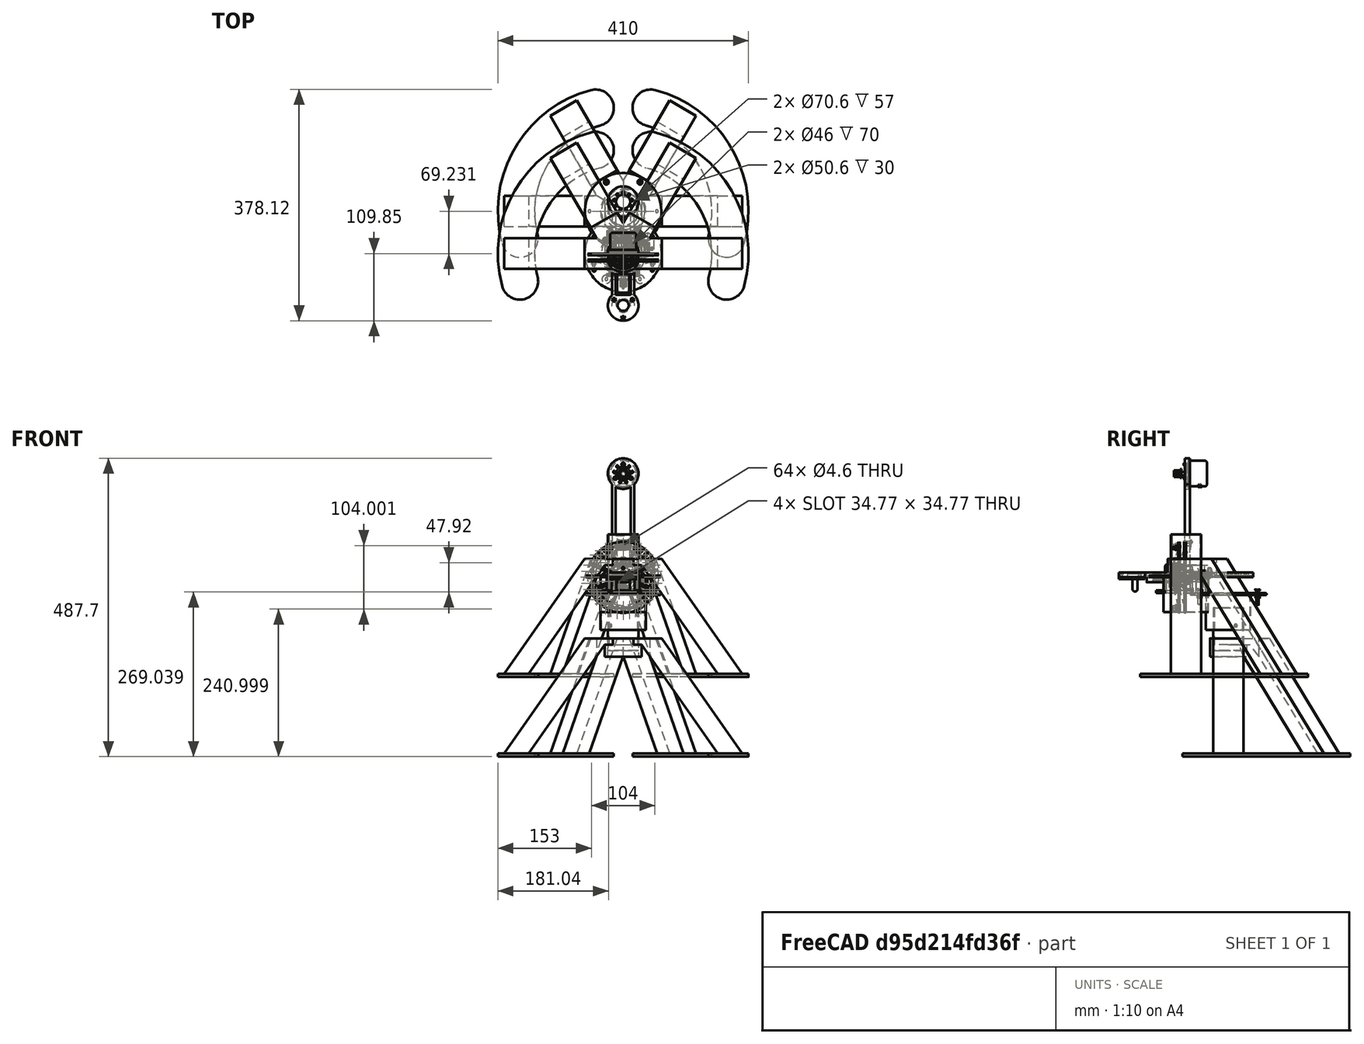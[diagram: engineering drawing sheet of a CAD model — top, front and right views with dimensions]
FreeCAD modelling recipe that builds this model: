
FCSTD DOCUMENT  (FreeCAD 1.0R38641 +678 (Git))
Label: assembly_Pendulum_fusion
License: All rights reserved
LicenseURL: https://en.wikipedia.org/wiki/All_rights_reserved
objects: Part::Feature×161, App::Part×99, Sketcher::SketchObject×51, Part::FeaturePython×47, PartDesign::Pad×32, PartDesign::CoordinateSystem×25, PartDesign::Pocket×17, Mesh::Feature×15, App::Link×14, PartDesign::Body×13, PartDesign::PolarPattern×7, PartDesign::Fillet×7, App::DocumentObjectGroup×5, PartDesign::Chamfer×4, Part::MultiFuse×3, App::FeaturePython×1, PartDesign::Revolution×1
note: 548 computed .brp shape members not serialized (recipe doc carries the construction recipe); baked Part::Feature solids carry a one-line shape summary decoded from their .brp

FEATURE [PartDesign::CoordinateSystem] LCS_Origin
  AttacherType = Attacher::AttachEngine3D
  AttachmentSupport = -> [X_Axis]
  MapMode = 2
FEATURE [App::DocumentObjectGroup] Constraints
FEATURE [App::FeaturePython] Variables  # WARN: FeaturePython — macro-defined, semantics opaque (R4)
  Type = App::PropertyContainer
  arm_rotation = 0
FEATURE [App::DocumentObjectGroup] Configurations
FEATURE [Sketcher::SketchObject] Sketch
  ArcFitTolerance = 1e-06
  AttachmentSupport = -> [XZ_Plane001]
  FullyConstrained = true
  MakeInternals = false
  MapMode = 5
  Placement = pos=(0,0,0) rot=(1,0,0;1.5708rad)
  sketch-geometry (13):
    g0: LineSegment StartX=5.6759 StartY=30.0968 StartZ=0 EndX=23.0689 EndY=6 EndZ=0
    g1: LineSegment StartX=23.0689 StartY=6 StartZ=0 EndX=34 EndY=6 EndZ=0
    g2: LineSegment StartX=34 StartY=6 StartZ=0 EndX=34 EndY=0 EndZ=0
    g3: LineSegment StartX=34 StartY=0 StartZ=0 EndX=20 EndY=0 EndZ=0
    g4: LineSegment StartX=20 StartY=0 StartZ=0 EndX=4.86567 EndY=20.9676 EndZ=0
    g5: LineSegment StartX=-4.86567 StartY=20.9676 StartZ=0 EndX=-20 EndY=0 EndZ=0
    g6: LineSegment StartX=-20 StartY=0 StartZ=0 EndX=-34 EndY=0 EndZ=0
    g7: LineSegment StartX=-34 StartY=0 StartZ=0 EndX=-34 EndY=6 EndZ=0
    g8: LineSegment StartX=-34 StartY=6 StartZ=0 EndX=-23.0689 EndY=6 EndZ=0
    g9: LineSegment StartX=-23.0689 StartY=6 StartZ=0 EndX=-5.6759 EndY=30.0968 EndZ=0
    g10: Circle CenterX=-1e-16 CenterY=26 CenterZ=0 NormalX=0 NormalY=0 NormalZ=1 AngleXU=0 Radius=2.8
    g11: ArcOfCircle CenterX=-1e-16 CenterY=26 CenterZ=0 NormalX=0 NormalY=0 NormalZ=1 AngleXU=0 Radius=7 StartAngle=0.625205 EndAngle=2.51639
    g12: ArcOfCircle CenterX=-1e-16 CenterY=26 CenterZ=0 NormalX=0 NormalY=0 NormalZ=1 AngleXU=0 Radius=7 StartAngle=3.94384 EndAngle=5.48094
  constraints (36):
    c: Coincident(g0,g1)
    c: Horizontal(g1)
    c: Coincident(g1,g2)
    c: PointOnObject(g2,g-1)
    c: Coincident(g2,g3)
    c: PointOnObject(g3,g-1)
    c: Coincident(g3,g4)
    c: Coincident(g5,g6)
    c: PointOnObject(g6,g-1)
    c: Coincident(g6,g7)
    c: Vertical(g7)
    c: Coincident(g7,g8)
    c: Horizontal(g8)
    c: Coincident(g8,g9)
    c: Symmetric(g9,g0,g-2)
    c: Parallel(g9,g5)
    c: Parallel(g0,g4)
    c: Vertical(g2)
    c: Equal(g7,g2)
    c: DistanceY(g7,g7) = 6
    c: Equal(g8,g1)
    c: DistanceX(g6,g6) = 14
    c: DistanceX(g5,g3) = 40
    c: Diameter(g10) = 5.6
    c: Coincident(g11,g10)
    c: Coincident(g11,g0)
    c: Equal(g11,g12)
    c: Coincident(g11,g12)
    c: Coincident(g4,g12)
    c: Coincident(g5,g12)
    c: DistanceY(g-1,g10) = 26
    c: Distance(g5,g9) = 6
    c: Distance(g4,g0) = 6
    c: Tangent(g9,g11) = 1.5708
    c: Diameter(g11) = 14
    c: Symmetric(g5,g3,g-2)
FEATURE [PartDesign::Pad] Pad  label="Pad_Main"
  Direction = (0,-1,2e-16)
  Length = 10
  Length2 = 10
  Placement = pos=(0,0,0) rot=(1,0,0;1.5708rad)
  Profile = -> Sketch
  ReferenceAxis = -> Sketch [N_Axis]
  Refine = true
  Suppressed = false
  Type = 0
FEATURE [Sketcher::SketchObject] Sketch001
  ArcFitTolerance = 1e-06
  AttachmentSupport = -> [Pad]
  ExternalGeometry = -> [Pad]
  FullyConstrained = true
  MakeInternals = false
  MapMode = 5
  Placement = pos=(0,-10,0) rot=(1,0,0;1.5708rad)
  sketch-geometry (2):
    g0: Circle CenterX=0 CenterY=26 CenterZ=0 NormalX=0 NormalY=0 NormalZ=1 AngleXU=0 Radius=3.8
    g1: Circle CenterX=0 CenterY=26 CenterZ=0 NormalX=0 NormalY=0 NormalZ=1 AngleXU=0 Radius=2.8
  constraints (4):
    c: Coincident(g0,g-3)
    c: Coincident(g1,g0)
    c: Diameter(g1) = 5.6
    c: Diameter(g0) = 7.6
FEATURE [PartDesign::Pad] Pad001  label="Pad_Shaft"
  BaseFeature = -> Pad
  Direction = (0,-1,2e-16)
  Length = 16.6
  Length2 = 10
  Placement = pos=(0,0,0) rot=(1,0,0;1.5708rad)
  Profile = -> Sketch001
  ReferenceAxis = -> Sketch001 [N_Axis]
  Refine = true
  Suppressed = false
  Type = 0
FEATURE [Sketcher::SketchObject] Sketch002
  ArcFitTolerance = 1e-06
  AttachmentSupport = -> [Pad001]
  ExternalGeometry = -> [Pad001]
  FullyConstrained = true
  MakeInternals = false
  MapMode = 5
  Placement = pos=(0,-10,0) rot=(1,0,0;1.5708rad)
  sketch-geometry (2):
    g0: Circle CenterX=0 CenterY=26 CenterZ=0 NormalX=0 NormalY=0 NormalZ=1 AngleXU=0 Radius=3.8
    g1: Circle CenterX=0 CenterY=26 CenterZ=0 NormalX=0 NormalY=0 NormalZ=1 AngleXU=0 Radius=6.5
  constraints (4):
    c: Coincident(g0,g-3)
    c: Equal(g0,g-3)
    c: Coincident(g1,g0)
    c: Diameter(g1) = 13
FEATURE [PartDesign::Pad] Pad002  label="Pad_Thrust"
  BaseFeature = -> Pad001
  Direction = (0,-1,2e-16)
  Length = 10
  Length2 = 10
  Placement = pos=(0,0,0) rot=(1,0,0;1.5708rad)
  Profile = -> Sketch002
  ReferenceAxis = -> Sketch002 [N_Axis]
  Refine = true
  Suppressed = false
  Type = 0
FEATURE [Sketcher::SketchObject] Sketch003
  ArcFitTolerance = 1e-06
  AttachmentSupport = -> [Pad002]
  FullyConstrained = true
  MakeInternals = false
  MapMode = 5
  Placement = pos=(0,2.9e-15,0) rot=(-1,0,0;1.5708rad)
  sketch-geometry (7):
    g0: LineSegment StartX=-4.8 StartY=-26 StartZ=0 EndX=-2.4 EndY=-30.1569 EndZ=0
    g1: LineSegment StartX=-2.4 StartY=-30.1569 StartZ=0 EndX=2.4 EndY=-30.1569 EndZ=0
    g2: LineSegment StartX=2.4 StartY=-30.1569 StartZ=0 EndX=4.8 EndY=-26 EndZ=0
    g3: LineSegment StartX=4.8 StartY=-26 StartZ=0 EndX=2.4 EndY=-21.8431 EndZ=0
    g4: LineSegment StartX=2.4 StartY=-21.8431 StartZ=0 EndX=-2.4 EndY=-21.8431 EndZ=0
    g5: LineSegment StartX=-2.4 StartY=-21.8431 StartZ=0 EndX=-4.8 EndY=-26 EndZ=0
    g6: Circle [constr] CenterX=0 CenterY=-26 CenterZ=0 NormalX=0 NormalY=0 NormalZ=1 AngleXU=0 Radius=4.8
  constraints (16):
    c: Coincident(g0,g1)
    c: Coincident(g1,g2)
    c: Coincident(g2,g3)
    c: Coincident(g3,g4)
    c: Coincident(g4,g5)
    c: Coincident(g5,g0)
    c: Equal(g0, g1-g5) x5
    c: PointOnObject(g0,g6)
    c: PointOnObject(g1,g6)
    c: PointOnObject(g2,g6)
    c: PointOnObject(g3,g6)
    c: PointOnObject(g4,g6)
    c: PointOnObject(g5,g6)
    c: Coincident(g6,g-3)
    c: Horizontal(g4)
    c: Diameter(g6) = 9.6
FEATURE [PartDesign::Pocket] Pocket
  BaseFeature = -> Pad002
  Direction = (0,-1,-2e-16)
  Length = 3
  Length2 = 5
  Placement = pos=(0,0,0) rot=(1,0,0;1.5708rad)
  Profile = -> Sketch003
  ReferenceAxis = -> Sketch003 [N_Axis]
  Refine = true
  Suppressed = false
  Type = 0
FEATURE [Sketcher::SketchObject] Sketch005  label="Sketch_section"
  ArcFitTolerance = 0
  AttachmentSupport = -> [XZ_Plane003]
  FullyConstrained = true
  MakeInternals = false
  MapMode = 5
  Placement = pos=(0,0,0) rot=(1,0,0;1.5708rad)
  sketch-geometry (12):
    g0: LineSegment StartX=4 StartY=-3.5 StartZ=0 EndX=6.5 EndY=-3.5 EndZ=0
    g1: LineSegment StartX=11 StartY=-3.5 StartZ=0 EndX=11 EndY=3.5 EndZ=0
    g2: LineSegment StartX=11 StartY=3.5 StartZ=0 EndX=9.25 EndY=3.5 EndZ=0
    g3: LineSegment StartX=4 StartY=3.5 StartZ=0 EndX=4 EndY=-3.5 EndZ=0
    g4: LineSegment StartX=6.5 StartY=3.5 StartZ=0 EndX=6.75 EndY=3.25 EndZ=0
    g5: LineSegment StartX=6.75 StartY=3.25 StartZ=0 EndX=9 EndY=3.25 EndZ=0
    g6: LineSegment StartX=9 StartY=3.25 StartZ=0 EndX=9.25 EndY=3.5 EndZ=0
    g7: LineSegment StartX=6.5 StartY=-3.5 StartZ=0 EndX=6.75 EndY=-3.25 EndZ=0
    g8: LineSegment StartX=6.75 StartY=-3.25 StartZ=0 EndX=9 EndY=-3.25 EndZ=0
    g9: LineSegment StartX=9 StartY=-3.25 StartZ=0 EndX=9.25 EndY=-3.5 EndZ=0
    g10: LineSegment StartX=6.5 StartY=3.5 StartZ=0 EndX=4 EndY=3.5 EndZ=0
    g11: LineSegment StartX=9.25 StartY=-3.5 StartZ=0 EndX=11 EndY=-3.5 EndZ=0
  constraints (33):
    c: Coincident(g11,g1)
    c: Coincident(g1,g2)
    c: Coincident(g10,g3)
    c: Coincident(g3,g0)
    c: Horizontal(g0)
    c: Horizontal(g2)
    c: Vertical(g1)
    c: DistanceY(g1) = 7
    c: DistanceX(g0) = 4
    c: DistanceX(g11) = 11
    c: Coincident(g4,g5)
    c: Horizontal(g5)
    c: Coincident(g5,g6)
    c: Coincident(g7,g8)
    c: Horizontal(g8)
    c: Coincident(g8,g9)
    c: Coincident(g2,g6)
    c: Coincident(g10,g4)
    c: Tangent(g2,g10)
    c: Coincident(g0,g7)
    c: Coincident(g11,g9)
    c: Tangent(g0,g11)
    c: Equal(g4,g6)
    c: Equal(g6,g7)
    c: Angle(g10,g4) = 2.35619
    c: DistanceX(g2) = -1.75
    c: DistanceX(g10) = -2.5
    c: Equal(g0,g10)
    c: Equal(g11,g2)
    c: Equal(g9,g7)
    c: Parallel(g9,g4)
    c: DistanceY(g5,g1) = 0.25
    c: Symmetric(g0,g3,g-1)
FEATURE [PartDesign::Revolution] Revolution
  Angle = 360
  Angle2 = 60
  Axis = (0,2e-16,1)
  Base = (0,0,0)
  Placement = pos=(0,0,0) rot=(1,0,0;1.5708rad)
  Profile = -> Sketch005
  ReferenceAxis = -> Sketch005 [V_Axis]
  Refine = true
  Suppressed = false
  Type = 0
FEATURE [PartDesign::Chamfer] Chamfer
  Angle = 45
  Base = -> Revolution [Edge12,Edge11]
  BaseFeature = -> Revolution
  ChamferType = 0
  FlipDirection = false
  Placement = pos=(0,0,0) rot=(1,0,0;1.5708rad)
  Refine = true
  Size = 0.25
  Size2 = 1
  SupportTransform = false
  Suppressed = false
  UseAllEdges = false
FEATURE [PartDesign::CoordinateSystem] Bearing_Axis
  AttacherType = Attacher::AttachEngine3D
  AttachmentSupport = -> [Chamfer]
  MapMode = 45
  Placement = pos=(1.89e-14,1.7e-15,3.5) rot=(0,0,1;0rad)
FEATURE [PartDesign::Body] Body002  label="Body_Bearing"
  AllowCompound = false
  Group = -> [Sketch005,Revolution,Chamfer,Bearing_Axis]
  Origin = -> Origin003
  Tip = -> Chamfer
FEATURE [Sketcher::SketchObject] Sketch006
  ArcFitTolerance = 1e-06
  AttachmentSupport = -> [XY_Plane004]
  FullyConstrained = true
  MakeInternals = false
  MapMode = 5
  sketch-geometry (1):
    g0: Circle CenterX=0 CenterY=84.85 CenterZ=0 NormalX=0 NormalY=0 NormalZ=1 AngleXU=0 Radius=23
  constraints (3):
    c: PointOnObject(g0,g-2)
    c: DistanceY(g-1,g0) = 84.85
    c: Diameter(g0) = 46
FEATURE [Sketcher::SketchObject] Sketch007
  ArcFitTolerance = 1e-06
  AttachmentSupport = -> [XY_Plane004]
  FullyConstrained = true
  MakeInternals = false
  MapMode = 5
  sketch-geometry (33):
    g0: LineSegment StartX=-18 StartY=67.5 StartZ=0 EndX=-18 EndY=-67.5 EndZ=0
    g1: LineSegment StartX=18 StartY=-67.5 StartZ=0 EndX=18 EndY=67.5 EndZ=0
    g2: ArcOfCircle CenterX=0 CenterY=84.8494 CenterZ=0 NormalX=0 NormalY=0 NormalZ=1 AngleXU=0 Radius=25 StartAngle=5.51619 EndAngle=10.1918
    g3: Circle CenterX=0 CenterY=84.8494 CenterZ=0 NormalX=0 NormalY=0 NormalZ=1 AngleXU=0 Radius=11.5
    g4: Circle CenterX=0 CenterY=99.8494 CenterZ=0 NormalX=0 NormalY=0 NormalZ=1 AngleXU=0 Radius=1.8
    g5: Circle CenterX=9.64181 CenterY=96.34 CenterZ=0 NormalX=0 NormalY=0 NormalZ=1 AngleXU=0 Radius=1.8
    g6: Circle CenterX=14.7721 CenterY=87.4541 CenterZ=0 NormalX=0 NormalY=0 NormalZ=1 AngleXU=0 Radius=1.8
    g7: Circle CenterX=12.9904 CenterY=77.3494 CenterZ=0 NormalX=0 NormalY=0 NormalZ=1 AngleXU=0 Radius=1.8
    g8: Circle CenterX=5.1303 CenterY=70.754 CenterZ=0 NormalX=0 NormalY=0 NormalZ=1 AngleXU=0 Radius=1.8
    g9: Circle CenterX=-5.1303 CenterY=70.754 CenterZ=0 NormalX=0 NormalY=0 NormalZ=1 AngleXU=0 Radius=1.8
    g10: Circle CenterX=-12.9904 CenterY=77.3494 CenterZ=0 NormalX=0 NormalY=0 NormalZ=1 AngleXU=0 Radius=1.8
    g11: Circle CenterX=-14.7721 CenterY=87.4541 CenterZ=0 NormalX=0 NormalY=0 NormalZ=1 AngleXU=0 Radius=1.8
    g12: Circle CenterX=-9.64181 CenterY=96.34 CenterZ=0 NormalX=0 NormalY=0 NormalZ=1 AngleXU=0 Radius=1.8
    g13: LineSegment [constr] StartX=-9.64181 StartY=96.34 StartZ=0 EndX=0 EndY=84.8494 EndZ=0
    g14: LineSegment [constr] StartX=-14.7721 StartY=87.4541 StartZ=0 EndX=0 EndY=84.8494 EndZ=0
    g15: LineSegment [constr] StartX=-12.9904 StartY=77.3494 StartZ=0 EndX=0 EndY=84.8494 EndZ=0
    g16: LineSegment [constr] StartX=-5.1303 StartY=70.754 StartZ=0 EndX=0 EndY=84.8494 EndZ=0
    g17: LineSegment [constr] StartX=5.1303 StartY=70.754 StartZ=0 EndX=0 EndY=84.8494 EndZ=0
    g18: LineSegment [constr] StartX=12.9904 StartY=77.3494 StartZ=0 EndX=0 EndY=84.8494 EndZ=0
    g19: LineSegment [constr] StartX=14.7721 StartY=87.4541 StartZ=0 EndX=0 EndY=84.8494 EndZ=0
    g20: LineSegment [constr] StartX=9.64181 StartY=96.34 StartZ=0 EndX=0 EndY=84.8494 EndZ=0
    g21: Circle CenterX=-7.78 CenterY=-27 CenterZ=0 NormalX=0 NormalY=0 NormalZ=1 AngleXU=0 Radius=1.8
    g22: Circle CenterX=7.78 CenterY=-27 CenterZ=0 NormalX=0 NormalY=0 NormalZ=1 AngleXU=0 Radius=1.8
    g23: ArcOfCircle CenterX=0 CenterY=-84.8494 CenterZ=0 NormalX=0 NormalY=0 NormalZ=1 AngleXU=0 Radius=25 StartAngle=2.3746 EndAngle=7.05018
    g24: Circle CenterX=0 CenterY=-84.8494 CenterZ=0 NormalX=0 NormalY=0 NormalZ=1 AngleXU=0 Radius=11.25
    g25: LineSegment StartX=-12.5 StartY=63.1987 StartZ=0 EndX=-12.5 EndY=-16.8013 EndZ=0
    g26: LineSegment StartX=-12.5 StartY=-16.8013 StartZ=0 EndX=12.5 EndY=-16.8013 EndZ=0
    g27: LineSegment StartX=12.5 StartY=-16.8013 StartZ=0 EndX=12.5 EndY=63.1987 EndZ=0
    g28: LineSegment StartX=-12.5 StartY=-33.5 StartZ=0 EndX=-12.5 EndY=-67.5 EndZ=0
    g29: LineSegment StartX=-12.5 StartY=-67.5 StartZ=0 EndX=12.5 EndY=-67.5 EndZ=0
    g30: LineSegment StartX=12.5 StartY=-67.5 StartZ=0 EndX=12.5 EndY=-33.5 EndZ=0
    g31: LineSegment StartX=12.5 StartY=-33.5 StartZ=0 EndX=-12.5 EndY=-33.5 EndZ=0
    g32: ArcOfCircle CenterX=0 CenterY=84.8494 CenterZ=0 NormalX=0 NormalY=0 NormalZ=1 AngleXU=0 Radius=25 StartAngle=4.18879 EndAngle=5.23599
  constraints (88):
    c: Vertical(g0)
    c: Vertical(g1)
    c: Symmetric(g0,g1,g-1)
    c: DistanceX(g0,g1) = 36
    c: DistanceY(g1,g1) = 135
    c: PointOnObject(g2,g-2)
    c: Diameter(g2) = 50
    c: Coincident(g2,g0)
    c: Coincident(g2,g1)
    c: Coincident(g3,g2)
    c: Diameter(g3) = 23
    c: PointOnObject(g4,g-2)
    c: Coincident(g13,g12)
    c: Coincident(g13,g2)
    c: Coincident(g14,g11)
    c: Coincident(g14,g2)
    c: Coincident(g15,g10)
    c: Coincident(g15,g2)
    c: Coincident(g16,g9)
    c: Coincident(g16,g2)
    c: Coincident(g17,g8)
    c: Coincident(g17,g2)
    c: Coincident(g18,g7)
    c: Coincident(g18,g2)
    c: Coincident(g19,g6)
    c: Coincident(g19,g2)
    c: Coincident(g20,g5)
    c: Coincident(g20,g2)
    c: Equal(g4,g5)
    c: Equal(g5,g6)
    c: Equal(g6,g7)
    c: Equal(g7,g8)
    c: Equal(g8,g9)
    c: Equal(g9,g10)
    c: Equal(g10,g11)
    c: Equal(g11,g12)
    c: Equal(g13,g14)
    c: Equal(g14,g15)
    c: Equal(g15,g16)
    c: Equal(g16,g17)
    c: Equal(g17,g18)
    c: Equal(g18,g19)
    c: Equal(g19,g20)
    c: DistanceY(g2,g4) = 15
    c: Distance(g13) = 15
    c: Diameter(g4) = 3.6
    c: Angle(g-2,g20) = 2.44346
    c: Angle(g19,g20) = 0.698132
    c: Angle(g18,g19) = 0.698132
    c: Angle(g17,g18) = 0.698132
    c: Angle(g16,g17) = 0.698132
    c: Angle(g15,g16) = 0.698132
    c: Angle(g14,g15) = 0.698132
    c: Angle(g13,g14) = 0.698132
    c: Equal(g22,g21)
    c: Diameter(g21) = 3.6
    c: DistanceX(g21,g22) = 15.56
    c: Symmetric(g21,g22,g-2)
    c: DistanceY(g22,g-1) = 27
    c: PointOnObject(g23,g-2)
    c: Diameter(g23) = 50
    c: Coincident(g23,g1)
    c: Coincident(g23,g0)
    c: Coincident(g24,g23)
    c: Diameter(g24) = 22.5
    c: Vertical(g25)
    c: Vertical(g27)
    c: Horizontal(g26)
    c: Coincident(g28,g29)
    c: Coincident(g29,g30)
    c: Coincident(g30,g31)
    c: Coincident(g31,g28)
    c: Vertical(g28)
    c: Vertical(g30)
    c: Horizontal(g29)
    c: Symmetric(g27,g25,g-2)
    c: DistanceY(g25,g25) = 80
    c: DistanceX(g25,g27) = 25
    c: PointOnObject(g1,g29)
    c: Symmetric(g28,g30,g-2)
    c: DistanceX(g31,g31) = 25
    c: DistanceY(g28,g28) = 34
    c: Diameter(g32) = 50
    c: Coincident(g32,g25)
    c: Coincident(g32,g27)
    c: Coincident(g32,g2)
    c: Coincident(g26,g25)
    c: Coincident(g27,g26)
FEATURE [PartDesign::Pad] Pad004  label="Pad_Arm"
  Direction = (0,0,1)
  Length = 8
  Length2 = 10
  Profile = -> Sketch007
  ReferenceAxis = -> Sketch007 [N_Axis]
  Refine = true
  Suppressed = false
  Type = 0
FEATURE [PartDesign::Pocket] Pocket001  label="Pocket_Motor"
  BaseFeature = -> Pad004
  Direction = (0,0,-1)
  Length = 3
  Length2 = 5
  Profile = -> Sketch006
  ReferenceAxis = -> Sketch006 [N_Axis]
  Refine = true
  Reversed = true
  Suppressed = false
  Type = 0
FEATURE [PartDesign::CoordinateSystem] Arm_Axis_Top
  AttacherType = Attacher::AttachEngine3D
  AttachmentOffset = pos=(0,0,0) rot=(0,0,-1;1.5708rad)
  AttachmentSupport = -> [Pocket001]
  MapMode = 11
  Placement = pos=(2e-16,99.8494,8) rot=(0,0,1;0rad)
FEATURE [Sketcher::SketchObject] Sketch008
  ArcFitTolerance = 1e-06
  AttachmentSupport = -> [XZ_Plane005]
  FullyConstrained = true
  MakeInternals = false
  MapMode = 5
  Placement = pos=(0,0,0) rot=(1,0,0;1.5708rad)
  sketch-geometry (8):
    g0: LineSegment StartX=-3.7 StartY=11.6 StartZ=0 EndX=-3.7 EndY=8 EndZ=0
    g1: LineSegment StartX=-3.7 StartY=8 StartZ=0 EndX=3.7 EndY=8 EndZ=0
    g2: LineSegment StartX=3.7 StartY=8 StartZ=0 EndX=3.7 EndY=11.6 EndZ=0
    g3: LineSegment StartX=3.7 StartY=11.6 StartZ=0 EndX=-3.7 EndY=11.6 EndZ=0
    g4: LineSegment StartX=-3.7 StartY=-8 StartZ=0 EndX=-3.7 EndY=-11.6 EndZ=0
    g5: LineSegment StartX=-3.7 StartY=-11.6 StartZ=0 EndX=3.7 EndY=-11.6 EndZ=0
    g6: LineSegment StartX=3.7 StartY=-11.6 StartZ=0 EndX=3.7 EndY=-8 EndZ=0
    g7: LineSegment StartX=3.7 StartY=-8 StartZ=0 EndX=-3.7 EndY=-8 EndZ=0
  constraints (21):
    c: Coincident(g0,g1)
    c: Coincident(g1,g2)
    c: Coincident(g2,g3)
    c: Coincident(g3,g0)
    c: Vertical(g0)
    c: Vertical(g2)
    c: Coincident(g4,g5)
    c: Coincident(g5,g6)
    c: Coincident(g6,g7)
    c: Coincident(g7,g4)
    c: Vertical(g4)
    c: Vertical(g6)
    c: Horizontal(g5)
    c: Horizontal(g7)
    c: Symmetric(g0,g6,g-1)
    c: DistanceY(g-1,g1) = 8
    c: DistanceY(g2,g2) = 3.6
    c: DistanceX(g3,g3) = 7.4
    c: Symmetric(g2,g4,g-1)
    c: Symmetric(g1,g0,g-2)
    c: Horizontal(g3)
FEATURE [Sketcher::SketchObject] Sketch009
  ArcFitTolerance = 1e-06
  AttachmentSupport = -> [XY_Plane005]
  FullyConstrained = true
  MakeInternals = false
  MapMode = 5
  sketch-geometry (1):
    g0: Circle CenterX=0 CenterY=-6 CenterZ=0 NormalX=0 NormalY=0 NormalZ=1 AngleXU=0 Radius=2.25
  constraints (3):
    c: PointOnObject(g0,g-2)
    c: Diameter(g0) = 4.5
    c: DistanceY(g0,g-1) = 6
FEATURE [Sketcher::SketchObject] Sketch010
  ArcFitTolerance = 1e-06
  AttachmentOffset = pos=(0,0,0) rot=(1,0,0;0.392699rad)
  AttachmentSupport = -> [YZ_Plane005]
  FullyConstrained = true
  MakeInternals = false
  MapMode = 5
  Placement = pos=(0,0,0) rot=(0.639338,0.639338,0.427192;2.33414rad)
  sketch-geometry (4):
    g0: LineSegment StartX=-3 StartY=14.5 StartZ=0 EndX=-12 EndY=14.5 EndZ=0
    g1: LineSegment StartX=-12 StartY=14.5 StartZ=0 EndX=-5 EndY=44.5 EndZ=0
    g2: LineSegment StartX=-5 StartY=44.5 StartZ=0 EndX=-3 EndY=44.5 EndZ=0
    g3: LineSegment StartX=-3 StartY=44.5 StartZ=0 EndX=-3 EndY=14.5 EndZ=0
  constraints (12):
    c: Coincident(g0,g1)
    c: Coincident(g1,g2)
    c: Horizontal(g2)
    c: Coincident(g2,g3)
    c: Coincident(g3,g0)
    c: Horizontal(g0)
    c: Vertical(g3)
    c: DistanceX(g0,g-1) = 3
    c: DistanceY(g-1,g0) = 14.5
    c: DistanceY(g3,g3) = 30
    c: DistanceX(g2,g2) = 2
    c: DistanceX(g0,g0) = 9
FEATURE [Sketcher::SketchObject] Sketch011
  ArcFitTolerance = 1e-06
  AttachmentSupport = -> [XZ_Plane005]
  FullyConstrained = true
  MakeInternals = false
  MapMode = 5
  Placement = pos=(0,0,0) rot=(1,0,0;1.5708rad)
  sketch-geometry (1):
    g0: Circle CenterX=0 CenterY=52 CenterZ=0 NormalX=0 NormalY=0 NormalZ=1 AngleXU=0 Radius=2.3
  constraints (3):
    c: PointOnObject(g0,g-2)
    c: Diameter(g0) = 4.6
    c: DistanceY(g-1,g0) = 52
FEATURE [Sketcher::SketchObject] Sketch012
  ArcFitTolerance = 1e-06
  AttachmentSupport = -> [XZ_Plane005]
  FullyConstrained = true
  MakeInternals = false
  MapMode = 5
  Placement = pos=(0,0,0) rot=(1,0,0;1.5708rad)
  sketch-geometry (5):
    g0: LineSegment StartX=0 StartY=0 StartZ=0 EndX=-1.04189 EndY=5.90885 EndZ=0
    g1: LineSegment StartX=-1.04189 StartY=5.90885 StartZ=0 EndX=-0.2 EndY=5.3692 EndZ=0
    g2: LineSegment StartX=-0.2 StartY=5.3692 StartZ=0 EndX=0.2 EndY=5.3692 EndZ=0
    g3: LineSegment StartX=0.2 StartY=5.3692 StartZ=0 EndX=1.04189 EndY=5.90885 EndZ=0
    g4: LineSegment StartX=1.04189 StartY=5.90885 StartZ=0 EndX=0 EndY=0 EndZ=0
  constraints (13):
    c: Coincident(g-1,g0)
    c: Coincident(g0,g1)
    c: Coincident(g1,g2)
    c: Horizontal(g2)
    c: Coincident(g2,g3)
    c: Coincident(g3,g4)
    c: Coincident(g4,g0)
    c: Symmetric(g3,g0,g-2)
    c: Angle(g4,g0) = 0.349066
    c: DistanceX(g2,g2) = 0.4
    c: Distance(g4) = 6
    c: Distance(g3) = 1
    c: Distance(g1) = 1
FEATURE [Sketcher::SketchObject] Sketch013
  ArcFitTolerance = 1e-06
  AttachmentSupport = -> [XZ_Plane005]
  FullyConstrained = true
  MakeInternals = false
  MapMode = 5
  Placement = pos=(0,0,0) rot=(1,0,0;1.5708rad)
  sketch-geometry (2):
    g0: Circle CenterX=0 CenterY=0 CenterZ=0 NormalX=0 NormalY=0 NormalZ=1 AngleXU=0 Radius=5
    g1: Circle CenterX=0 CenterY=0 CenterZ=0 NormalX=0 NormalY=0 NormalZ=1 AngleXU=0 Radius=15
  constraints (4):
    c: Coincident(g0,g-1)
    c: Coincident(g1,g0)
    c: Diameter(g1) = 30
    c: Diameter(g0) = 10
FEATURE [Sketcher::SketchObject] Sketch014
  ArcFitTolerance = 1e-06
  AttachmentSupport = -> [XZ_Plane005]
  FullyConstrained = true
  MakeInternals = false
  MapMode = 5
  Placement = pos=(0,0,0) rot=(1,0,0;1.5708rad)
  sketch-geometry (6):
    g0: ArcOfCircle CenterX=0 CenterY=0 CenterZ=0 NormalX=0 NormalY=0 NormalZ=1 AngleXU=0 Radius=15 StartAngle=1.23918 EndAngle=1.90241
    g1: ArcOfCircle CenterX=0 CenterY=0 CenterZ=0 NormalX=0 NormalY=0 NormalZ=1 AngleXU=0 Radius=46 StartAngle=1.23918 EndAngle=1.90241
    g2: LineSegment [constr] StartX=0 StartY=0 StartZ=0 EndX=-19.5341 EndY=56.7311 EndZ=0
    g3: LineSegment [constr] StartX=0 StartY=0 StartZ=0 EndX=19.5341 EndY=56.7311 EndZ=0
    g4: LineSegment StartX=-4.88352 StartY=14.1828 StartZ=0 EndX=-14.9761 EndY=43.4939 EndZ=0
    g5: LineSegment StartX=14.9761 StartY=43.4939 StartZ=0 EndX=4.88352 EndY=14.1828 EndZ=0
  constraints (17):
    c: Coincident(g0,g-1)
    c: Coincident(g1,g0)
    c: Coincident(g2,g0)
    c: Coincident(g3,g0)
    c: Coincident(g4,g0)
    c: Coincident(g4,g1)
    c: Coincident(g5,g1)
    c: Coincident(g5,g0)
    c: Symmetric(g2,g3,g-2)
    c: Angle(g3,g2) = 0.663225
    c: PointOnObject(g0,g3)
    c: PointOnObject(g1,g3)
    c: PointOnObject(g0,g2)
    c: PointOnObject(g1,g2)
    c: Diameter(g1) = 92
    c: Diameter(g0) = 30
    c: Distance(g3) = 60
FEATURE [Sketcher::SketchObject] Sketch015
  ArcFitTolerance = 1e-06
  AttachmentSupport = -> [XZ_Plane005]
  FullyConstrained = true
  MakeInternals = false
  MapMode = 5
  Placement = pos=(0,0,0) rot=(1,0,0;1.5708rad)
  sketch-geometry (2):
    g0: Circle CenterX=0 CenterY=0 CenterZ=0 NormalX=0 NormalY=0 NormalZ=1 AngleXU=0 Radius=58
    g1: Circle CenterX=0 CenterY=0 CenterZ=0 NormalX=0 NormalY=0 NormalZ=1 AngleXU=0 Radius=5
  constraints (4):
    c: Coincident(g0,g-1)
    c: Diameter(g0) = 116
    c: Coincident(g1,g0)
    c: Diameter(g1) = 10
FEATURE [PartDesign::Pad] Pad005  label="Pad_External"
  Direction = (0,-1,2e-16)
  Length = 3
  Length2 = 10
  Placement = pos=(0,0,0) rot=(1,0,0;1.5708rad)
  Profile = -> Sketch015
  ReferenceAxis = -> Sketch015 [N_Axis]
  Refine = true
  Suppressed = false
  Type = 0
FEATURE [PartDesign::Pocket] Pocket002  label="Pocket_Gap"
  BaseFeature = -> Pad005
  Direction = (0,1,-2e-16)
  Length = 5
  Length2 = 5
  Placement = pos=(0,0,0) rot=(1,0,0;1.5708rad)
  Profile = -> Sketch014
  ReferenceAxis = -> Sketch014 [N_Axis]
  Refine = true
  Reversed = true
  Suppressed = false
  Type = 0
FEATURE [PartDesign::PolarPattern] PolarPattern  label="PolarPattern_Gaps"
  Angle = 360
  Axis = -> Sketch014 [N_Axis]
  BaseFeature = -> Pocket002
  Mode = 0
  Occurrences = 8
  Offset = 120
  Originals = -> [Pocket002]
  Placement = pos=(0,0,0) rot=(1,0,0;1.5708rad)
  Refine = true
  Suppressed = false
  TransformMode = 0
FEATURE [PartDesign::Pad] Pad006  label="Pad_Center"
  BaseFeature = -> PolarPattern
  Direction = (0,-1,2e-16)
  Length = 12
  Length2 = 10
  Placement = pos=(0,0,0) rot=(1,0,0;1.5708rad)
  Profile = -> Sketch013
  ReferenceAxis = -> Sketch013 [N_Axis]
  Refine = true
  Suppressed = false
  Type = 0
FEATURE [PartDesign::Pocket] Pocket003  label="Pocket_Shaft"
  BaseFeature = -> Pad006
  Direction = (0,1,-2e-16)
  Length = 5
  Length2 = 5
  Placement = pos=(0,0,0) rot=(1,0,0;1.5708rad)
  Profile = -> Sketch012
  ReferenceAxis = -> Sketch012 [N_Axis]
  Refine = true
  Reversed = true
  Suppressed = false
  Type = 1
FEATURE [PartDesign::PolarPattern] PolarPattern001  label="PolarPattern_DriveShaft"
  Angle = 360
  Axis = -> Sketch012 [N_Axis]
  BaseFeature = -> Pocket003
  Mode = 0
  Occurrences = 18
  Offset = 120
  Originals = -> [Pocket003]
  Placement = pos=(0,0,0) rot=(1,0,0;1.5708rad)
  Refine = true
  Suppressed = false
  TransformMode = 0
FEATURE [PartDesign::Pocket] Pocket004  label="Pocket_Screw"
  BaseFeature = -> PolarPattern001
  Direction = (0,1,-2e-16)
  Length = 5
  Length2 = 5
  Placement = pos=(0,0,0) rot=(1,0,0;1.5708rad)
  Profile = -> Sketch011
  ReferenceAxis = -> Sketch011 [N_Axis]
  Refine = true
  Reversed = true
  Suppressed = false
  Type = 1
FEATURE [PartDesign::PolarPattern] PolarPattern002  label="PolarPattern_Inertia"
  Angle = 360
  Axis = -> Sketch011 [N_Axis]
  BaseFeature = -> Pocket004
  Mode = 0
  Occurrences = 32
  Offset = 120
  Originals = -> [Pocket004]
  Placement = pos=(0,0,0) rot=(1,0,0;1.5708rad)
  Refine = true
  Suppressed = false
  TransformMode = 0
FEATURE [PartDesign::Pad] Pad007  label="Pad_Reinforcement"
  BaseFeature = -> PolarPattern002
  Direction = (0.92388,0,-0.382683)
  Length = 2
  Length2 = 10
  Midplane = true
  Placement = pos=(0,0,0) rot=(1,0,0;1.5708rad)
  Profile = -> Sketch010
  ReferenceAxis = -> Sketch010 [N_Axis]
  Refine = true
  Suppressed = false
  Type = 0
FEATURE [PartDesign::PolarPattern] PolarPattern003  label="PolarPattern_Reinforcements"
  Angle = 360
  Axis = -> Y_Axis005
  BaseFeature = -> Pad007
  Mode = 0
  Occurrences = 8
  Offset = 120
  Originals = -> [Pad007]
  Placement = pos=(0,0,0) rot=(1,0,0;1.5708rad)
  Refine = true
  Suppressed = false
  TransformMode = 0
FEATURE [PartDesign::Pocket] Pocket005  label="Pocket_Fixation"
  BaseFeature = -> PolarPattern003
  Direction = (0,0,-1)
  Length = 30
  Length2 = 5
  Midplane = true
  Placement = pos=(0,0,0) rot=(1,0,0;1.5708rad)
  Profile = -> Sketch009
  ReferenceAxis = -> Sketch009 [N_Axis]
  Refine = true
  Suppressed = false
  Type = 0
FEATURE [PartDesign::Pocket] Pocket006  label="Pocket_Bolts"
  BaseFeature = -> Pocket005
  Direction = (0,1,-2e-16)
  Length = 12
  Length2 = 5
  Placement = pos=(0,0,0) rot=(1,0,0;1.5708rad)
  Profile = -> Sketch008
  ReferenceAxis = -> Sketch008 [N_Axis]
  Refine = true
  Reversed = true
  Suppressed = false
  Type = 0
FEATURE [Sketcher::SketchObject] Sketch016
  ArcFitTolerance = 1e-06
  AttachmentSupport = -> [XY_Plane006]
  FullyConstrained = true
  MakeInternals = false
  MapMode = 5
  sketch-geometry (8):
    g0: LineSegment StartX=-7.5 StartY=-8 StartZ=0 EndX=-7.5 EndY=-13 EndZ=0
    g1: LineSegment StartX=7.5 StartY=-13 StartZ=0 EndX=7.5 EndY=-8 EndZ=0
    g2: LineSegment StartX=7.5 StartY=-8 StartZ=0 EndX=-7.5 EndY=-8 EndZ=0
    g3: LineSegment StartX=-10 StartY=-13 StartZ=0 EndX=-10 EndY=-14.2 EndZ=0
    g4: LineSegment StartX=-10 StartY=-14.2 StartZ=0 EndX=10 EndY=-14.2 EndZ=0
    g5: LineSegment StartX=10 StartY=-14.2 StartZ=0 EndX=10 EndY=-13 EndZ=0
    g6: LineSegment StartX=10 StartY=-13 StartZ=0 EndX=7.5 EndY=-13 EndZ=0
    g7: LineSegment StartX=-7.5 StartY=-13 StartZ=0 EndX=-10 EndY=-13 EndZ=0
  constraints (21):
    c: Coincident(g1,g2)
    c: Coincident(g2,g0)
    c: Vertical(g0)
    c: Coincident(g3,g4)
    c: Coincident(g4,g5)
    c: Coincident(g5,g6)
    c: Coincident(g7,g3)
    c: Vertical(g3)
    c: Vertical(g5)
    c: Horizontal(g6)
    c: Coincident(g6,g1)
    c: Coincident(g0,g7)
    c: Symmetric(g0,g1,g-2)
    c: Symmetric(g3,g4,g-2)
    c: Symmetric(g0,g1,g-2)
    c: DistanceX(g2,g2) = 15
    c: DistanceX(g4,g4) = 20
    c: DistanceY(g3,g3) = 1.2
    c: Horizontal(g7)
    c: DistanceY(g0,g0) = 5
    c: DistanceY(g0,g-1) = 8
FEATURE [Sketcher::SketchObject] Sketch017
  ArcFitTolerance = 1e-06
  AttachmentOffset = pos=(0,0,42) rot=(0,0,1;0rad)
  AttachmentSupport = -> [XZ_Plane006]
  FullyConstrained = true
  MakeInternals = false
  MapMode = 5
  Placement = pos=(0,-42,9.3e-15) rot=(1,0,0;1.5708rad)
  sketch-geometry (5):
    g0: LineSegment StartX=-0.955065 StartY=5.41644 StartZ=0 EndX=0 EndY=0 EndZ=0
    g1: LineSegment StartX=0.955065 StartY=5.41644 StartZ=0 EndX=0 EndY=0 EndZ=0
    g2: LineSegment StartX=-0.955065 StartY=5.41644 StartZ=0 EndX=-0.2 EndY=4.76079 EndZ=0
    g3: LineSegment StartX=-0.2 StartY=4.76079 StartZ=0 EndX=0.2 EndY=4.76079 EndZ=0
    g4: LineSegment StartX=0.2 StartY=4.76079 StartZ=0 EndX=0.955065 EndY=5.41644 EndZ=0
  constraints (12):
    c: Coincident(g0,g-1)
    c: Coincident(g1,g0)
    c: Coincident(g3,g2)
    c: Coincident(g4,g3)
    c: Coincident(g4,g1)
    c: Symmetric(g3,g2,g-2)
    c: Coincident(g2,g0)
    c: Symmetric(g0,g1,g-2)
    c: Angle(g1,g0) = 0.349066
    c: DistanceX(g3,g3) = 0.4
    c: Distance(g1) = 5.5
    c: Distance(g4) = 1
FEATURE [Sketcher::SketchObject] Sketch018
  ArcFitTolerance = 1e-06
  AttachmentSupport = -> [XZ_Plane006]
  FullyConstrained = true
  MakeInternals = false
  MapMode = 5
  Placement = pos=(0,0,0) rot=(1,0,0;1.5708rad)
  sketch-geometry (1):
    g0: Circle CenterX=0 CenterY=0 CenterZ=0 NormalX=0 NormalY=0 NormalZ=1 AngleXU=0 Radius=21
  constraints (2):
    c: Coincident(g0,g-1)
    c: Diameter(g0) = 42
FEATURE [PartDesign::Pad] Pad008  label="Pad_Cylinder"
  Direction = (0,-1,2e-16)
  Length = 34
  Length2 = 10
  Placement = pos=(0,0,0) rot=(1,0,0;1.5708rad)
  Profile = -> Sketch018
  ReferenceAxis = -> Sketch018 [N_Axis]
  Refine = true
  Suppressed = false
  Type = 0
FEATURE [Sketcher::SketchObject] Sketch019
  ArcFitTolerance = 1e-06
  AttachmentSupport = -> [Pad008]
  FullyConstrained = true
  MakeInternals = false
  MapMode = 5
  Placement = pos=(0,-34,0) rot=(1,0,0;1.5708rad)
  sketch-geometry (1):
    g0: Circle CenterX=0 CenterY=0 CenterZ=0 NormalX=0 NormalY=0 NormalZ=1 AngleXU=0 Radius=7.5
  constraints (2):
    c: Coincident(g0,g-1)
    c: Diameter(g0) = 15
FEATURE [PartDesign::Pad] Pad009  label="Pad_Bearing"
  BaseFeature = -> Pad008
  Direction = (0,-1,2e-16)
  Length = 1.2
  Length2 = 10
  Placement = pos=(0,0,0) rot=(1,0,0;1.5708rad)
  Profile = -> Sketch019
  ReferenceAxis = -> Sketch019 [N_Axis]
  Refine = true
  Suppressed = false
  Type = 0
FEATURE [Sketcher::SketchObject] Sketch020
  ArcFitTolerance = 1e-06
  AttachmentSupport = -> [Pad009]
  FullyConstrained = true
  MakeInternals = false
  MapMode = 5
  Placement = pos=(0,-35.2,0) rot=(1,0,0;1.5708rad)
  sketch-geometry (1):
    g0: Circle CenterX=0 CenterY=0 CenterZ=0 NormalX=0 NormalY=0 NormalZ=1 AngleXU=0 Radius=3
  constraints (2):
    c: Coincident(g0,g-1)
    c: Diameter(g0) = 6
FEATURE [PartDesign::Pad] Pad010  label="Pad_Drive_Shaft"
  BaseFeature = -> Pad009
  Direction = (0,-1,2e-16)
  Length = 6.4
  Length2 = 10
  Placement = pos=(0,0,0) rot=(1,0,0;1.5708rad)
  Profile = -> Sketch020
  ReferenceAxis = -> Sketch020 [N_Axis]
  Refine = true
  Suppressed = false
  Type = 0
FEATURE [Sketcher::SketchObject] Sketch021
  ArcFitTolerance = 1e-06
  AttachmentSupport = -> [Pad010]
  FullyConstrained = true
  MakeInternals = false
  MapMode = 5
  Placement = pos=(0,-41.6,0) rot=(1,0,0;1.5708rad)
  sketch-geometry (1):
    g0: Circle CenterX=0 CenterY=0 CenterZ=0 NormalX=0 NormalY=0 NormalZ=1 AngleXU=0 Radius=7.5
  constraints (2):
    c: Coincident(g0,g-1)
    c: Diameter(g0) = 15
FEATURE [PartDesign::Pad] Pad011  label="Pad_Thrust001"
  BaseFeature = -> Pad010
  Direction = (0,-1,2e-16)
  Length = 1.3
  Length2 = 10
  Placement = pos=(0,0,0) rot=(1,0,0;1.5708rad)
  Profile = -> Sketch021
  ReferenceAxis = -> Sketch021 [N_Axis]
  Refine = true
  Suppressed = false
  Type = 0
FEATURE [PartDesign::Pad] Pad012  label="Pad_Tooth"
  BaseFeature = -> Pad011
  Direction = (0,-1,2e-16)
  Length = 12
  Length2 = 10
  Placement = pos=(0,0,0) rot=(1,0,0;1.5708rad)
  Profile = -> Sketch017
  ReferenceAxis = -> Sketch017 [N_Axis]
  Refine = true
  Suppressed = false
  Type = 0
FEATURE [PartDesign::PolarPattern] PolarPattern004  label="PolarPattern_Shaft"
  Angle = 360
  Axis = -> Sketch017 [N_Axis]
  BaseFeature = -> Pad012
  Mode = 0
  Occurrences = 18
  Offset = 120
  Originals = -> [Pad012]
  Placement = pos=(0,0,0) rot=(1,0,0;1.5708rad)
  Refine = true
  Suppressed = false
  TransformMode = 0
FEATURE [Sketcher::SketchObject] Sketch022
  ArcFitTolerance = 1e-06
  AttachmentSupport = -> [PolarPattern004]
  FullyConstrained = true
  MakeInternals = false
  MapMode = 5
  Placement = pos=(0,-34,0) rot=(1,0,0;1.5708rad)
  sketch-geometry (1):
    g0: Circle CenterX=0 CenterY=15 CenterZ=0 NormalX=0 NormalY=0 NormalZ=1 AngleXU=0 Radius=1.75
  constraints (3):
    c: PointOnObject(g0,g-2)
    c: Diameter(g0) = 3.5
    c: DistanceY(g-1,g0) = 15
FEATURE [PartDesign::Pocket] Pocket007  label="Pocket_Screw001"
  BaseFeature = -> PolarPattern004
  Direction = (0,1,-2e-16)
  Length = 5
  Length2 = 5
  Placement = pos=(0,0,0) rot=(1,0,0;1.5708rad)
  Profile = -> Sketch022
  ReferenceAxis = -> Sketch022 [N_Axis]
  Refine = true
  Suppressed = false
  Type = 0
FEATURE [PartDesign::PolarPattern] PolarPattern005  label="PolarPattern_Fixations"
  Angle = 360
  Axis = -> Sketch022 [N_Axis]
  BaseFeature = -> Pocket007
  Mode = 0
  Occurrences = 3
  Offset = 120
  Originals = -> [Pocket007]
  Placement = pos=(0,0,0) rot=(1,0,0;1.5708rad)
  Refine = true
  Suppressed = false
  TransformMode = 0
FEATURE [PartDesign::Pad] Pad013  label="Pad_Connector"
  BaseFeature = -> PolarPattern005
  Direction = (0,0,1)
  Length = 22
  Length2 = 10
  Placement = pos=(0,0,0) rot=(1,0,0;1.5708rad)
  Profile = -> Sketch016
  ReferenceAxis = -> Sketch016 [N_Axis]
  Refine = true
  Reversed = true
  Suppressed = false
  Type = 0
FEATURE [Sketcher::SketchObject] Sketch023
  ArcFitTolerance = 1e-06
  AttachmentSupport = -> [Pad013]
  ExternalGeometry = -> [Pad013]
  FullyConstrained = true
  MakeInternals = false
  MapMode = 5
  Placement = pos=(0,0,-22) rot=(1,0,0;3.14159rad)
  sketch-geometry (4):
    g0: LineSegment StartX=-6.5 StartY=12 StartZ=0 EndX=-6.5 EndY=9 EndZ=0
    g1: LineSegment StartX=-6.5 StartY=9 StartZ=0 EndX=6.5 EndY=9 EndZ=0
    g2: LineSegment StartX=6.5 StartY=9 StartZ=0 EndX=6.5 EndY=12 EndZ=0
    g3: LineSegment StartX=6.5 StartY=12 StartZ=0 EndX=-6.5 EndY=12 EndZ=0
  constraints (12):
    c: Coincident(g0,g1)
    c: Coincident(g1,g2)
    c: Coincident(g2,g3)
    c: Coincident(g3,g0)
    c: Vertical(g0)
    c: Vertical(g2)
    c: Horizontal(g1)
    c: Horizontal(g3)
    c: DistanceX(g-3,g0) = 1
    c: DistanceX(g1,g-4) = 1
    c: DistanceY(g-4,g1) = 1
    c: DistanceY(g0,g-3) = 1
FEATURE [PartDesign::Pocket] Pocket008  label="Pocket_Pins"
  BaseFeature = -> Pad013
  Direction = (0,0,1)
  Length = 5
  Length2 = 5
  Placement = pos=(0,0,0) rot=(1,0,0;1.5708rad)
  Profile = -> Sketch023
  ReferenceAxis = -> Sketch023 [N_Axis]
  Refine = true
  Suppressed = false
  Type = 0
FEATURE [PartDesign::Fillet] Fillet001  label="Fillet_Cylinder"
  Base = -> Pocket008 [Edge3,Edge1]
  BaseFeature = -> Pocket008
  Placement = pos=(0,0,0) rot=(1,0,0;1.5708rad)
  Radius = 3
  Refine = true
  SupportTransform = false
  Suppressed = false
  UseAllEdges = false
FEATURE [PartDesign::Fillet] Fillet002  label="Fillet_Thrust_Bearing"
  Base = -> Fillet001 [Edge61,Edge43]
  BaseFeature = -> Fillet001
  Placement = pos=(0,0,0) rot=(1,0,0;1.5708rad)
  Radius = 1
  Refine = true
  SupportTransform = false
  Suppressed = false
  UseAllEdges = false
FEATURE [PartDesign::CoordinateSystem] Motor
  AttacherType = Attacher::AttachEngine3D
  AttachmentOffset = pos=(0,0,0) rot=(-0.57735,0.57735,-0.57735;2.0944rad)
  AttachmentSupport = -> [Fillet002]
  MapMode = 11
  Placement = pos=(0,-34,15) rot=(0,0,1;0rad)
FEATURE [PartDesign::Chamfer] Chamfer001
  Angle = 45
  Base = -> Pocket006 [Edge108,Edge103,Edge102,Edge101,Edge38,Edge33,Edge32,Edge10,Edge9,Edge5,Edge6,Edge4,Edge7,Edge8,Edge15,Edge16,Edge17,Edge23,Edge24,Edge25,Edge30,Edge31,Edge123,Edge124,Edge125,Edge129,Edge128,Edge130,Edge127,Edge126,Edge110,Edge109]
  BaseFeature = -> Pocket006
  ChamferType = 0
  FlipDirection = true
  Placement = pos=(0,0,0) rot=(1,0,0;1.5708rad)
  Refine = true
  Size = 1.5
  Size2 = 1
  SupportTransform = false
  Suppressed = false
  UseAllEdges = false
FEATURE [PartDesign::CoordinateSystem] reactionWheel
  AttacherType = Attacher::AttachEngine3D
  AttachmentOffset = pos=(0,0,0) rot=(-0.57735,0.57735,-0.57735;2.0944rad)
  AttachmentSupport = -> [Chamfer001]
  MapMode = 11
  Placement = pos=(0,-12,5.3e-15) rot=(0,0,1;0rad)
FEATURE [PartDesign::Body] Body004  label="Body_ReactionWheel"
  AllowCompound = false
  Group = -> [Sketch015,Pad005,Sketch014,Pocket002,PolarPattern,Sketch013,Pad006,Sketch012,Pocket003,PolarPattern001,Sketch011,Pocket004,PolarPattern002,Sketch010,Pad007,PolarPattern003,Sketch009,Pocket005,Sketch008,Pocket006,reactionWheel,Chamfer001]
  Origin = -> Origin005
  Tip = -> Chamfer001
FEATURE [PartDesign::CoordinateSystem] Support
  AttacherType = Attacher::AttachEngine3D
  AttachmentOffset = pos=(0,0,0) rot=(-0.57735,0.57735,-0.57735;2.0944rad)
  AttachmentSupport = -> [Pocket]
  MapMode = 11
  Placement = pos=(0,-26.6,26) rot=(0,0,1;0rad)
FEATURE [App::Link] Body_Support  label="Body_Support001"
  AttachedBy = #Support
  AttachedTo = Parent Assembly#LCS_Origin
  Description = Pendulum
  LinkPlacement = pos=(0,26.6,-26) rot=(0,0,1;0rad)
  LinkedObject = -> Body
  Placement = pos=(0,26.6,-26) rot=(0,0,1;0rad)
  SolverId = Asm4EE
  expr: Placement = LCS_Origin.Placement * AttachmentOffset * Support.Placement ^ -1
FEATURE [App::Link] Body_Bearing  label="Body_Bearing001"
  AttachedBy = #Bearing_Axis
  AttachedTo = Body_Support#Support
  AttachmentOffset = pos=(0,-1,0) rot=(1,0,0;1.5708rad)
  LinkPlacement = pos=(-2.99e-14,2.5,-7.9e-15) rot=(1,0,0;1.5708rad)
  LinkedObject = -> Body002
  Placement = pos=(-2.99e-14,2.5,-7.9e-15) rot=(1,0,0;1.5708rad)
  SolverId = Asm4EE
  expr: Placement = Body_Support.Placement * Support.Placement * AttachmentOffset * Bearing_Axis.Placement ^ -1
FEATURE [PartDesign::CoordinateSystem] Rondelle001
  AttacherType = Attacher::AttachEngine3D
  AttachmentOffset = pos=(0,0,0) rot=(-0.57735,0.57735,-0.57735;2.0944rad)
  MapMode = 11
  Placement = pos=(0,-20.2,26) rot=(0,0,1;0rad)
FEATURE [PartDesign::Body] Body001  label="Body_Rondelle"
  AllowCompound = false
  Group = -> [Rondelle001]
  Origin = -> Origin007
FEATURE [App::Link] Body_Rondelle  label="Body_Rondelle001"
  AttachedBy = #Rondelle001
  AttachedTo = Body_Bearing#Bearing_Axis
  AttachmentOffset = pos=(0,0,0.5) rot=(1,0,0;1.5708rad)
  LinkPlacement = pos=(-3.38e-14,-21.7,26) rot=(1,0,0;3.14159rad)
  LinkedObject = -> Body001
  Placement = pos=(-3.38e-14,-21.7,26) rot=(1,0,0;3.14159rad)
  SolverId = Asm4EE
  expr: Placement = Body_Bearing.Placement * Bearing_Axis.Placement * AttachmentOffset * Rondelle001.Placement ^ -1
FEATURE [App::Link] Body_Arm  label="Body_Arm001"
  AttachedBy = #Arm_Axis_Bottom
  AttachedTo = Body_Bearing#Bearing_Axis
  AttachmentOffset = pos=(0,0,1) rot=(0,0,1;0rad)
  LinkPlacement = pos=(-1.37863e-06,6,84.8494) rot=(1,0,0;1.5708rad)
  LinkedObject = -> Body003
  Placement = pos=(-1.37863e-06,6,84.8494) rot=(1,0,0;1.5708rad)
  SolverId = Asm4EE
  expr: .AttachmentOffset.Rotation.Angle = Variables.arm_rotation
  expr: Placement = Body_Bearing.Placement * Bearing_Axis.Placement * AttachmentOffset * Arm_Axis_Bottom.Placement ^ -1
FEATURE [App::Link] Body_Motor  label="Body_Motor001"
  AttachedBy = #Motor
  AttachedTo = Body_Arm#Arm_Axis_Top
  AttachmentOffset = pos=(0,0,-2) rot=(1,0,0;4.71239rad)
  LinkPlacement = pos=(-2.75727e-06,34,169.699) rot=(0,0,1;0rad)
  LinkedObject = -> Body005
  Placement = pos=(-2.75727e-06,34,169.699) rot=(0,0,1;0rad)
  SolverId = Asm4EE
  expr: Placement = Body_Arm.Placement * Arm_Axis_Top.Placement * AttachmentOffset * Motor.Placement ^ -1
FEATURE [App::Link] Body_ReactionWheel  label="Body_ReactionWheel001"
  AttachedBy = #reactionWheel
  AttachedTo = Body_Motor#Motor_Shaft001
  AttachmentOffset = pos=(0,-13,0) rot=(0,0,1;0rad)
  LinkPlacement = pos=(-2.75727e-06,-9.9,169.699) rot=(0,0,1;0rad)
  LinkedObject = -> Body004
  Placement = pos=(-2.75727e-06,-9.9,169.699) rot=(0,0,1;0rad)
  SolverId = Asm4EE
  expr: Placement = Body_Motor.Placement * Motor_Shaft001.Placement * AttachmentOffset * reactionWheel.Placement ^ -1
FEATURE [PartDesign::CoordinateSystem] Motor_Shaft
  AttacherType = Attacher::AttachEngine3D
  AttachmentSupport = -> [Fillet002]
  MapMode = 11
  Placement = pos=(0,-42.9,9.5e-15) rot=(0.57735,-0.57735,0.57735;2.0944rad)
FEATURE [PartDesign::CoordinateSystem] Motor_Shaft001
  AttacherType = Attacher::AttachEngine3D
  AttachmentOffset = pos=(0,0,0) rot=(-0.57735,0.57735,-0.57735;2.0944rad)
  AttachmentSupport = -> [Fillet002]
  MapMode = 11
  Placement = pos=(0,-42.9,9.5e-15) rot=(0,0,1;0rad)
FEATURE [PartDesign::Body] Body005  label="Body_Motor"
  AllowCompound = false
  Group = -> [Sketch018,Pad008,Sketch019,Pad009,Sketch020,Pad010,Sketch021,Pad011,Sketch017,Pad012,PolarPattern004,Sketch022,Pocket007,PolarPattern005,Sketch016,Pad013,Sketch023,Pocket008,Fillet001,Fillet002,Motor,Motor_Shaft001]
  Origin = -> Origin006
  Tip = -> Fillet002
FEATURE [Sketcher::SketchObject] Sketch024
  ArcFitTolerance = 1e-06
  AttachmentSupport = -> [XZ_Plane008]
  FullyConstrained = true
  MakeInternals = false
  MapMode = 5
  Placement = pos=(0,0,0) rot=(1,0,0;1.5708rad)
  sketch-geometry (76):
    g0: LineSegment StartX=-8.94 StartY=-2.15 StartZ=0 EndX=-11.04 EndY=-2.15 EndZ=0
    g1: LineSegment StartX=-11.04 StartY=-2.15 StartZ=0 EndX=-11.04 EndY=-3.15 EndZ=0
    g2: LineSegment StartX=-11.04 StartY=-3.15 StartZ=0 EndX=-8.94 EndY=-3.15 EndZ=0
    g3: LineSegment StartX=-8.94 StartY=-3.15 StartZ=0 EndX=-8.94 EndY=-2.15 EndZ=0
    g4: LineSegment StartX=-8.94 StartY=-3.65 StartZ=0 EndX=-11.04 EndY=-3.65 EndZ=0
    g5: LineSegment StartX=-11.04 StartY=-3.65 StartZ=0 EndX=-11.04 EndY=-4.65 EndZ=0
    g6: LineSegment StartX=-11.04 StartY=-4.65 StartZ=0 EndX=-8.94 EndY=-4.65 EndZ=0
    g7: LineSegment StartX=-8.94 StartY=-4.65 StartZ=0 EndX=-8.94 EndY=-3.65 EndZ=0
    g8: LineSegment StartX=-8.94 StartY=-5.15 StartZ=0 EndX=-11.04 EndY=-5.15 EndZ=0
    g9: LineSegment StartX=-11.04 StartY=-5.15 StartZ=0 EndX=-11.04 EndY=-6.15 EndZ=0
    g10: LineSegment StartX=-11.04 StartY=-6.15 StartZ=0 EndX=-8.94 EndY=-6.15 EndZ=0
    g11: LineSegment StartX=-8.94 StartY=-6.15 StartZ=0 EndX=-8.94 EndY=-5.15 EndZ=0
    g12: LineSegment StartX=-5.34 StartY=-3.65 StartZ=0 EndX=-7.44 EndY=-3.65 EndZ=0
    g13: LineSegment StartX=-7.44 StartY=-3.65 StartZ=0 EndX=-7.44 EndY=-4.65 EndZ=0
    g14: LineSegment StartX=-7.44 StartY=-4.65 StartZ=0 EndX=-5.34 EndY=-4.65 EndZ=0
    g15: LineSegment StartX=-5.34 StartY=-4.65 StartZ=0 EndX=-5.34 EndY=-3.65 EndZ=0
    g16: LineSegment StartX=-5.34 StartY=-5.15 StartZ=0 EndX=-7.44 EndY=-5.15 EndZ=0
    g17: LineSegment StartX=-7.44 StartY=-5.15 StartZ=0 EndX=-7.44 EndY=-6.15 EndZ=0
    g18: LineSegment StartX=-7.44 StartY=-6.15 StartZ=0 EndX=-5.34 EndY=-6.15 EndZ=0
    g19: LineSegment StartX=-5.34 StartY=-6.15 StartZ=0 EndX=-5.34 EndY=-5.15 EndZ=0
    g20: LineSegment StartX=-1.68 StartY=-9.16 StartZ=0 EndX=-3.06 EndY=-9.16 EndZ=0
    g21: LineSegment StartX=-3.06 StartY=-9.16 StartZ=0 EndX=-3.06 EndY=-13.54 EndZ=0
    g22: LineSegment StartX=-3.06 StartY=-13.54 StartZ=0 EndX=-1.68 EndY=-13.54 EndZ=0
    g23: LineSegment StartX=-1.68 StartY=-13.54 StartZ=0 EndX=-1.68 EndY=-9.16 EndZ=0
    g24: LineSegment StartX=-4.18 StartY=-6.8 StartZ=0 EndX=-11.54 EndY=-6.8 EndZ=0
    g25: LineSegment StartX=-11.54 StartY=-6.8 StartZ=0 EndX=-11.54 EndY=-14.14 EndZ=0
    g26: LineSegment StartX=-11.54 StartY=-14.14 StartZ=0 EndX=-4.18 EndY=-14.14 EndZ=0
    g27: LineSegment StartX=-4.18 StartY=-14.14 StartZ=0 EndX=-4.18 EndY=-6.8 EndZ=0
    g28: LineSegment StartX=-4 StartY=-15.5 StartZ=0 EndX=-7.4 EndY=-15.5 EndZ=0
    g29: LineSegment StartX=-7.4 StartY=-15.5 StartZ=0 EndX=-7.4 EndY=-15.96 EndZ=0
    g30: LineSegment StartX=-7.4 StartY=-15.96 StartZ=0 EndX=-4 EndY=-15.96 EndZ=0
    g31: LineSegment StartX=-4 StartY=-15.96 StartZ=0 EndX=-4 EndY=-15.5 EndZ=0
    g32: LineSegment StartX=-8.9 StartY=-15.5 StartZ=0 EndX=-12.3 EndY=-15.5 EndZ=0
    g33: LineSegment StartX=-12.3 StartY=-15.5 StartZ=0 EndX=-12.3 EndY=-15.96 EndZ=0
    g34: LineSegment StartX=-12.3 StartY=-15.96 StartZ=0 EndX=-8.9 EndY=-15.96 EndZ=0
    g35: LineSegment StartX=-8.9 StartY=-15.96 StartZ=0 EndX=-8.9 EndY=-15.5 EndZ=0
    g36: LineSegment StartX=-8.9 StartY=-16.11 StartZ=0 EndX=-12.3 EndY=-16.11 EndZ=0
    g37: LineSegment StartX=-12.3 StartY=-16.11 StartZ=0 EndX=-12.3 EndY=-16.81 EndZ=0
    g38: LineSegment StartX=-12.3 StartY=-16.81 StartZ=0 EndX=-8.9 EndY=-16.81 EndZ=0
    g39: LineSegment StartX=-8.9 StartY=-16.81 StartZ=0 EndX=-8.9 EndY=-16.11 EndZ=0
    g40: LineSegment StartX=-4 StartY=-16.11 StartZ=0 EndX=-7.4 EndY=-16.11 EndZ=0
    g41: LineSegment StartX=-7.4 StartY=-16.11 StartZ=0 EndX=-7.4 EndY=-16.81 EndZ=0
    g42: LineSegment StartX=-7.4 StartY=-16.81 StartZ=0 EndX=-4 EndY=-16.81 EndZ=0
    g43: LineSegment StartX=-4 StartY=-16.81 StartZ=0 EndX=-4 EndY=-16.11 EndZ=0
    g44: LineSegment StartX=-4.78 StartY=-17.8 StartZ=0 EndX=-5.58 EndY=-17.8 EndZ=0
    g45: LineSegment StartX=-5.58 StartY=-17.8 StartZ=0 EndX=-5.58 EndY=-20.1 EndZ=0
    g46: LineSegment StartX=-5.58 StartY=-20.1 StartZ=0 EndX=-4.78 EndY=-20.1 EndZ=0
    g47: LineSegment StartX=-4.78 StartY=-20.1 StartZ=0 EndX=-4.78 EndY=-17.8 EndZ=0
    g48: LineSegment StartX=-10.88 StartY=-17.8 StartZ=0 EndX=-11.68 EndY=-17.8 EndZ=0
    g49: LineSegment StartX=-11.68 StartY=-17.8 StartZ=0 EndX=-11.68 EndY=-20.1 EndZ=0
    g50: LineSegment StartX=-11.68 StartY=-20.1 StartZ=0 EndX=-10.88 EndY=-20.1 EndZ=0
    g51: LineSegment StartX=-10.88 StartY=-20.1 StartZ=0 EndX=-10.88 EndY=-17.8 EndZ=0
    g52: LineSegment StartX=-6.28 StartY=-17.8 StartZ=0 EndX=-6.73 EndY=-17.8 EndZ=0
    g53: LineSegment StartX=-6.73 StartY=-18.12 StartZ=0 EndX=-6.28 EndY=-18.12 EndZ=0
    g54: LineSegment StartX=-6.28 StartY=-18.12 StartZ=0 EndX=-6.28 EndY=-17.8 EndZ=0
    g55: LineSegment StartX=-6.28 StartY=-19.72 StartZ=0 EndX=-6.73 EndY=-19.72 EndZ=0
    g56: LineSegment StartX=-6.73 StartY=-20.04 StartZ=0 EndX=-6.28 EndY=-20.04 EndZ=0
    g57: LineSegment StartX=-6.28 StartY=-20.04 StartZ=0 EndX=-6.28 EndY=-19.72 EndZ=0
    g58: LineSegment StartX=-9.17 StartY=-17.915 StartZ=0 EndX=-9.95 EndY=-17.915 EndZ=0
    g59: LineSegment StartX=-9.95 StartY=-17.915 StartZ=0 EndX=-9.95 EndY=-18.275 EndZ=0
    g60: LineSegment StartX=-9.95 StartY=-18.275 StartZ=0 EndX=-9.17 EndY=-18.275 EndZ=0
    g61: LineSegment StartX=-9.17 StartY=-18.74 StartZ=0 EndX=-9.95 EndY=-18.74 EndZ=0
    g62: LineSegment StartX=-9.95 StartY=-18.74 StartZ=0 EndX=-9.95 EndY=-19.1 EndZ=0
    g63: LineSegment StartX=-9.95 StartY=-19.1 StartZ=0 EndX=-9.17 EndY=-19.1 EndZ=0
    g64: LineSegment StartX=-9.17 StartY=-19.565 StartZ=0 EndX=-9.95 EndY=-19.565 EndZ=0
    g65: LineSegment StartX=-9.95 StartY=-19.565 StartZ=0 EndX=-9.95 EndY=-19.925 EndZ=0
    g66: LineSegment StartX=-9.95 StartY=-19.925 StartZ=0 EndX=-9.17 EndY=-19.925 EndZ=0
    g67: LineSegment StartX=-6.73 StartY=-17.45 StartZ=0 EndX=-9.17 EndY=-17.45 EndZ=0
    g68: LineSegment StartX=-9.17 StartY=-17.45 StartZ=0 EndX=-9.17 EndY=-17.915 EndZ=0
    g69: LineSegment StartX=-9.17 StartY=-20.39 StartZ=0 EndX=-6.73 EndY=-20.39 EndZ=0
    g70: LineSegment StartX=-6.73 StartY=-20.39 StartZ=0 EndX=-6.73 EndY=-20.04 EndZ=0
    g71: LineSegment StartX=-6.73 StartY=-17.8 StartZ=0 EndX=-6.73 EndY=-17.45 EndZ=0
    g72: LineSegment StartX=-6.73 StartY=-19.72 StartZ=0 EndX=-6.73 EndY=-18.12 EndZ=0
    g73: LineSegment StartX=-9.17 StartY=-18.275 StartZ=0 EndX=-9.17 EndY=-18.74 EndZ=0
    g74: LineSegment StartX=-9.17 StartY=-19.1 StartZ=0 EndX=-9.17 EndY=-19.565 EndZ=0
    g75: LineSegment StartX=-9.17 StartY=-19.925 StartZ=0 EndX=-9.17 EndY=-20.39 EndZ=0
  constraints (228):
    c: Coincident(g0,g1)
    c: Coincident(g1,g2)
    c: Coincident(g2,g3)
    c: Coincident(g3,g0)
    c: Horizontal(g0)
    c: Horizontal(g2)
    c: Vertical(g1)
    c: Vertical(g3)
    c: Coincident(g4,g5)
    c: Coincident(g5,g6)
    c: Coincident(g6,g7)
    c: Coincident(g7,g4)
    c: Horizontal(g4)
    c: Horizontal(g6)
    c: Vertical(g5)
    c: Vertical(g7)
    c: Coincident(g8,g9)
    c: Coincident(g9,g10)
    c: Coincident(g10,g11)
    c: Coincident(g11,g8)
    c: Horizontal(g8)
    c: Horizontal(g10)
    c: Vertical(g9)
    c: Vertical(g11)
    c: Coincident(g12,g13)
    c: Coincident(g13,g14)
    c: Coincident(g14,g15)
    c: Coincident(g15,g12)
    c: Horizontal(g12)
    c: Horizontal(g14)
    c: Vertical(g13)
    c: Vertical(g15)
    c: Coincident(g16,g17)
    c: Coincident(g17,g18)
    c: Coincident(g18,g19)
    c: Coincident(g19,g16)
    c: Horizontal(g16)
    c: Horizontal(g18)
    c: Vertical(g17)
    c: Vertical(g19)
    c: Coincident(g20,g21)
    c: Coincident(g21,g22)
    c: Coincident(g22,g23)
    c: Coincident(g23,g20)
    c: Horizontal(g20)
    c: Horizontal(g22)
    c: Vertical(g21)
    c: Vertical(g23)
    c: Coincident(g24,g25)
    c: Coincident(g25,g26)
    c: Coincident(g26,g27)
    c: Coincident(g27,g24)
    c: Horizontal(g24)
    c: Horizontal(g26)
    c: Vertical(g25)
    c: Vertical(g27)
    c: Coincident(g28,g29)
    c: Coincident(g29,g30)
    c: Coincident(g30,g31)
    c: Coincident(g31,g28)
    c: Horizontal(g28)
    c: Horizontal(g30)
    c: Vertical(g29)
    c: Vertical(g31)
    c: Coincident(g32,g33)
    c: Coincident(g33,g34)
    c: Coincident(g34,g35)
    c: Coincident(g35,g32)
    c: Horizontal(g32)
    c: Horizontal(g34)
    c: Vertical(g33)
    c: Vertical(g35)
    c: Coincident(g36,g37)
    c: Coincident(g37,g38)
    c: Coincident(g38,g39)
    c: Coincident(g39,g36)
    c: Horizontal(g36)
    c: Horizontal(g38)
    c: Vertical(g37)
    c: Vertical(g39)
    c: Coincident(g40,g41)
    c: Coincident(g41,g42)
    c: Coincident(g42,g43)
    c: Coincident(g43,g40)
    c: Horizontal(g40)
    c: Horizontal(g42)
    c: Vertical(g41)
    c: Vertical(g43)
    c: Coincident(g44,g45)
    c: Coincident(g45,g46)
    c: Coincident(g46,g47)
    c: Coincident(g47,g44)
    c: Horizontal(g44)
    c: Horizontal(g46)
    c: Vertical(g45)
    c: Vertical(g47)
    c: Coincident(g48,g49)
    c: Coincident(g49,g50)
    c: Coincident(g50,g51)
    c: Coincident(g51,g48)
    c: Horizontal(g48)
    c: Horizontal(g50)
    c: Vertical(g49)
    c: Vertical(g51)
    c: Coincident(g53,g54)
    c: Coincident(g54,g52)
    c: Horizontal(g52)
    c: Horizontal(g53)
    c: Vertical(g54)
    c: Coincident(g56,g57)
    c: Coincident(g57,g55)
    c: Horizontal(g55)
    c: Horizontal(g56)
    c: Vertical(g57)
    c: Coincident(g58,g59)
    c: Coincident(g59,g60)
    c: Horizontal(g58)
    c: Horizontal(g60)
    c: Vertical(g59)
    c: Coincident(g61,g62)
    c: Coincident(g62,g63)
    c: Horizontal(g61)
    c: Horizontal(g63)
    c: Vertical(g62)
    c: Coincident(g64,g65)
    c: Coincident(g65,g66)
    c: Horizontal(g64)
    c: Horizontal(g66)
    c: Vertical(g65)
    c: Coincident(g67,g68)
    c: Coincident(g75,g69)
    c: Coincident(g69,g70)
    c: Coincident(g71,g67)
    c: Horizontal(g67)
    c: Horizontal(g69)
    c: Vertical(g68)
    c: Vertical(g70)
    c: Equal(g0,g4)
    c: Equal(g4,g8)
    c: Equal(g8,g16)
    c: Equal(g16,g12)
    c: Equal(g19,g11)
    c: Equal(g11,g15)
    c: Equal(g15,g7)
    c: Equal(g7,g3)
    c: DistanceX(g0,g0) = 2.1
    c: DistanceY(g1,g1) = 1
    c: DistanceX(g0,g-1) = 8.94
    c: DistanceX(g4,g12) = 1.5
    c: DistanceY(g4,g1) = 0.5
    c: DistanceY(g8,g5) = 0.5
    c: PointOnObject(g17,g10)
    c: PointOnObject(g13,g6)
    c: PointOnObject(g13,g17)
    c: PointOnObject(g6,g11)
    c: DistanceY(g0,g-1) = 2.15
    c: PointOnObject(g4,g3)
    c: DistanceX(g24,g24) = 7.36
    c: DistanceY(g27,g27) = 7.34
    c: DistanceX(g24,g-1) = 4.18
    c: DistanceY(g24,g-1) = 6.8
    c: DistanceX(g20,g20) = 1.38
    c: DistanceY(g23,g23) = 4.38
    c: DistanceX(g20,g-1) = 1.68
    c: DistanceY(g20,g-1) = 9.16
    c: Equal(g28,g40)
    c: Equal(g40,g32)
    c: Equal(g32,g36)
    c: Equal(g29,g35)
    c: Equal(g43,g39)
    c: PointOnObject(g30,g43)
    c: PointOnObject(g34,g39)
    c: PointOnObject(g40,g36)
    c: PointOnObject(g29,g34)
    c: DistanceX(g28,g28) = 3.4
    c: DistanceY(g31,g31) = 0.46
    c: DistanceY(g40,g30) = 0.15
    c: DistanceY(g43,g43) = 0.7
    c: DistanceX(g32,g28) = 1.5
    c: DistanceX(g28,g-1) = 4
    c: DistanceY(g28,g-1) = 15.5
    c: Equal(g44,g48)
    c: Equal(g47,g51)
    c: PointOnObject(g44,g48)
    c: DistanceX(g46,g46) = 0.8
    c: DistanceY(g47,g47) = 2.3
    c: DistanceX(g46,g-1) = 4.78
    c: DistanceY(g44,g-1) = 17.8
    c: DistanceX(g50,g45) = 5.3
    c: Coincident(g72,g55)
    c: Coincident(g56,g70)
    c: Vertical(g72)
    c: PointOnObject(g56,g72)
    c: Vertical(g71)
    c: Coincident(g72,g53)
    c: Coincident(g52,g71)
    c: Coincident(g58,g68)
    c: Coincident(g73,g60)
    c: Coincident(g61,g73)
    c: Coincident(g74,g63)
    c: Coincident(g64,g74)
    c: Coincident(g66,g75)
    c: Vertical(g74)
    c: Vertical(g75)
    c: PointOnObject(g58,g73)
    c: Vertical(g73)
    c: PointOnObject(g61,g74)
    c: PointOnObject(g64,g75)
    c: Equal(g58,g61)
    c: Equal(g61,g64)
    c: Equal(g59,g62)
    c: Equal(g62,g65)
    c: Equal(g52,g55)
    c: Equal(g54,g57)
    c: Equal(g71,g70)
    c: Equal(g68,g73)
    c: Equal(g73,g74)
    c: Equal(g74,g75)
    c: DistanceY(g71,g71) = 0.35
    c: DistanceY(g54,g54) = 0.32
    c: PointOnObject(g52,g72)
    c: DistanceX(g52,g52) = 0.45
    c: DistanceX(g53,g44) = 0.7
    c: DistanceY(g72,g72) = 1.6
    c: PointOnObject(g52,g44)
    c: DistanceX(g67,g67) = 2.44
    c: DistanceX(g58,g58) = 0.78
    c: DistanceY(g59,g59) = 0.36
FEATURE [Sketcher::SketchObject] Sketch025
  ArcFitTolerance = 1e-06
  AttachmentSupport = -> [XZ_Plane008]
  FullyConstrained = true
  MakeInternals = false
  MapMode = 5
  Placement = pos=(0,0,0) rot=(1,0,0;1.5708rad)
  sketch-geometry (15):
    g0: LineSegment StartX=0 StartY=0 StartZ=0 EndX=-15.75 EndY=0 EndZ=0
    g1: LineSegment StartX=-15.75 StartY=0 StartZ=0 EndX=-15.75 EndY=-21.11 EndZ=0
    g2: LineSegment StartX=-15.75 StartY=-21.11 StartZ=0 EndX=0 EndY=-21.11 EndZ=0
    g3: LineSegment StartX=0 StartY=-21.11 StartZ=0 EndX=0 EndY=0 EndZ=0
    g4: Circle CenterX=-2.775 CenterY=-2.775 CenterZ=0 NormalX=0 NormalY=0 NormalZ=1 AngleXU=0 Radius=1.56
    g5: Circle CenterX=-2.775 CenterY=-18.335 CenterZ=0 NormalX=0 NormalY=0 NormalZ=1 AngleXU=0 Radius=1.56
    g6: Circle CenterX=-14.19 CenterY=-2.39 CenterZ=0 NormalX=0 NormalY=0 NormalZ=1 AngleXU=0 Radius=1.05
    g7: Circle CenterX=-14.19 CenterY=-4.73 CenterZ=0 NormalX=0 NormalY=0 NormalZ=1 AngleXU=0 Radius=1.05
    g8: Circle CenterX=-14.19 CenterY=-7.07 CenterZ=0 NormalX=0 NormalY=0 NormalZ=1 AngleXU=0 Radius=1.05
    g9: Circle CenterX=-14.19 CenterY=-9.41 CenterZ=0 NormalX=0 NormalY=0 NormalZ=1 AngleXU=0 Radius=1.05
    g10: Circle CenterX=-14.19 CenterY=-11.75 CenterZ=0 NormalX=0 NormalY=0 NormalZ=1 AngleXU=0 Radius=1.05
    g11: Circle CenterX=-14.19 CenterY=-14.09 CenterZ=0 NormalX=0 NormalY=0 NormalZ=1 AngleXU=0 Radius=1.05
    g12: Circle CenterX=-14.19 CenterY=-16.43 CenterZ=0 NormalX=0 NormalY=0 NormalZ=1 AngleXU=0 Radius=1.05
    g13: Circle CenterX=-14.19 CenterY=-18.77 CenterZ=0 NormalX=0 NormalY=0 NormalZ=1 AngleXU=0 Radius=1.05
    g14: LineSegment [constr] StartX=-14.19 StartY=0 StartZ=0 EndX=-14.19 EndY=-21.11 EndZ=0
  constraints (45):
    c: Coincident(g0,g1)
    c: Coincident(g1,g2)
    c: Coincident(g2,g3)
    c: Coincident(g3,g0)
    c: Horizontal(g0)
    c: Horizontal(g2)
    c: Vertical(g1)
    c: Vertical(g3)
    c: Coincident(g0,g-1)
    c: DistanceX(g2,g2) = 15.75
    c: DistanceY(g1,g1) = 21.11
    c: Equal(g5,g4)
    c: DistanceY(g5,g4) = 15.56
    c: Diameter(g4) = 3.12
    c: DistanceY(g4,g0) = 2.775
    c: DistanceX(g4,g0) = 2.775
    c: DistanceX(g5,g2) = 2.775
    c: Diameter(g6) = 2.1
    c: Equal(g6,g7)
    c: Equal(g7,g8)
    c: Equal(g8,g9)
    c: Equal(g9,g10)
    c: Equal(g10,g11)
    c: Equal(g11,g12)
    c: Equal(g12,g13)
    c: PointOnObject(g14,g0)
    c: PointOnObject(g14,g2)
    c: Vertical(g14)
    c: DistanceX(g0,g14) = 1.56
    c: PointOnObject(g6,g14)
    c: PointOnObject(g7,g14)
    c: PointOnObject(g8,g14)
    c: PointOnObject(g9,g14)
    c: PointOnObject(g10,g14)
    c: PointOnObject(g12,g14)
    c: PointOnObject(g11,g14)
    c: PointOnObject(g13,g14)
    c: DistanceY(g7,g6) = 2.34
    c: DistanceY(g8,g7) = 2.34
    c: DistanceY(g9,g8) = 2.34
    c: DistanceY(g10,g9) = 2.34
    c: DistanceY(g11,g10) = 2.34
    c: DistanceY(g12,g11) = 2.34
    c: DistanceY(g13,g12) = 2.34
    c: DistanceY(g6,g0) = 2.39
FEATURE [PartDesign::Pad] Pad014  label="Pad_Plate"
  Direction = (0,-1,2e-16)
  Length = 1
  Length2 = 10
  Placement = pos=(0,0,0) rot=(1,0,0;1.5708rad)
  Profile = -> Sketch025
  ReferenceAxis = -> Sketch025 [N_Axis]
  Refine = true
  Suppressed = false
  Type = 0
FEATURE [PartDesign::Pad] Pad015  label="Pad_Circuit1"
  BaseFeature = -> Pad014
  Direction = (0,-1,2e-16)
  Length = 0.5
  Length2 = 10
  Placement = pos=(0,0,0) rot=(1,0,0;1.5708rad)
  Profile = -> Sketch024
  ReferenceAxis = -> Sketch024 [N_Axis]
  Refine = true
  Reversed = true
  Suppressed = false
  Type = 0
FEATURE [Sketcher::SketchObject] Sketch026
  ArcFitTolerance = 1e-06
  AttachmentOffset = pos=(0,0,-0.5) rot=(0,0,1;0rad)
  AttachmentSupport = -> [XZ_Plane008]
  ExternalGeometry = -> [Pad015]
  FullyConstrained = true
  MakeInternals = false
  MapMode = 5
  Placement = pos=(0,0.5,-1e-16) rot=(1,0,0;1.5708rad)
  sketch-geometry (56):
    g0: LineSegment StartX=-9.44 StartY=-2.15 StartZ=0 EndX=-10.44 EndY=-2.15 EndZ=0
    g1: LineSegment StartX=-10.44 StartY=-2.15 StartZ=0 EndX=-10.44 EndY=-3.15 EndZ=0
    g2: LineSegment StartX=-10.44 StartY=-3.15 StartZ=0 EndX=-9.44 EndY=-3.15 EndZ=0
    g3: LineSegment StartX=-9.44 StartY=-3.15 StartZ=0 EndX=-9.44 EndY=-2.15 EndZ=0
    g4: LineSegment StartX=-5.84 StartY=-3.65 StartZ=0 EndX=-6.84 EndY=-3.65 EndZ=0
    g5: LineSegment StartX=-6.84 StartY=-3.65 StartZ=0 EndX=-6.84 EndY=-4.65 EndZ=0
    g6: LineSegment StartX=-6.84 StartY=-4.65 StartZ=0 EndX=-5.84 EndY=-4.65 EndZ=0
    g7: LineSegment StartX=-5.84 StartY=-4.65 StartZ=0 EndX=-5.84 EndY=-3.65 EndZ=0
    g8: LineSegment StartX=-9.44 StartY=-3.65 StartZ=0 EndX=-10.44 EndY=-3.65 EndZ=0
    g9: LineSegment StartX=-10.44 StartY=-3.65 StartZ=0 EndX=-10.44 EndY=-4.65 EndZ=0
    g10: LineSegment StartX=-10.44 StartY=-4.65 StartZ=0 EndX=-9.44 EndY=-4.65 EndZ=0
    g11: LineSegment StartX=-9.44 StartY=-4.65 StartZ=0 EndX=-9.44 EndY=-3.65 EndZ=0
    g12: LineSegment StartX=-9.44 StartY=-5.15 StartZ=0 EndX=-10.44 EndY=-5.15 EndZ=0
    g13: LineSegment StartX=-10.44 StartY=-5.15 StartZ=0 EndX=-10.44 EndY=-6.15 EndZ=0
    g14: LineSegment StartX=-10.44 StartY=-6.15 StartZ=0 EndX=-9.44 EndY=-6.15 EndZ=0
    g15: LineSegment StartX=-9.44 StartY=-6.15 StartZ=0 EndX=-9.44 EndY=-5.15 EndZ=0
    g16: LineSegment StartX=-5.84 StartY=-5.15 StartZ=0 EndX=-6.84 EndY=-5.15 EndZ=0
    g17: LineSegment StartX=-6.84 StartY=-5.15 StartZ=0 EndX=-6.84 EndY=-6.15 EndZ=0
    g18: LineSegment StartX=-6.84 StartY=-6.15 StartZ=0 EndX=-5.84 EndY=-6.15 EndZ=0
    g19: LineSegment StartX=-5.84 StartY=-6.15 StartZ=0 EndX=-5.84 EndY=-5.15 EndZ=0
    g20: LineSegment StartX=-1.68 StartY=-9.96 StartZ=0 EndX=-3.06 EndY=-9.96 EndZ=0
    g21: LineSegment StartX=-3.06 StartY=-9.96 StartZ=0 EndX=-3.06 EndY=-12.74 EndZ=0
    g22: LineSegment StartX=-3.06 StartY=-12.74 StartZ=0 EndX=-1.68 EndY=-12.74 EndZ=0
    g23: LineSegment StartX=-1.68 StartY=-12.74 StartZ=0 EndX=-1.68 EndY=-9.96 EndZ=0
    g24: LineSegment StartX=-4.82 StartY=-7.44 StartZ=0 EndX=-10.9 EndY=-7.44 EndZ=0
    g25: LineSegment StartX=-10.9 StartY=-7.44 StartZ=0 EndX=-10.9 EndY=-13.5 EndZ=0
    g26: LineSegment StartX=-10.9 StartY=-13.5 StartZ=0 EndX=-4.82 EndY=-13.5 EndZ=0
    g27: LineSegment StartX=-4.82 StartY=-13.5 StartZ=0 EndX=-4.82 EndY=-7.44 EndZ=0
    g28: LineSegment StartX=-4.8 StartY=-15.5 StartZ=0 EndX=-6.6 EndY=-15.5 EndZ=0
    g29: LineSegment StartX=-6.6 StartY=-15.5 StartZ=0 EndX=-6.6 EndY=-15.96 EndZ=0
    g30: LineSegment StartX=-6.6 StartY=-15.96 StartZ=0 EndX=-4.8 EndY=-15.96 EndZ=0
    g31: LineSegment StartX=-4.8 StartY=-15.96 StartZ=0 EndX=-4.8 EndY=-15.5 EndZ=0
    g32: LineSegment StartX=-4.8 StartY=-16.11 StartZ=0 EndX=-6.6 EndY=-16.11 EndZ=0
    g33: LineSegment StartX=-6.6 StartY=-16.11 StartZ=0 EndX=-6.6 EndY=-16.81 EndZ=0
    g34: LineSegment StartX=-6.6 StartY=-16.81 StartZ=0 EndX=-4.8 EndY=-16.81 EndZ=0
    g35: LineSegment StartX=-4.8 StartY=-16.81 StartZ=0 EndX=-4.8 EndY=-16.11 EndZ=0
    g36: LineSegment StartX=-9.5 StartY=-15.5 StartZ=0 EndX=-11.7 EndY=-15.5 EndZ=0
    g37: LineSegment StartX=-11.7 StartY=-15.5 StartZ=0 EndX=-11.7 EndY=-15.96 EndZ=0
    g38: LineSegment StartX=-11.7 StartY=-15.96 StartZ=0 EndX=-9.5 EndY=-15.96 EndZ=0
    g39: LineSegment StartX=-9.5 StartY=-15.96 StartZ=0 EndX=-9.5 EndY=-15.5 EndZ=0
    g40: LineSegment StartX=-9.5 StartY=-16.11 StartZ=0 EndX=-11.7 EndY=-16.11 EndZ=0
    g41: LineSegment StartX=-11.7 StartY=-16.11 StartZ=0 EndX=-11.7 EndY=-16.81 EndZ=0
    g42: LineSegment StartX=-11.7 StartY=-16.81 StartZ=0 EndX=-9.5 EndY=-16.81 EndZ=0
    g43: LineSegment StartX=-9.5 StartY=-16.81 StartZ=0 EndX=-9.5 EndY=-16.11 EndZ=0
    g44: LineSegment StartX=-4.78 StartY=-18.4 StartZ=0 EndX=-5.58 EndY=-18.4 EndZ=0
    g45: LineSegment StartX=-5.58 StartY=-18.4 StartZ=0 EndX=-5.58 EndY=-19.5 EndZ=0
    g46: LineSegment StartX=-5.58 StartY=-19.5 StartZ=0 EndX=-4.78 EndY=-19.5 EndZ=0
    g47: LineSegment StartX=-4.78 StartY=-19.5 StartZ=0 EndX=-4.78 EndY=-18.4 EndZ=0
    g48: LineSegment StartX=-6.98 StartY=-17.7 StartZ=0 EndX=-8.92 EndY=-17.7 EndZ=0
    g49: LineSegment StartX=-8.92 StartY=-17.7 StartZ=0 EndX=-8.92 EndY=-20.14 EndZ=0
    g50: LineSegment StartX=-8.92 StartY=-20.14 StartZ=0 EndX=-6.98 EndY=-20.14 EndZ=0
    g51: LineSegment StartX=-6.98 StartY=-20.14 StartZ=0 EndX=-6.98 EndY=-17.7 EndZ=0
    g52: LineSegment StartX=-10.88 StartY=-18.4 StartZ=0 EndX=-11.68 EndY=-18.4 EndZ=0
    g53: LineSegment StartX=-11.68 StartY=-18.4 StartZ=0 EndX=-11.68 EndY=-19.5 EndZ=0
    g54: LineSegment StartX=-11.68 StartY=-19.5 StartZ=0 EndX=-10.88 EndY=-19.5 EndZ=0
    g55: LineSegment StartX=-10.88 StartY=-19.5 StartZ=0 EndX=-10.88 EndY=-18.4 EndZ=0
  constraints (168):
    c: Coincident(g0,g1)
    c: Coincident(g1,g2)
    c: Coincident(g2,g3)
    c: Coincident(g3,g0)
    c: Horizontal(g0)
    c: Horizontal(g2)
    c: Vertical(g1)
    c: Vertical(g3)
    c: Coincident(g4,g5)
    c: Coincident(g5,g6)
    c: Coincident(g6,g7)
    c: Coincident(g7,g4)
    c: Horizontal(g4)
    c: Horizontal(g6)
    c: Vertical(g5)
    c: Vertical(g7)
    c: Coincident(g8,g9)
    c: Coincident(g9,g10)
    c: Coincident(g10,g11)
    c: Coincident(g11,g8)
    c: Horizontal(g8)
    c: Horizontal(g10)
    c: Vertical(g9)
    c: Vertical(g11)
    c: Coincident(g12,g13)
    c: Coincident(g13,g14)
    c: Coincident(g14,g15)
    c: Coincident(g15,g12)
    c: Horizontal(g12)
    c: Horizontal(g14)
    c: Vertical(g13)
    c: Vertical(g15)
    c: Coincident(g16,g17)
    c: Coincident(g17,g18)
    c: Coincident(g18,g19)
    c: Coincident(g19,g16)
    c: Horizontal(g16)
    c: Horizontal(g18)
    c: Vertical(g17)
    c: Vertical(g19)
    c: Coincident(g20,g21)
    c: Coincident(g21,g22)
    c: Coincident(g22,g23)
    c: Coincident(g23,g20)
    c: Horizontal(g20)
    c: Horizontal(g22)
    c: Vertical(g21)
    c: Vertical(g23)
    c: Coincident(g24,g25)
    c: Coincident(g25,g26)
    c: Coincident(g26,g27)
    c: Coincident(g27,g24)
    c: Horizontal(g24)
    c: Horizontal(g26)
    c: Vertical(g25)
    c: Vertical(g27)
    c: Coincident(g28,g29)
    c: Coincident(g29,g30)
    c: Coincident(g30,g31)
    c: Coincident(g31,g28)
    c: Horizontal(g28)
    c: Horizontal(g30)
    c: Vertical(g29)
    c: Vertical(g31)
    c: Coincident(g32,g33)
    c: Coincident(g33,g34)
    c: Coincident(g34,g35)
    c: Coincident(g35,g32)
    c: Horizontal(g32)
    c: Horizontal(g34)
    c: Vertical(g33)
    c: Vertical(g35)
    c: Coincident(g36,g37)
    c: Coincident(g37,g38)
    c: Coincident(g38,g39)
    c: Coincident(g39,g36)
    c: Horizontal(g36)
    c: Horizontal(g38)
    c: Vertical(g37)
    c: Vertical(g39)
    c: Coincident(g40,g41)
    c: Coincident(g41,g42)
    c: Coincident(g42,g43)
    c: Coincident(g43,g40)
    c: Horizontal(g40)
    c: Horizontal(g42)
    c: Vertical(g41)
    c: Vertical(g43)
    c: Coincident(g44,g45)
    c: Coincident(g45,g46)
    c: Coincident(g46,g47)
    c: Coincident(g47,g44)
    c: Horizontal(g44)
    c: Horizontal(g46)
    c: Vertical(g45)
    c: Vertical(g47)
    c: Coincident(g48,g49)
    c: Coincident(g49,g50)
    c: Coincident(g50,g51)
    c: Coincident(g51,g48)
    c: Horizontal(g48)
    c: Horizontal(g50)
    c: Vertical(g49)
    c: Vertical(g51)
    c: Coincident(g52,g53)
    c: Coincident(g53,g54)
    c: Coincident(g54,g55)
    c: Coincident(g55,g52)
    c: Horizontal(g52)
    c: Horizontal(g54)
    c: Vertical(g53)
    c: Vertical(g55)
    c: Equal(g0,g3)
    c: Equal(g3,g4)
    c: Equal(g4,g7)
    c: Equal(g7,g16)
    c: Equal(g16,g19)
    c: Equal(g19,g12)
    c: Equal(g12,g15)
    c: Equal(g15,g8)
    c: Equal(g8,g11)
    c: PointOnObject(g0,g-3)
    c: PointOnObject(g2,g-4)
    c: DistanceX(g-4,g1) = 0.6
    c: PointOnObject(g8,g-5)
    c: PointOnObject(g1,g9)
    c: PointOnObject(g12,g-6)
    c: PointOnObject(g9,g13)
    c: PointOnObject(g5,g17)
    c: PointOnObject(g4,g8)
    c: PointOnObject(g16,g12)
    c: DistanceX(g-7,g4) = 0.6
    c: DistanceX(g-8,g24) = 0.64
    c: DistanceY(g24,g-8) = 0.64
    c: DistanceX(g26,g-9) = 0.64
    c: DistanceY(g-9,g26) = 0.64
    c: PointOnObject(g20,g-11)
    c: PointOnObject(g20,g-10)
    c: DistanceY(g20,g-10) = 0.8
    c: DistanceY(g-10,g21) = 0.8
    c: DistanceX(g50,g-25) = 0.25
    c: DistanceY(g-25,g50) = 0.25
    c: DistanceY(g48,g-24) = 0.25
    c: DistanceX(g-24,g48) = 0.25
    c: PointOnObject(g28,g-12)
    c: PointOnObject(g29,g-13)
    c: DistanceX(g-12,g28) = 0.8
    c: DistanceX(g28,g-12) = 0.8
    c: PointOnObject(g32,g-14)
    c: PointOnObject(g33,g-15)
    c: PointOnObject(g29,g33)
    c: PointOnObject(g30,g35)
    c: PointOnObject(g36,g-16)
    c: PointOnObject(g37,g-17)
    c: DistanceX(g-16,g36) = 0.6
    c: DistanceX(g36,g-16) = 0.6
    c: PointOnObject(g40,g-18)
    c: PointOnObject(g41,g-19)
    c: PointOnObject(g37,g41)
    c: PointOnObject(g38,g43)
    c: PointOnObject(g52,g-23)
    c: PointOnObject(g54,g-22)
    c: DistanceY(g52,g-22) = 0.6
    c: DistanceY(g-23,g53) = 0.6
    c: PointOnObject(g44,g-20)
    c: PointOnObject(g46,g-21)
    c: PointOnObject(g44,g52)
    c: PointOnObject(g45,g54)
FEATURE [PartDesign::Pad] Pad016  label="Pad_Circuit2"
  BaseFeature = -> Pad015
  Direction = (0,-1,2e-16)
  Length = 1
  Length2 = 10
  Midplane = true
  Placement = pos=(0,0,0) rot=(1,0,0;1.5708rad)
  Profile = -> Sketch026
  ReferenceAxis = -> Sketch026 [N_Axis]
  Refine = true
  Suppressed = false
  Type = 0
FEATURE [PartDesign::CoordinateSystem] MPU6050
  AttacherType = Attacher::AttachEngine3D
  AttachmentOffset = pos=(0,0,0) rot=(-0.57735,0.57735,-0.57735;2.0944rad)
  AttachmentSupport = -> [Pad016]
  MapMode = 11
  Placement = pos=(-2.775,0,-2.775) rot=(0,0,1;0rad)
FEATURE [PartDesign::Body] Body006  label="Body_MPU6050"
  AllowCompound = false
  Group = -> [Sketch025,Pad014,Sketch024,Pad015,Sketch026,Pad016,MPU6050]
  Origin = -> Origin008
  Tip = -> Pad016
FEATURE [App::Link] Body_MPU6050  label="Body_MPU6051"
  AttachedBy = #MPU6050
  AttachedTo = Body_Arm#Arm_MPU6050_Right
  AttachmentOffset = pos=(0,1,0) rot=(0,0,1;0rad)
  LinkPlacement = pos=(-10.555,7,60.6244) rot=(0,-1,0;1.5708rad)
  LinkedObject = -> Body006
  Placement = pos=(-10.555,7,60.6244) rot=(0,-1,0;1.5708rad)
  SolverId = Asm4EE
  expr: Placement = Body_Arm.Placement * Arm_MPU6050_Right.Placement * AttachmentOffset * MPU6050.Placement ^ -1
FEATURE [PartDesign::CoordinateSystem] Arm_MPU6050_Right
  AttacherType = Attacher::AttachEngine3D
  AttachmentOffset = pos=(0,0,0) rot=(-1,0,0;1.5708rad)
  AttachmentSupport = -> [Pocket001]
  MapMode = 11
  Placement = pos=(-7.78,-27,0) rot=(-0.57735,-0.57735,0.57735;2.0944rad)
FEATURE [PartDesign::Chamfer] Chamfer002
  Angle = 45
  Base = -> Pocket001 [Edge42,Edge41]
  BaseFeature = -> Pocket001
  ChamferType = 0
  FlipDirection = false
  Refine = true
  Size = 1.5
  Size2 = 1
  SupportTransform = false
  Suppressed = false
  UseAllEdges = false
FEATURE [Part::FeaturePython] Screw  label="M3x6-Screw1077"  # WARN: FeaturePython — macro-defined, semantics opaque (R4)
  BaseObject = -> Body_Arm [Chamfer002.Edge24]
  Diameter = 1
  Invert = false
  LeftHanded = false
  Length = 0
  LengthCustom = 6
  MatchOuter = false
  OffsetAngle = 0
  Placement = pos=(-3.00099e-06,-2,184.699) rot=(1,0,0;1.5708rad)
  Thread = false
  Type = 85
FEATURE [Part::FeaturePython] Screw001  label="M3x6-Screw1078"  # WARN: FeaturePython — macro-defined, semantics opaque (R4)
  BaseObject = -> Body_Arm [Chamfer002.Edge17]
  Diameter = 1
  Invert = false
  LeftHanded = false
  Length = 0
  LengthCustom = 6
  MatchOuter = false
  OffsetAngle = 0
  Placement = pos=(-12.9904,-2,162.199) rot=(1,0,0;1.5708rad)
  Thread = false
  Type = 85
FEATURE [Part::FeaturePython] Screw002  label="M3x6-Screw"  # WARN: FeaturePython — macro-defined, semantics opaque (R4)
  BaseObject = -> Body_Arm [Chamfer002.Edge18]
  Diameter = 1
  Invert = false
  LeftHanded = false
  Length = 0
  LengthCustom = 6
  MatchOuter = false
  OffsetAngle = 0
  Placement = pos=(12.9904,-2,162.199) rot=(1,0,0;1.5708rad)
  Thread = false
  Type = 85
FEATURE [Part::FeaturePython] Screw003  label="M3x12-Screw"  # WARN: FeaturePython — macro-defined, semantics opaque (R4)
  BaseObject = -> Body_Arm [Chamfer002.Edge1]
  Diameter = 1
  Invert = false
  LeftHanded = false
  Length = 3
  LengthCustom = 12
  MatchOuter = false
  OffsetAngle = 0
  Placement = pos=(-7.78,-2,57.8494) rot=(1,0,0;1.5708rad)
  Thread = false
  Type = 85
FEATURE [Part::FeaturePython] Screw004  label="M3x12-Screw001"  # WARN: FeaturePython — macro-defined, semantics opaque (R4)
  BaseObject = -> Body_Arm [Chamfer002.Edge25]
  Diameter = 1
  Invert = false
  LeftHanded = false
  Length = 3
  LengthCustom = 12
  MatchOuter = false
  OffsetAngle = 0
  Placement = pos=(7.78,-2,57.8494) rot=(1,0,0;1.5708rad)
  Thread = false
  Type = 85
FEATURE [Part::FeaturePython] Nut  label="M3-Nut997"  # WARN: FeaturePython — macro-defined, semantics opaque (R4)
  BaseObject = -> Screw004 [Edge27]
  Diameter = 4
  Invert = false
  LeftHanded = false
  MatchOuter = false
  OffsetAngle = 0
  Placement = pos=(7.78,9.7,57.8494) rot=(1,0,0;1.5708rad)
  Thread = false
  Type = 31
FEATURE [Part::FeaturePython] Nut003  label="M3-Nut998"  # WARN: FeaturePython — macro-defined, semantics opaque (R4)
  BaseObject = -> Screw003 [Edge27]
  Diameter = 4
  Invert = false
  LeftHanded = false
  MatchOuter = false
  OffsetAngle = 0
  Placement = pos=(-7.78,9.7,57.8494) rot=(1,0,0;1.5708rad)
  Thread = false
  Type = 31
FEATURE [Part::FeaturePython] Screw006  label="M4x12-Screw"  # WARN: FeaturePython — macro-defined, semantics opaque (R4)
  BaseObject = -> Body_ReactionWheel [Chamfer001.Edge406]
  Diameter = 5
  Invert = true
  LeftHanded = false
  Length = 2
  LengthCustom = 12
  MatchOuter = false
  Offset = 2
  OffsetAngle = 0
  Placement = pos=(19.8995,-9.4,217.74) rot=(-1,0,0;1.5708rad)
  Thread = false
  Type = 55
FEATURE [Part::FeaturePython] Screw007  label="M4x12-Screw001"  # WARN: FeaturePython — macro-defined, semantics opaque (R4)
  BaseObject = -> Body_ReactionWheel [Chamfer001.Edge402]
  Diameter = 5
  Invert = true
  LeftHanded = false
  Length = 2
  LengthCustom = 12
  MatchOuter = false
  Offset = 2
  OffsetAngle = 0
  Placement = pos=(-3.60216e-06,-9.4,221.699) rot=(-1,0,0;1.5708rad)
  Thread = false
  Type = 55
FEATURE [Part::FeaturePython] Screw008  label="M4x12-Screw002"  # WARN: FeaturePython — macro-defined, semantics opaque (R4)
  BaseObject = -> Body_ReactionWheel [Chamfer001.Edge398]
  Diameter = 5
  Invert = true
  LeftHanded = false
  Length = 2
  LengthCustom = 12
  MatchOuter = false
  Offset = 2
  OffsetAngle = 0
  Placement = pos=(-19.8995,-9.4,217.74) rot=(-1,0,0;1.5708rad)
  Thread = false
  Type = 55
FEATURE [Part::FeaturePython] Screw009  label="M4x12-Screw003"  # WARN: FeaturePython — macro-defined, semantics opaque (R4)
  BaseObject = -> Body_ReactionWheel [Chamfer001.Edge430]
  Diameter = 5
  Invert = true
  LeftHanded = false
  Length = 2
  LengthCustom = 12
  MatchOuter = false
  Offset = 2
  OffsetAngle = 0
  Placement = pos=(19.8995,-9.4,121.657) rot=(-1,0,0;1.5708rad)
  Thread = false
  Type = 55
FEATURE [Part::FeaturePython] Screw010  label="M4x12-Screw004"  # WARN: FeaturePython — macro-defined, semantics opaque (R4)
  BaseObject = -> Body_ReactionWheel [Chamfer001.Edge434]
  Diameter = 5
  Invert = true
  LeftHanded = false
  Length = 2
  LengthCustom = 12
  MatchOuter = false
  Offset = 2
  OffsetAngle = 0
  Placement = pos=(-1.91237e-06,-9.4,117.699) rot=(-1,0,0;1.5708rad)
  Thread = false
  Type = 55
FEATURE [Part::FeaturePython] Screw011  label="M4x12-Screw005"  # WARN: FeaturePython — macro-defined, semantics opaque (R4)
  BaseObject = -> Body_ReactionWheel [Chamfer001.Edge438]
  Diameter = 5
  Invert = true
  LeftHanded = false
  Length = 2
  LengthCustom = 12
  MatchOuter = false
  Offset = 2
  OffsetAngle = 0
  Placement = pos=(-19.8995,-9.4,121.657) rot=(-1,0,0;1.5708rad)
  Thread = false
  Type = 55
FEATURE [Part::FeaturePython] Screw012  label="M4x12-Screw006"  # WARN: FeaturePython — macro-defined, semantics opaque (R4)
  BaseObject = -> Body_ReactionWheel [Chamfer001.Edge446]
  Diameter = 5
  Invert = true
  LeftHanded = false
  Length = 2
  LengthCustom = 12
  MatchOuter = false
  Offset = 2
  OffsetAngle = 0
  Placement = pos=(-48.0417,-9.4,149.799) rot=(-1,0,0;1.5708rad)
  Thread = false
  Type = 55
FEATURE [Part::FeaturePython] Screw013  label="M4x12-Screw007"  # WARN: FeaturePython — macro-defined, semantics opaque (R4)
  BaseObject = -> Body_ReactionWheel [Chamfer001.Edge130]
  Diameter = 5
  Invert = true
  LeftHanded = false
  Length = 2
  LengthCustom = 12
  MatchOuter = false
  Offset = 2
  OffsetAngle = 0
  Placement = pos=(-48.0417,-9.4,189.598) rot=(-1,0,0;1.5708rad)
  Thread = false
  Type = 55
FEATURE [Part::FeaturePython] Screw014  label="M4x12-Screw008"  # WARN: FeaturePython — macro-defined, semantics opaque (R4)
  BaseObject = -> Body_ReactionWheel [Chamfer001.Edge414]
  Diameter = 5
  Invert = true
  LeftHanded = false
  Length = 2
  LengthCustom = 12
  MatchOuter = false
  Offset = 2
  OffsetAngle = 0
  Placement = pos=(48.0417,-9.4,189.598) rot=(-1,0,0;1.5708rad)
  Thread = false
  Type = 55
FEATURE [Part::FeaturePython] Screw015  label="M4x12-Screw009"  # WARN: FeaturePython — macro-defined, semantics opaque (R4)
  BaseObject = -> Body_ReactionWheel [Chamfer001.Edge422]
  Diameter = 5
  Invert = true
  LeftHanded = false
  Length = 2
  LengthCustom = 12
  MatchOuter = false
  Offset = 2
  OffsetAngle = 0
  Placement = pos=(48.0417,-9.4,149.799) rot=(-1,0,0;1.5708rad)
  Thread = false
  Type = 55
FEATURE [Part::FeaturePython] Nut004  label="M4-Nut286"  # WARN: FeaturePython — macro-defined, semantics opaque (R4)
  BaseObject = -> Screw008 [Edge2]
  Diameter = 6
  Invert = true
  LeftHanded = false
  MatchOuter = false
  Offset = -7
  OffsetAngle = 0
  Placement = pos=(-19.8995,-14,217.74) rot=(1,0,0;1.5708rad)
  Thread = false
  Type = 31
FEATURE [Part::FeaturePython] Nut005  label="M4-Nut287"  # WARN: FeaturePython — macro-defined, semantics opaque (R4)
  BaseObject = -> Screw007 [Edge2]
  Diameter = 6
  Invert = true
  LeftHanded = false
  MatchOuter = false
  Offset = -7
  OffsetAngle = 0
  Placement = pos=(-3.60216e-06,-14,221.699) rot=(1,0,0;1.5708rad)
  Thread = false
  Type = 31
FEATURE [Part::FeaturePython] Nut006  label="M4-Nut288"  # WARN: FeaturePython — macro-defined, semantics opaque (R4)
  BaseObject = -> Screw006 [Edge2]
  Diameter = 6
  Invert = true
  LeftHanded = false
  MatchOuter = false
  Offset = -7
  OffsetAngle = 0
  Placement = pos=(19.8995,-14,217.74) rot=(1,0,0;1.5708rad)
  Thread = false
  Type = 31
FEATURE [Part::FeaturePython] Nut007  label="M4-Nut289"  # WARN: FeaturePython — macro-defined, semantics opaque (R4)
  BaseObject = -> Screw014 [Edge2]
  Diameter = 6
  Invert = true
  LeftHanded = false
  MatchOuter = false
  Offset = -7
  OffsetAngle = 0
  Placement = pos=(48.0417,-14,189.598) rot=(1,0,0;1.5708rad)
  Thread = false
  Type = 31
FEATURE [Part::FeaturePython] Nut008  label="M4-Nut290"  # WARN: FeaturePython — macro-defined, semantics opaque (R4)
  BaseObject = -> Screw015 [Edge2]
  Diameter = 6
  Invert = true
  LeftHanded = false
  MatchOuter = false
  Offset = -7
  OffsetAngle = 0
  Placement = pos=(48.0417,-14,149.799) rot=(1,0,0;1.5708rad)
  Thread = false
  Type = 31
FEATURE [Part::FeaturePython] Nut009  label="M4-Nut291"  # WARN: FeaturePython — macro-defined, semantics opaque (R4)
  BaseObject = -> Screw009 [Edge2]
  Diameter = 6
  Invert = true
  LeftHanded = false
  MatchOuter = false
  Offset = -7
  OffsetAngle = 0
  Placement = pos=(19.8995,-14,121.657) rot=(1,0,0;1.5708rad)
  Thread = false
  Type = 31
FEATURE [Part::FeaturePython] Nut010  label="M4-Nut292"  # WARN: FeaturePython — macro-defined, semantics opaque (R4)
  BaseObject = -> Screw010 [Edge2]
  Diameter = 6
  Invert = true
  LeftHanded = false
  MatchOuter = false
  Offset = -7
  OffsetAngle = 0
  Placement = pos=(-1.91237e-06,-14,117.699) rot=(1,0,0;1.5708rad)
  Thread = false
  Type = 31
FEATURE [Part::FeaturePython] Nut011  label="M4-Nut293"  # WARN: FeaturePython — macro-defined, semantics opaque (R4)
  BaseObject = -> Screw011 [Edge2]
  Diameter = 6
  Invert = true
  LeftHanded = false
  MatchOuter = false
  Offset = -7
  OffsetAngle = 0
  Placement = pos=(-19.8995,-14,121.657) rot=(1,0,0;1.5708rad)
  Thread = false
  Type = 31
FEATURE [Part::FeaturePython] Nut012  label="M4-Nut294"  # WARN: FeaturePython — macro-defined, semantics opaque (R4)
  BaseObject = -> Screw012 [Edge2]
  Diameter = 6
  Invert = true
  LeftHanded = false
  MatchOuter = false
  Offset = -7
  OffsetAngle = 0
  Placement = pos=(-48.0417,-14,149.799) rot=(1,0,0;1.5708rad)
  Thread = false
  Type = 31
FEATURE [Part::FeaturePython] Nut013  label="M4-Nut295"  # WARN: FeaturePython — macro-defined, semantics opaque (R4)
  BaseObject = -> Screw013 [Edge2]
  Diameter = 6
  Invert = true
  LeftHanded = false
  MatchOuter = false
  Offset = -7
  OffsetAngle = 0
  Placement = pos=(-48.0417,-14,189.598) rot=(1,0,0;1.5708rad)
  Thread = false
  Type = 31
FEATURE [Part::FeaturePython] Nut014  label="M4-Nut"  # WARN: FeaturePython — macro-defined, semantics opaque (R4)
  BaseObject = -> Body_ReactionWheel [Chamfer001.Edge233]
  Diameter = 6
  Invert = false
  LeftHanded = false
  MatchOuter = false
  Offset = 0.2
  OffsetAngle = 90
  Placement = pos=(-2.8905e-06,-15.9,177.899) rot=(0,0,1;1.5708rad)
  Thread = false
  Type = 31
FEATURE [Part::FeaturePython] Nut015  label="M4-Nut255"  # WARN: FeaturePython — macro-defined, semantics opaque (R4)
  BaseObject = -> Body_ReactionWheel [Chamfer001.Edge375]
  Diameter = 6
  Invert = false
  LeftHanded = false
  MatchOuter = false
  Offset = 0.2
  OffsetAngle = 90
  Placement = pos=(-2.57204e-06,-15.9,158.299) rot=(0,0,1;1.5708rad)
  Thread = false
  Type = 31
FEATURE [Part::FeaturePython] Screw016  label="M4x10-Screw"  # WARN: FeaturePython — macro-defined, semantics opaque (R4)
  BaseObject = -> Body_ReactionWheel [Chamfer001.Edge228]
  Diameter = 6
  Invert = false
  LeftHanded = false
  Length = 2
  LengthCustom = 10
  MatchOuter = false
  Offset = 5
  OffsetAngle = 0
  Placement = pos=(-3.02698e-06,-15.9,186.299) rot=(0,0,1;0rad)
  Thread = false
  Type = 61
FEATURE [Part::FeaturePython] Screw017  label="M4x10-Screw001"  # WARN: FeaturePython — macro-defined, semantics opaque (R4)
  BaseObject = -> Body_ReactionWheel [Chamfer001.Edge375]
  Diameter = 6
  Invert = true
  LeftHanded = false
  Length = 2
  LengthCustom = 10
  MatchOuter = false
  Offset = 5
  OffsetAngle = 0
  Placement = pos=(-2.48755e-06,-15.9,153.099) rot=(0,1,0;3.14159rad)
  Thread = false
  Type = 61
FEATURE [Mesh::Feature] Mesh002  label="Body_Rondelle (Meshed)"
FEATURE [Mesh::Feature] Mesh003  label="Body_ReactionWheel (Meshed)"
FEATURE [Sketcher::SketchObject] Sketch027
  ArcFitTolerance = 1e-06
  AttachmentSupport = -> [Chamfer002]
  ExternalGeometry = -> [Chamfer002]
  FullyConstrained = true
  MakeInternals = false
  MapMode = 5
  Placement = pos=(0,0,8) rot=(0,0,1;0rad)
  sketch-geometry (3):
    g0: ArcOfCircle CenterX=0 CenterY=-84.8494 CenterZ=0 NormalX=0 NormalY=0 NormalZ=1 AngleXU=0 Radius=25 StartAngle=2.3746 EndAngle=7.05018
    g1: LineSegment StartX=-18 StartY=-67.5 StartZ=0 EndX=18 EndY=-67.5 EndZ=0
    g2: Circle CenterX=0 CenterY=-84.8494 CenterZ=0 NormalX=0 NormalY=0 NormalZ=1 AngleXU=0 Radius=9
  constraints (7):
    c: Coincident(g0,g-3)
    c: Coincident(g1,g-3)
    c: Coincident(g0,g1)
    c: Coincident(g0,g1)
    c: Horizontal(g1)
    c: Coincident(g2,g0)
    c: Diameter(g2) = 18
FEATURE [PartDesign::Pad] Pad017  label="Pad_LockBearing"
  BaseFeature = -> Chamfer002
  Direction = (0,0,1)
  Length = 2
  Length2 = 10
  Profile = -> Sketch027
  ReferenceAxis = -> Sketch027 [N_Axis]
  Refine = true
  Reversed = true
  Suppressed = false
  Type = 0
FEATURE [Sketcher::SketchObject] Sketch030
  ArcFitTolerance = 1e-06
  AttachmentSupport = -> [XY_Plane009]
  FullyConstrained = true
  MakeInternals = false
  MapMode = 5
  sketch-geometry (6):
    g0: ArcOfCircle CenterX=0 CenterY=-84.8494 CenterZ=0 NormalX=0 NormalY=0 NormalZ=1 AngleXU=0 Radius=25 StartAngle=2.3746 EndAngle=7.05018
    g1: LineSegment StartX=18 StartY=-67.5 StartZ=0 EndX=-18 EndY=-67.5 EndZ=0
    g2: Circle CenterX=15.1 CenterY=-75.5 CenterZ=0 NormalX=0 NormalY=0 NormalZ=1 AngleXU=0 Radius=1.8
    g3: Circle CenterX=-15.1 CenterY=-75.5 CenterZ=0 NormalX=0 NormalY=0 NormalZ=1 AngleXU=0 Radius=1.8
    g4: Circle CenterX=0 CenterY=-105.5 CenterZ=0 NormalX=0 NormalY=0 NormalZ=1 AngleXU=0 Radius=1.8
    g5: Circle CenterX=0 CenterY=-84.8494 CenterZ=0 NormalX=0 NormalY=0 NormalZ=1 AngleXU=0 Radius=9
  constraints (17):
    c: PointOnObject(g0,g-2)
    c: Diameter(g0) = 50
    c: Horizontal(g1)
    c: Coincident(g0,g1)
    c: Coincident(g0,g1)
    c: DistanceX(g1,g1) = 36
    c: PointOnObject(g4,g-2)
    c: Equal(g3,g2)
    c: Equal(g2,g4)
    c: Diameter(g2) = 3.6
    c: Symmetric(g2,g3,g-2)
    c: DistanceX(g3,g2) = 30.2
    c: DistanceY(g2,g0) = 8
    c: DistanceY(g4,g2) = 30
    c: DistanceY(g0,g-1) = 67.5
    c: Coincident(g5,g0)
    c: Diameter(g5) = 18
FEATURE [PartDesign::Pad] Pad018
  Direction = (0,0,1)
  Length = 3
  Length2 = 10
  Profile = -> Sketch030
  ReferenceAxis = -> Sketch030 [N_Axis]
  Refine = true
  Reversed = true
  Suppressed = false
  Type = 0
FEATURE [PartDesign::CoordinateSystem] BearingLock
  AttacherType = Attacher::AttachEngine3D
  AttachmentOffset = pos=(0,0,0) rot=(0,0,-1;1.5708rad)
  AttachmentSupport = -> [Pad018]
  MapMode = 11
  Placement = pos=(0,-84.8494,-3) rot=(0,0,1;0rad)
FEATURE [App::Link] Body_BearingLock  label="Body_BearingLock001"
  AttachedBy = #BearingLock
  AttachedTo = Body_Arm#Arm_Axis_Bottom
  AttachmentOffset = pos=(0,0,-12) rot=(0,0,1;0rad)
  LinkPlacement = pos=(-6.8e-14,7,84.8494) rot=(1,0,0;1.5708rad)
  LinkedObject = -> Body007
  Placement = pos=(-6.8e-14,7,84.8494) rot=(1,0,0;1.5708rad)
  SolverId = Asm4EE
  expr: Placement = Body_Arm.Placement * Arm_Axis_Bottom.Placement * AttachmentOffset * BearingLock.Placement ^ -1
FEATURE [Part::FeaturePython] Screw018  label="M3x14-Screw"  # WARN: FeaturePython — macro-defined, semantics opaque (R4)
  BaseObject = -> Body_BearingLock [Pad018.Edge15]
  Diameter = 4
  Invert = true
  LeftHanded = false
  Length = 6
  LengthCustom = 14
  MatchOuter = false
  OffsetAngle = 0
  Placement = pos=(-15.1,10,9.34935) rot=(-1,0,0;1.5708rad)
  Thread = false
  Type = 52
FEATURE [Part::FeaturePython] Screw019  label="M3x14-Screw993"  # WARN: FeaturePython — macro-defined, semantics opaque (R4)
  BaseObject = -> Body_BearingLock [Pad018.Edge18]
  Diameter = 4
  Invert = true
  LeftHanded = false
  Length = 6
  LengthCustom = 14
  MatchOuter = false
  OffsetAngle = 0
  Placement = pos=(15.1,10,9.34935) rot=(-1,0,0;1.5708rad)
  Thread = false
  Type = 52
FEATURE [Part::FeaturePython] Screw020  label="M3x14-Screw994"  # WARN: FeaturePython — macro-defined, semantics opaque (R4)
  BaseObject = -> Body_BearingLock [Pad018.Edge12]
  Diameter = 4
  Invert = true
  LeftHanded = false
  Length = 6
  LengthCustom = 14
  MatchOuter = false
  OffsetAngle = 0
  Placement = pos=(5.4e-15,10,-20.6506) rot=(-1,0,0;1.5708rad)
  Thread = false
  Type = 52
FEATURE [Sketcher::SketchObject] Sketch031
  ArcFitTolerance = 1e-06
  AttachmentSupport = -> [Pad018]
  ExternalGeometry = -> [Pad018]
  FullyConstrained = true
  MakeInternals = false
  MapMode = 5
  Placement = pos=(0,0,-3) rot=(1,0,0;3.14159rad)
  sketch-geometry (2):
    g0: Circle CenterX=-15 CenterY=83.5 CenterZ=0 NormalX=0 NormalY=0 NormalZ=1 AngleXU=0 Radius=4
    g1: Circle CenterX=15 CenterY=83.5 CenterZ=0 NormalX=0 NormalY=0 NormalZ=1 AngleXU=0 Radius=4
  constraints (5):
    c: Equal(g0,g1)
    c: Diameter(g0) = 8
    c: Symmetric(g0,g1,g-2)
    c: DistanceX(g0,g1) = 30
    c: DistanceY(g-3,g0) = 8
FEATURE [PartDesign::Pad] Pad019
  BaseFeature = -> Pad018
  Direction = (0,0,-1)
  Length = 20
  Length2 = 10
  Profile = -> Sketch031
  ReferenceAxis = -> Sketch031 [N_Axis]
  Refine = true
  Suppressed = false
  Type = 0
FEATURE [PartDesign::Fillet] Fillet
  Base = -> Pad019 [Edge24,Edge22]
  BaseFeature = -> Pad019
  Radius = 3.5
  Refine = true
  SupportTransform = false
  Suppressed = false
  UseAllEdges = false
FEATURE [PartDesign::Body] Body007  label="Body_BearingLock"
  AllowCompound = false
  Group = -> [Sketch030,Pad018,BearingLock,Sketch031,Pad019,Fillet]
  Origin = -> Origin009
  Tip = -> Fillet
FEATURE [Sketcher::SketchObject] Sketch032
  ArcFitTolerance = 1e-06
  AttachmentSupport = -> [Pad017]
  ExternalGeometry = -> [Pad017]
  FullyConstrained = true
  MakeInternals = false
  MapMode = 5
  Placement = pos=(0,0,8) rot=(0,0,1;0rad)
  sketch-geometry (3):
    g0: Circle CenterX=-15 CenterY=-75.5 CenterZ=0 NormalX=0 NormalY=0 NormalZ=1 AngleXU=0 Radius=1.8
    g1: Circle CenterX=15 CenterY=-75.5 CenterZ=0 NormalX=0 NormalY=0 NormalZ=1 AngleXU=0 Radius=1.8
    g2: Circle CenterX=0 CenterY=-105.5 CenterZ=0 NormalX=0 NormalY=0 NormalZ=1 AngleXU=0 Radius=1.8
  constraints (8):
    c: PointOnObject(g2,g-2)
    c: Equal(g2,g1)
    c: Equal(g1,g0)
    c: Diameter(g0) = 3.6
    c: DistanceY(g0,g-3) = 8
    c: DistanceY(g2,g0) = 30
    c: Symmetric(g0,g1,g-2)
    c: DistanceX(g0,g1) = 30
FEATURE [PartDesign::Pocket] Pocket009
  BaseFeature = -> Pad017
  Direction = (0,0,-1)
  Length = 5
  Length2 = 5
  Profile = -> Sketch032
  ReferenceAxis = -> Sketch032 [N_Axis]
  Refine = true
  Suppressed = false
  Type = 1
FEATURE [Sketcher::SketchObject] Sketch033
  ArcFitTolerance = 1e-06
  AttachmentSupport = -> [Pocket009]
  ExternalGeometry = -> [Pocket009]
  FullyConstrained = true
  MakeInternals = false
  MapMode = 5
  Placement = pos=(0,0,8) rot=(0,0,1;0rad)
  sketch-geometry (21):
    g0: LineSegment StartX=-13.35 StartY=-78.3579 StartZ=0 EndX=-11.7 EndY=-75.5 EndZ=0
    g1: LineSegment StartX=-11.7 StartY=-75.5 StartZ=0 EndX=-13.35 EndY=-72.6421 EndZ=0
    g2: LineSegment StartX=-13.35 StartY=-72.6421 StartZ=0 EndX=-16.65 EndY=-72.6421 EndZ=0
    g3: LineSegment StartX=-16.65 StartY=-72.6421 StartZ=0 EndX=-18.3 EndY=-75.5 EndZ=0
    g4: LineSegment StartX=-18.3 StartY=-75.5 StartZ=0 EndX=-16.65 EndY=-78.3579 EndZ=0
    g5: LineSegment StartX=-16.65 StartY=-78.3579 StartZ=0 EndX=-13.35 EndY=-78.3579 EndZ=0
    g6: Circle [constr] CenterX=-15 CenterY=-75.5 CenterZ=0 NormalX=0 NormalY=0 NormalZ=1 AngleXU=0 Radius=3.3
    g7: LineSegment StartX=16.65 StartY=-72.6421 StartZ=0 EndX=13.35 EndY=-72.6421 EndZ=0
    g8: LineSegment StartX=13.35 StartY=-72.6421 StartZ=0 EndX=11.7 EndY=-75.5 EndZ=0
    g9: LineSegment StartX=11.7 StartY=-75.5 StartZ=0 EndX=13.35 EndY=-78.3579 EndZ=0
    g10: LineSegment StartX=13.35 StartY=-78.3579 StartZ=0 EndX=16.65 EndY=-78.3579 EndZ=0
    g11: LineSegment StartX=16.65 StartY=-78.3579 StartZ=0 EndX=18.3 EndY=-75.5 EndZ=0
    g12: LineSegment StartX=18.3 StartY=-75.5 StartZ=0 EndX=16.65 EndY=-72.6421 EndZ=0
    g13: Circle [constr] CenterX=15 CenterY=-75.5 CenterZ=0 NormalX=0 NormalY=0 NormalZ=1 AngleXU=0 Radius=3.3
    g14: LineSegment StartX=1.65 StartY=-102.642 StartZ=0 EndX=-1.65 EndY=-102.642 EndZ=0
    g15: LineSegment StartX=-1.65 StartY=-102.642 StartZ=0 EndX=-3.3 EndY=-105.5 EndZ=0
    g16: LineSegment StartX=-3.3 StartY=-105.5 StartZ=0 EndX=-1.65 EndY=-108.358 EndZ=0
    g17: LineSegment StartX=-1.65 StartY=-108.358 StartZ=0 EndX=1.65 EndY=-108.358 EndZ=0
    g18: LineSegment StartX=1.65 StartY=-108.358 StartZ=0 EndX=3.3 EndY=-105.5 EndZ=0
    g19: LineSegment StartX=3.3 StartY=-105.5 StartZ=0 EndX=1.65 EndY=-102.642 EndZ=0
    g20: Circle [constr] CenterX=0 CenterY=-105.5 CenterZ=0 NormalX=0 NormalY=0 NormalZ=1 AngleXU=0 Radius=3.3
  constraints (48):
    c: Coincident(g0,g1)
    c: Coincident(g1,g2)
    c: Coincident(g2,g3)
    c: Coincident(g3,g4)
    c: Coincident(g4,g5)
    c: Coincident(g5,g0)
    c: Equal(g0, g1-g5) x5
    c: PointOnObject(g0,g6)
    c: PointOnObject(g1,g6)
    c: PointOnObject(g2,g6)
    c: PointOnObject(g3,g6)
    c: PointOnObject(g4,g6)
    c: PointOnObject(g5,g6)
    c: Coincident(g6,g-3)
    c: Coincident(g7,g8)
    c: Coincident(g8,g9)
    c: Coincident(g9,g10)
    c: Coincident(g10,g11)
    c: Coincident(g11,g12)
    c: Coincident(g12,g7)
    c: Equal(g7, g8-g12) x5
    c: PointOnObject(g7,g13)
    c: PointOnObject(g8,g13)
    c: PointOnObject(g9,g13)
    c: PointOnObject(g10,g13)
    c: PointOnObject(g11,g13)
    c: PointOnObject(g12,g13)
    c: Coincident(g13,g-4)
    c: Coincident(g14,g15)
    c: Coincident(g15,g16)
    c: Coincident(g16,g17)
    c: Coincident(g17,g18)
    c: Coincident(g18,g19)
    c: Coincident(g19,g14)
    c: Equal(g14, g15-g19) x5
    c: PointOnObject(g14,g20)
    c: PointOnObject(g15,g20)
    c: PointOnObject(g16,g20)
    c: PointOnObject(g17,g20)
    c: PointOnObject(g18,g20)
    c: PointOnObject(g19,g20)
    c: Coincident(g20,g-5)
    c: Equal(g13,g6)
    c: Equal(g6,g20)
    c: Diameter(g13) = 6.6
    c: Horizontal(g2)
    c: Horizontal(g7)
    c: Horizontal(g14)
FEATURE [PartDesign::Pocket] Pocket010
  BaseFeature = -> Pocket009
  Direction = (0,0,-1)
  Length = 3
  Length2 = 5
  Profile = -> Sketch033
  ReferenceAxis = -> Sketch033 [N_Axis]
  Refine = true
  Suppressed = false
  Type = 0
FEATURE [Mesh::Feature] Mesh006  label="Body_Arm (Meshed)"
FEATURE [Part::FeaturePython] Nut019  label="M3-Nut995"  # WARN: FeaturePython — macro-defined, semantics opaque (R4)
  BaseObject = -> Body_Arm [Pocket010.Edge139]
  Diameter = 4
  Invert = false
  LeftHanded = false
  MatchOuter = false
  Offset = 1
  OffsetAngle = 0
  Placement = pos=(3.35532e-07,2.7e-15,-20.6506) rot=(1,0,0;1.5708rad)
  Thread = false
  Type = 31
FEATURE [Part::FeaturePython] Nut020  label="M3-Nut996"  # WARN: FeaturePython — macro-defined, semantics opaque (R4)
  BaseObject = -> Body_Arm [Pocket010.Edge138]
  Diameter = 4
  Invert = false
  LeftHanded = false
  MatchOuter = false
  Offset = 1
  OffsetAngle = 0
  Placement = pos=(-15,-6.2e-15,9.34935) rot=(1,0,0;1.5708rad)
  Thread = false
  Type = 31
FEATURE [Part::FeaturePython] Nut021  label="M3-Nut"  # WARN: FeaturePython — macro-defined, semantics opaque (R4)
  BaseObject = -> Body_Arm [Pocket010.Edge142]
  Diameter = 4
  Invert = false
  LeftHanded = false
  MatchOuter = false
  Offset = 1
  OffsetAngle = 0
  Placement = pos=(15,-1.51e-14,9.34935) rot=(1,0,0;1.5708rad)
  Thread = false
  Type = 31
FEATURE [Mesh::Feature] Mesh  label="Body_Front_Left (Meshed)"
FEATURE [Mesh::Feature] Mesh008  label="Body_Front_Right (Meshed)"
FEATURE [Part::Feature] Part__Feature  label="Open CASCADE STEP translator 7.5 4.1.1"
  Placement = pos=(0,0,-1.6368) rot=(0,0,1;0rad)
  shape: bbox 43.18 x 17.78 x 1.637 mm, 125 faces (baked)
FEATURE [App::Part] Board
  Group = -> [Part__Feature]
  Origin = -> Origin097
FEATURE [Part::Feature] Part__Feature001  label="CAP-0402"
  Placement = pos=(36.266,6.49561,0) rot=(0,0,-1;1.5708rad)
  shape: bbox 0.5 x 1 x 0.5 mm, 58 faces (baked)
FEATURE [App::Part] C1
  Group = -> [Part__Feature001]
  Origin = -> Origin098
FEATURE [Part::Feature] Part__Feature002  label="FER-0603"
  Placement = pos=(19.5327,6.57268,0) rot=(0,0,-1;1.5708rad)
  shape: bbox 0.8 x 1.6 x 0.8 mm, 58 faces (baked)
FEATURE [App::Part] L1
  Group = -> [Part__Feature002]
  Origin = -> Origin002
FEATURE [Part::Feature] Part__Feature003  label="CAP-0603"
  Placement = pos=(11.05,4.77,0) rot=(0,0,-1;1.5708rad)
  shape: bbox 0.8 x 1.6 x 0.8 mm, 58 faces (baked)
FEATURE [App::Part] C24
  Group = -> [Part__Feature003]
  Origin = -> Origin099
FEATURE [Part::Feature] Part__Feature004  label="Extruded"
  shape: bbox 1.75 x 0.95 x 0.23 mm, 6 faces (baked)
FEATURE [App::Part] _855924864  label="6855924864"
  Group = -> [Part__Feature004]
  Origin = -> Origin101
  Placement = pos=(7.57979,10.341,0) rot=(0,0,1;0rad)
FEATURE [App::Part] Z3
  Group = -> [_855924864]
  Origin = -> Origin100
FEATURE [Part::Feature] Part__Feature005  label="SOT-23"
  Placement = pos=(36.0642,13.5591,0.499999) rot=(0,0.707107,0.707107;3.14159rad)
  shape: bbox 3 x 2.5 x 1.1 mm, 49 faces (baked)
FEATURE [App::Part] Q1
  Group = -> [Part__Feature005]
  Origin = -> Origin102
FEATURE [Part::Feature] Part__Feature006  label="Open CASCADE STEP translator 7.5 15.1.1"
  shape: bbox 3.006 x 2.006 x 1.205 mm, 48 faces (baked)
FEATURE [App::Part] Body009
  Group = -> [Part__Feature006]
  Origin = -> Origin106
  Placement = pos=(-1.5,-1,0) rot=(0,0,1;0rad)
FEATURE [Part::Feature] Part__Feature007  label="lead"
  Placement = pos=(-1.85,-0.425,0) rot=(0,0,1;0rad)
  shape: bbox 0.8 x 0.85 x 0.2 mm, 6 faces (baked)
FEATURE [Part::Feature] Part__Feature008  label="lead001"
  Placement = pos=(1.85,0.425,0) rot=(0,0,1;3.14159rad)
  shape: bbox 0.8 x 0.85 x 0.2 mm, 6 faces (baked)
FEATURE [App::Part] _279795424  label="8279795424"
  Group = -> [Body009,Part__Feature007,Part__Feature008]
  Origin = -> Origin105
  Placement = pos=(4,2,0) rot=(0,0,1;0rad)
FEATURE [App::Part] SOD123FL
  Group = -> [_279795424]
  Origin = -> Origin104
  Placement = pos=(11.5642,15.379,0) rot=(0,0,-1;1.5708rad)
FEATURE [App::Part] D1
  Group = -> [SOD123FL]
  Origin = -> Origin103
FEATURE [Part::Feature] Part__Feature009  label="RES-0402"
  Placement = pos=(19.2067,10.5539,0) rot=(0,0,1;3.14159rad)
  shape: bbox 1 x 0.5 x 0.3375 mm, 36 faces (baked)
FEATURE [App::Part] R25
  Group = -> [Part__Feature009]
  Origin = -> Origin107
FEATURE [Part::Feature] Part__Feature010  label="Open CASCADE STEP translator 6.8 13.1.1"
  shape: bbox 1.44 x 3.11 x 1.14 mm, 58 faces (baked)
FEATURE [App::Part] Body010
  Group = -> [Part__Feature010]
  Origin = -> Origin108
  Placement = pos=(-0.715,-1.55,0) rot=(0,0,1;0rad)
FEATURE [Part::Feature] Part__Feature011  label="Leader"
  Placement = pos=(-0.715,-0.95,0) rot=(0,0,1;3.14159rad)
  shape: bbox 0.585 x 0.45 x 0.63 mm, 22 faces (baked)
FEATURE [Part::Feature] Part__Feature012  label="Leader001"
  Placement = pos=(-0.715,0.95,0) rot=(0,0,1;3.14159rad)
  shape: bbox 0.585 x 0.45 x 0.63 mm, 22 faces (baked)
FEATURE [Part::Feature] Part__Feature013  label="Leader002"
  Placement = pos=(0.715,0,0) rot=(0,0,1;0rad)
  shape: bbox 0.585 x 0.45 x 0.63 mm, 22 faces (baked)
FEATURE [App::Part] _734649824  label="6734649824"
  Group = -> [Body010,Part__Feature011,Part__Feature012,Part__Feature013]
  Origin = -> Origin013
  Placement = pos=(16.5073,9.46363,0) rot=(0,0,1;1.5708rad)
FEATURE [App::Part] Q2
  Group = -> [_734649824]
  Origin = -> Origin014
FEATURE [Part::Feature] Part__Feature014  label="Extruded001"
  shape: bbox 1.75 x 0.95 x 0.23 mm, 6 faces (baked)
FEATURE [App::Part] _855924865  label="6855924864001"
  Group = -> [Part__Feature014]
  Origin = -> Origin015
  Placement = pos=(7.58,7.29,0) rot=(0,0,1;0rad)
FEATURE [App::Part] Z2
  Group = -> [_855924865]
  Origin = -> Origin016
FEATURE [Part::Feature] Part__Feature015  label="Extruded002"
  shape: bbox 1.75 x 0.95 x 0.23 mm, 6 faces (baked)
FEATURE [App::Part] _855924866  label="6855924864002"
  Group = -> [Part__Feature015]
  Origin = -> Origin017
  Placement = pos=(7.58,9.09,0) rot=(0,0,1;0rad)
FEATURE [App::Part] Z1
  Group = -> [_855924866]
  Origin = -> Origin018
FEATURE [Part::Feature] Part__Feature016  label="RES-0403"
  Placement = pos=(10.8563,13.9862,0) rot=(0,0,1;3.14159rad)
  shape: bbox 1 x 0.5 x 0.3375 mm, 36 faces (baked)
FEATURE [App::Part] R23
  Group = -> [Part__Feature016]
  Origin = -> Origin019
FEATURE [Part::Feature] Part__Feature017  label="RES-0404"
  Placement = pos=(10.8563,12.1424,0) rot=(0,0,1;3.14159rad)
  shape: bbox 1 x 0.5 x 0.3375 mm, 36 faces (baked)
FEATURE [App::Part] R22
  Group = -> [Part__Feature017]
  Origin = -> Origin020
FEATURE [Part::Feature] Part__Feature018  label="RES-0405"
  Placement = pos=(10.8563,13.0642,0) rot=(0,0,1;3.14159rad)
  shape: bbox 1 x 0.5 x 0.3375 mm, 36 faces (baked)
FEATURE [App::Part] R20
  Group = -> [Part__Feature018]
  Origin = -> Origin021
FEATURE [Part::Feature] Part__Feature019  label="Extruded003"
  shape: bbox 0.15 x 0.3 x 0.57 mm, 6 faces (baked)
FEATURE [App::Part] _855929024  label="6855929024"
  Group = -> [Part__Feature019]
  Origin = -> Origin022
  Placement = pos=(8.7574,12.1158,0.0499999) rot=(0,0,1;0rad)
FEATURE [Part::Feature] Part__Feature020  label="Extruded004"
  shape: bbox 0.15 x 0.3 x 0.13 mm, 6 faces (baked)
FEATURE [App::Part] _855929184  label="6855929184"
  Group = -> [Part__Feature020]
  Origin = -> Origin023
  Placement = pos=(8.4174,12.1158,0.499999) rot=(0,0,1;0rad)
FEATURE [Part::Feature] Part__Feature021  label="Extruded005"
  shape: bbox 0.3 x 0.15 x 0.57 mm, 6 faces (baked)
FEATURE [App::Part] _855929344  label="6855929344"
  Group = -> [Part__Feature021]
  Origin = -> Origin024
  Placement = pos=(8.5974,12.4758,0.0499999) rot=(0,0,1;0rad)
FEATURE [Part::Feature] Part__Feature022  label="Extruded006"
  shape: bbox 1 x 1 x 0.6 mm, 6 faces (baked)
FEATURE [App::Part] _855929504  label="6855929504"
  Group = -> [Part__Feature022]
  Origin = -> Origin025
  Placement = pos=(8.5974,12.2758,0) rot=(0,0,1;0rad)
FEATURE [App::Part] DL1
  Group = -> [_855929024,_855929184,_855929344,_855929504]
  Origin = -> Origin026
FEATURE [Part::Feature] Part__Feature023  label="CAP-0604"
  Placement = pos=(19.1793,13.0283,0) rot=(0,0,1;1.5708rad)
  shape: bbox 0.8 x 1.6 x 0.8 mm, 58 faces (baked)
FEATURE [App::Part] C12
  Group = -> [Part__Feature023]
  Origin = -> Origin027
FEATURE [Part::Feature] Part__Feature024  label="sot25"
  Placement = pos=(17.4624,14.0659,0) rot=(0,0.707107,0.707107;3.14159rad)
  shape: bbox 2.4 x 3 x 1.15 mm, 75 faces (baked)
FEATURE [App::Part] U3
  Group = -> [Part__Feature024]
  Origin = -> Origin028
FEATURE [Part::Feature] Part__Feature025  label="CAP-0605"
  Placement = pos=(13.5642,14.528,0) rot=(0,0,0.991678;0rad)
  shape: bbox 1.6 x 0.8 x 0.8 mm, 58 faces (baked)
FEATURE [App::Part] C11
  Group = -> [Part__Feature025]
  Origin = -> Origin029
FEATURE [Part::Feature] Part__Feature026  label="RES-0406"
  Placement = pos=(40.3,3.53208,0) rot=(0,0,-1;1.5708rad)
  shape: bbox 0.5 x 1 x 0.3375 mm, 36 faces (baked)
FEATURE [App::Part] R19
  Group = -> [Part__Feature026]
  Origin = -> Origin030
FEATURE [Part::Feature] Part__Feature027  label="RES-0407"
  Placement = pos=(38.46,3.53208,0) rot=(0,0,1;1.5708rad)
  shape: bbox 0.5 x 1 x 0.3375 mm, 36 faces (baked)
FEATURE [App::Part] R17
  Group = -> [Part__Feature027]
  Origin = -> Origin031
FEATURE [Part::Feature] Part__Feature028  label="RES-0408"
  Placement = pos=(33.5665,3.53208,0) rot=(0,0,1;1.5708rad)
  shape: bbox 0.5 x 1 x 0.3375 mm, 36 faces (baked)
FEATURE [App::Part] R16
  Group = -> [Part__Feature028]
  Origin = -> Origin032
FEATURE [Part::Feature] Part__Feature029  label="RES-0409"
  Placement = pos=(39.38,3.53208,0) rot=(0,0,1;1.5708rad)
  shape: bbox 0.5 x 1 x 0.3375 mm, 36 faces (baked)
FEATURE [App::Part] R15
  Group = -> [Part__Feature029]
  Origin = -> Origin033
FEATURE [Part::Feature] Part__Feature030  label="SOT-024"
  Placement = pos=(39.2471,13.5591,0.499999) rot=(0,0.707107,0.707107;3.14159rad)
  shape: bbox 3 x 2.5 x 1.1 mm, 49 faces (baked)
FEATURE [App::Part] Q3
  Group = -> [Part__Feature030]
  Origin = -> Origin034
FEATURE [Part::Feature] Part__Feature031  label="SM04B-SRSS-TB_RGB12040119"
  Placement = pos=(38.877,8.875,-0.279999) rot=(0.57735,0.57735,0.57735;2.0944rad)
  shape: bbox 4.95 x 6 x 2.96 mm, 89 faces (baked)
FEATURE [App::Part] J2
  Group = -> [Part__Feature031]
  Origin = -> Origin035
FEATURE [Part::Feature] Part__Feature032  label="Open CASCADE STEP translator 6.8 6.1.1"
  shape: bbox 0.2 x 2.15 x 1 mm, 18 faces (baked)
FEATURE [Part::Feature] Part__Feature033  label="Open CASCADE STEP translator 6.8 6.1.2"
  shape: bbox 0.2 x 2.15 x 1 mm, 18 faces (baked)
FEATURE [App::Part] Terminal
  Group = -> [Part__Feature032,Part__Feature033]
  Origin = -> Origin036
  Placement = pos=(-1.325,-1.075,0) rot=(0,0,1;0rad)
FEATURE [Part::Feature] Part__Feature034  label="Open CASCADE STEP translator 6.8 6.2.1"
  shape: bbox 2.25 x 2.15 x 1 mm, 10 faces (baked)
FEATURE [App::Part] Mid_Body
  Group = -> [Part__Feature034]
  Origin = -> Origin037
  Placement = pos=(-1.325,-1.075,0) rot=(0,0,1;0rad)
FEATURE [App::Part] _734648784  label="6734648784"
  Group = -> [Terminal,Mid_Body]
  Origin = -> Origin038
  Placement = pos=(16.4718,6.21749,0) rot=(0,0,1;1.5708rad)
FEATURE [App::Part] L3
  Group = -> [_734648784]
  Origin = -> Origin039
FEATURE [Part::Feature] Part__Feature035  label="quartz_3_2__2_5_16MHz v2"
  Placement = pos=(34.13,10.99,0) rot=(0,0,-1;1.5708rad)
  shape: bbox 2.5 x 3.2 x 0.8 mm, 115 faces (baked)
FEATURE [App::Part] Y1
  Group = -> [Part__Feature035]
  Origin = -> Origin040
FEATURE [Part::Feature] Part__Feature036  label="RES-0410"
  Placement = pos=(35.4065,3.53205,0) rot=(0,0,1;1.5708rad)
  shape: bbox 0.5 x 1 x 0.3375 mm, 36 faces (baked)
FEATURE [App::Part] R14
  Group = -> [Part__Feature036]
  Origin = -> Origin041
FEATURE [Part::Feature] Part__Feature037  label="RES-0411"
  Placement = pos=(34.4865,3.53205,0) rot=(0,0,-1;1.5708rad)
  shape: bbox 0.5 x 1 x 0.3375 mm, 36 faces (baked)
FEATURE [App::Part] R11
  Group = -> [Part__Feature037]
  Origin = -> Origin042
FEATURE [Part::Feature] Part__Feature038  label="RES-0412"
  Placement = pos=(21.7,14.7,0) rot=(0,0,1;0rad)
  shape: bbox 1 x 0.5 x 0.3375 mm, 36 faces (baked)
FEATURE [App::Part] R2
  Group = -> [Part__Feature038]
  Origin = -> Origin043
FEATURE [Part::Feature] Part__Feature039  label="RES-0413"
  Placement = pos=(19.2025,8.46753,0) rot=(0,0,1;3.14159rad)
  shape: bbox 1 x 0.5 x 0.3375 mm, 36 faces (baked)
FEATURE [App::Part] R1
  Group = -> [Part__Feature039]
  Origin = -> Origin044
FEATURE [Part::Feature] Part__Feature040  label="FER-0604"
  Placement = pos=(19.548,3.84062,0) rot=(0,0,-1;1.5708rad)
  shape: bbox 0.8 x 1.6 x 0.8 mm, 58 faces (baked)
FEATURE [App::Part] L2
  Group = -> [Part__Feature040]
  Origin = -> Origin045
FEATURE [Part::Feature] Part__Feature041  label="CAP-0606"
  Placement = pos=(35.346,6.49576,0) rot=(0,0,1;1.5708rad)
  shape: bbox 0.5 x 1 x 0.5 mm, 58 faces (baked)
FEATURE [App::Part] C10
  Group = -> [Part__Feature041]
  Origin = -> Origin046
FEATURE [Part::Feature] Part__Feature042  label="CAP-0607"
  Placement = pos=(34.426,6.49576,0) rot=(0,0,1;1.5708rad)
  shape: bbox 0.5 x 1 x 0.5 mm, 58 faces (baked)
FEATURE [App::Part] C9
  Group = -> [Part__Feature042]
  Origin = -> Origin047
FEATURE [Part::Feature] Part__Feature043  label="CAP-0608"
  Placement = pos=(18.4971,6.62667,0) rot=(0,0,1;1.5708rad)
  shape: bbox 0.5 x 1 x 0.5 mm, 58 faces (baked)
FEATURE [App::Part] C8
  Group = -> [Part__Feature043]
  Origin = -> Origin048
FEATURE [Part::Feature] Part__Feature044  label="CAP-0609"
  Placement = pos=(18.4871,3.842,0) rot=(0,0,-1;1.5708rad)
  shape: bbox 0.5 x 1 x 0.5 mm, 58 faces (baked)
FEATURE [App::Part] C7
  Group = -> [Part__Feature044]
  Origin = -> Origin049
FEATURE [Part::Feature] Part__Feature045  label="CAP-0610"
  Placement = pos=(32.5465,14.1061,0) rot=(0,0,1;1.5708rad)
  shape: bbox 0.5 x 1 x 0.5 mm, 58 faces (baked)
FEATURE [App::Part] C6
  Group = -> [Part__Feature045]
  Origin = -> Origin050
FEATURE [Part::Feature] Part__Feature046  label="CAP-0611"
  Placement = pos=(33.4665,14.1061,0) rot=(0,0,1;1.5708rad)
  shape: bbox 0.5 x 1 x 0.5 mm, 58 faces (baked)
FEATURE [App::Part] C5
  Group = -> [Part__Feature046]
  Origin = -> Origin051
FEATURE [Part::Feature] Part__Feature047  label="CAP-0612"
  Placement = pos=(19.2067,9.42267,0) rot=(0,0,1;3.14159rad)
  shape: bbox 1 x 0.5 x 0.5 mm, 58 faces (baked)
FEATURE [App::Part] C4
  Group = -> [Part__Feature047]
  Origin = -> Origin052
FEATURE [Part::Feature] Part__Feature048  label="CAP-0613"
  Placement = pos=(39.8346,4.87242,0) rot=(0,0,0.991678;0rad)
  shape: bbox 1 x 0.5 x 0.5 mm, 58 faces (baked)
FEATURE [App::Part] C3
  Group = -> [Part__Feature048]
  Origin = -> Origin053
FEATURE [Part::Feature] Part__Feature049  label="CAP-0614"
  Placement = pos=(34.0482,12.305,0) rot=(0,0,1;1.5708rad)
  shape: bbox 0.5 x 1 x 0.5 mm, 58 faces (baked)
FEATURE [App::Part] C2
  Group = -> [Part__Feature049]
  Origin = -> Origin054
FEATURE [Part::Feature] Part__Feature050  label="Open CASCADE STEP translator 6.8 23.1.1"
  shape: bbox 10 x 10 x 1.65 mm, 117 faces (baked)
FEATURE [App::Part] Body011
  Group = -> [Part__Feature050]
  Origin = -> Origin055
  Placement = pos=(-5,-5,0) rot=(0,0,1;0rad)
FEATURE [Part::Feature] Part__Feature051  label="Leader003"
  Placement = pos=(-5,-3.75,0) rot=(0,0,1;3.14159rad)
  shape: bbox 1.1 x 0.27 x 0.875 mm, 22 faces (baked)
FEATURE [Part::Feature] Part__Feature052  label="Leader004"
  Placement = pos=(-3.75,5,0) rot=(0,0,1;1.5708rad)
  shape: bbox 0.27 x 1.1 x 0.875 mm, 22 faces (baked)
FEATURE [Part::Feature] Part__Feature053  label="Leader005"
  Placement = pos=(5,-3.75,0) rot=(0,0,1;0rad)
  shape: bbox 1.1 x 0.27 x 0.875 mm, 22 faces (baked)
FEATURE [Part::Feature] Part__Feature054  label="Leader006"
  Placement = pos=(-3.75,-5,0) rot=(0,0,-1;1.5708rad)
  shape: bbox 0.27 x 1.1 x 0.875 mm, 22 faces (baked)
FEATURE [Part::Feature] Part__Feature055  label="Leader007"
  Placement = pos=(-5,-3.25,0) rot=(0,0,1;3.14159rad)
  shape: bbox 1.1 x 0.27 x 0.875 mm, 22 faces (baked)
FEATURE [Part::Feature] Part__Feature056  label="Leader008"
  Placement = pos=(-3.25,5,0) rot=(0,0,1;1.5708rad)
  shape: bbox 0.27 x 1.1 x 0.875 mm, 22 faces (baked)
FEATURE [Part::Feature] Part__Feature057  label="Leader009"
  Placement = pos=(5,-3.25,0) rot=(0,0,1;0rad)
  shape: bbox 1.1 x 0.27 x 0.875 mm, 22 faces (baked)
FEATURE [Part::Feature] Part__Feature058  label="Leader010"
  Placement = pos=(-3.25,-5,0) rot=(0,0,-1;1.5708rad)
  shape: bbox 0.27 x 1.1 x 0.875 mm, 22 faces (baked)
FEATURE [Part::Feature] Part__Feature059  label="Leader011"
  Placement = pos=(-5,-2.75,0) rot=(0,0,1;3.14159rad)
  shape: bbox 1.1 x 0.27 x 0.875 mm, 22 faces (baked)
FEATURE [Part::Feature] Part__Feature060  label="Leader012"
  Placement = pos=(-2.75,5,0) rot=(0,0,1;1.5708rad)
  shape: bbox 0.27 x 1.1 x 0.875 mm, 22 faces (baked)
FEATURE [Part::Feature] Part__Feature061  label="Leader013"
  Placement = pos=(5,-2.75,0) rot=(0,0,1;0rad)
  shape: bbox 1.1 x 0.27 x 0.875 mm, 22 faces (baked)
FEATURE [Part::Feature] Part__Feature062  label="Leader014"
  Placement = pos=(-2.75,-5,0) rot=(0,0,-1;1.5708rad)
  shape: bbox 0.27 x 1.1 x 0.875 mm, 22 faces (baked)
FEATURE [Part::Feature] Part__Feature063  label="Leader015"
  Placement = pos=(-5,-2.25,0) rot=(0,0,1;3.14159rad)
  shape: bbox 1.1 x 0.27 x 0.875 mm, 22 faces (baked)
FEATURE [Part::Feature] Part__Feature064  label="Leader016"
  Placement = pos=(-2.25,5,0) rot=(0,0,1;1.5708rad)
  shape: bbox 0.27 x 1.1 x 0.875 mm, 22 faces (baked)
FEATURE [Part::Feature] Part__Feature065  label="Leader017"
  Placement = pos=(5,-2.25,0) rot=(0,0,1;0rad)
  shape: bbox 1.1 x 0.27 x 0.875 mm, 22 faces (baked)
FEATURE [Part::Feature] Part__Feature066  label="Leader018"
  Placement = pos=(-2.25,-5,0) rot=(0,0,-1;1.5708rad)
  shape: bbox 0.27 x 1.1 x 0.875 mm, 22 faces (baked)
FEATURE [Part::Feature] Part__Feature067  label="Leader019"
  Placement = pos=(-5,-1.75,0) rot=(0,0,1;3.14159rad)
  shape: bbox 1.1 x 0.27 x 0.875 mm, 22 faces (baked)
FEATURE [Part::Feature] Part__Feature068  label="Leader020"
  Placement = pos=(-1.75,5,0) rot=(0,0,1;1.5708rad)
  shape: bbox 0.27 x 1.1 x 0.875 mm, 22 faces (baked)
FEATURE [Part::Feature] Part__Feature069  label="Leader021"
  Placement = pos=(5,-1.75,0) rot=(0,0,1;0rad)
  shape: bbox 1.1 x 0.27 x 0.875 mm, 22 faces (baked)
FEATURE [Part::Feature] Part__Feature070  label="Leader022"
  Placement = pos=(-1.75,-5,0) rot=(0,0,-1;1.5708rad)
  shape: bbox 0.27 x 1.1 x 0.875 mm, 22 faces (baked)
FEATURE [Part::Feature] Part__Feature071  label="Leader023"
  Placement = pos=(-5,-1.25,0) rot=(0,0,1;3.14159rad)
  shape: bbox 1.1 x 0.27 x 0.875 mm, 22 faces (baked)
FEATURE [Part::Feature] Part__Feature072  label="Leader024"
  Placement = pos=(-1.25,5,0) rot=(0,0,1;1.5708rad)
  shape: bbox 0.27 x 1.1 x 0.875 mm, 22 faces (baked)
FEATURE [Part::Feature] Part__Feature073  label="Leader025"
  Placement = pos=(5,-1.25,0) rot=(0,0,1;0rad)
  shape: bbox 1.1 x 0.27 x 0.875 mm, 22 faces (baked)
FEATURE [Part::Feature] Part__Feature074  label="Leader026"
  Placement = pos=(-1.25,-5,0) rot=(0,0,-1;1.5708rad)
  shape: bbox 0.27 x 1.1 x 0.875 mm, 22 faces (baked)
FEATURE [Part::Feature] Part__Feature075  label="Leader027"
  Placement = pos=(-5,-0.75,0) rot=(0,0,1;3.14159rad)
  shape: bbox 1.1 x 0.27 x 0.875 mm, 22 faces (baked)
FEATURE [Part::Feature] Part__Feature076  label="Leader028"
  Placement = pos=(-0.75,5,0) rot=(0,0,1;1.5708rad)
  shape: bbox 0.27 x 1.1 x 0.875 mm, 22 faces (baked)
FEATURE [Part::Feature] Part__Feature077  label="Leader029"
  Placement = pos=(5,-0.75,0) rot=(0,0,1;0rad)
  shape: bbox 1.1 x 0.27 x 0.875 mm, 22 faces (baked)
FEATURE [Part::Feature] Part__Feature078  label="Leader030"
  Placement = pos=(-0.75,-5,0) rot=(0,0,-1;1.5708rad)
  shape: bbox 0.27 x 1.1 x 0.875 mm, 22 faces (baked)
FEATURE [Part::Feature] Part__Feature079  label="Leader031"
  Placement = pos=(-5,-0.25,0) rot=(0,0,1;3.14159rad)
  shape: bbox 1.1 x 0.27 x 0.875 mm, 22 faces (baked)
FEATURE [Part::Feature] Part__Feature080  label="Leader032"
  Placement = pos=(-0.25,5,0) rot=(0,0,1;1.5708rad)
  shape: bbox 0.27 x 1.1 x 0.875 mm, 22 faces (baked)
FEATURE [Part::Feature] Part__Feature081  label="Leader033"
  Placement = pos=(5,-0.25,0) rot=(0,0,1;0rad)
  shape: bbox 1.1 x 0.27 x 0.875 mm, 22 faces (baked)
FEATURE [Part::Feature] Part__Feature082  label="Leader034"
  Placement = pos=(-0.25,-5,0) rot=(0,0,-1;1.5708rad)
  shape: bbox 0.27 x 1.1 x 0.875 mm, 22 faces (baked)
FEATURE [Part::Feature] Part__Feature083  label="Leader035"
  Placement = pos=(-5,0.25,0) rot=(0,0,1;3.14159rad)
  shape: bbox 1.1 x 0.27 x 0.875 mm, 22 faces (baked)
FEATURE [Part::Feature] Part__Feature084  label="Leader036"
  Placement = pos=(0.25,5,0) rot=(0,0,1;1.5708rad)
  shape: bbox 0.27 x 1.1 x 0.875 mm, 22 faces (baked)
FEATURE [Part::Feature] Part__Feature085  label="Leader037"
  Placement = pos=(5,0.25,0) rot=(0,0,1;0rad)
  shape: bbox 1.1 x 0.27 x 0.875 mm, 22 faces (baked)
FEATURE [Part::Feature] Part__Feature086  label="Leader038"
  Placement = pos=(0.25,-5,0) rot=(0,0,-1;1.5708rad)
  shape: bbox 0.27 x 1.1 x 0.875 mm, 22 faces (baked)
FEATURE [Part::Feature] Part__Feature087  label="Leader039"
  Placement = pos=(-5,0.75,0) rot=(0,0,1;3.14159rad)
  shape: bbox 1.1 x 0.27 x 0.875 mm, 22 faces (baked)
FEATURE [Part::Feature] Part__Feature088  label="Leader040"
  Placement = pos=(0.75,5,0) rot=(0,0,1;1.5708rad)
  shape: bbox 0.27 x 1.1 x 0.875 mm, 22 faces (baked)
FEATURE [Part::Feature] Part__Feature089  label="Leader041"
  Placement = pos=(5,0.75,0) rot=(0,0,1;0rad)
  shape: bbox 1.1 x 0.27 x 0.875 mm, 22 faces (baked)
FEATURE [Part::Feature] Part__Feature090  label="Leader042"
  Placement = pos=(0.75,-5,0) rot=(0,0,-1;1.5708rad)
  shape: bbox 0.27 x 1.1 x 0.875 mm, 22 faces (baked)
FEATURE [Part::Feature] Part__Feature091  label="Leader043"
  Placement = pos=(-5,1.25,0) rot=(0,0,1;3.14159rad)
  shape: bbox 1.1 x 0.27 x 0.875 mm, 22 faces (baked)
FEATURE [Part::Feature] Part__Feature092  label="Leader044"
  Placement = pos=(1.25,5,0) rot=(0,0,1;1.5708rad)
  shape: bbox 0.27 x 1.1 x 0.875 mm, 22 faces (baked)
FEATURE [Part::Feature] Part__Feature093  label="Leader045"
  Placement = pos=(5,1.25,0) rot=(0,0,1;0rad)
  shape: bbox 1.1 x 0.27 x 0.875 mm, 22 faces (baked)
FEATURE [Part::Feature] Part__Feature094  label="Leader046"
  Placement = pos=(1.25,-5,0) rot=(0,0,-1;1.5708rad)
  shape: bbox 0.27 x 1.1 x 0.875 mm, 22 faces (baked)
FEATURE [Part::Feature] Part__Feature095  label="Leader047"
  Placement = pos=(-5,1.75,0) rot=(0,0,1;3.14159rad)
  shape: bbox 1.1 x 0.27 x 0.875 mm, 22 faces (baked)
FEATURE [Part::Feature] Part__Feature096  label="Leader048"
  Placement = pos=(1.75,5,0) rot=(0,0,1;1.5708rad)
  shape: bbox 0.27 x 1.1 x 0.875 mm, 22 faces (baked)
FEATURE [Part::Feature] Part__Feature097  label="Leader049"
  Placement = pos=(5,1.75,0) rot=(0,0,1;0rad)
  shape: bbox 1.1 x 0.27 x 0.875 mm, 22 faces (baked)
FEATURE [Part::Feature] Part__Feature098  label="Leader050"
  Placement = pos=(1.75,-5,0) rot=(0,0,-1;1.5708rad)
  shape: bbox 0.27 x 1.1 x 0.875 mm, 22 faces (baked)
FEATURE [Part::Feature] Part__Feature099  label="Leader051"
  Placement = pos=(-5,2.25,0) rot=(0,0,1;3.14159rad)
  shape: bbox 1.1 x 0.27 x 0.875 mm, 22 faces (baked)
FEATURE [Part::Feature] Part__Feature100  label="Leader052"
  Placement = pos=(2.25,5,0) rot=(0,0,1;1.5708rad)
  shape: bbox 0.27 x 1.1 x 0.875 mm, 22 faces (baked)
FEATURE [Part::Feature] Part__Feature101  label="Leader053"
  Placement = pos=(5,2.25,0) rot=(0,0,1;0rad)
  shape: bbox 1.1 x 0.27 x 0.875 mm, 22 faces (baked)
FEATURE [Part::Feature] Part__Feature102  label="Leader054"
  Placement = pos=(2.25,-5,0) rot=(0,0,-1;1.5708rad)
  shape: bbox 0.27 x 1.1 x 0.875 mm, 22 faces (baked)
FEATURE [Part::Feature] Part__Feature103  label="Leader055"
  Placement = pos=(-5,2.75,0) rot=(0,0,1;3.14159rad)
  shape: bbox 1.1 x 0.27 x 0.875 mm, 22 faces (baked)
FEATURE [Part::Feature] Part__Feature104  label="Leader056"
  Placement = pos=(2.75,5,0) rot=(0,0,1;1.5708rad)
  shape: bbox 0.27 x 1.1 x 0.875 mm, 22 faces (baked)
FEATURE [Part::Feature] Part__Feature105  label="Leader057"
  Placement = pos=(5,2.75,0) rot=(0,0,1;0rad)
  shape: bbox 1.1 x 0.27 x 0.875 mm, 22 faces (baked)
FEATURE [Part::Feature] Part__Feature106  label="Leader058"
  Placement = pos=(2.75,-5,0) rot=(0,0,-1;1.5708rad)
  shape: bbox 0.27 x 1.1 x 0.875 mm, 22 faces (baked)
FEATURE [Part::Feature] Part__Feature107  label="Leader059"
  Placement = pos=(-5,3.25,0) rot=(0,0,1;3.14159rad)
  shape: bbox 1.1 x 0.27 x 0.875 mm, 22 faces (baked)
FEATURE [Part::Feature] Part__Feature108  label="Leader060"
  Placement = pos=(3.25,5,0) rot=(0,0,1;1.5708rad)
  shape: bbox 0.27 x 1.1 x 0.875 mm, 22 faces (baked)
FEATURE [Part::Feature] Part__Feature109  label="Leader061"
  Placement = pos=(5,3.25,0) rot=(0,0,1;0rad)
  shape: bbox 1.1 x 0.27 x 0.875 mm, 22 faces (baked)
FEATURE [Part::Feature] Part__Feature110  label="Leader062"
  Placement = pos=(3.25,-5,0) rot=(0,0,-1;1.5708rad)
  shape: bbox 0.27 x 1.1 x 0.875 mm, 22 faces (baked)
FEATURE [Part::Feature] Part__Feature111  label="Leader063"
  Placement = pos=(-5,3.75,0) rot=(0,0,1;3.14159rad)
  shape: bbox 1.1 x 0.27 x 0.875 mm, 22 faces (baked)
FEATURE [Part::Feature] Part__Feature112  label="Leader064"
  Placement = pos=(3.75,5,0) rot=(0,0,1;1.5708rad)
  shape: bbox 0.27 x 1.1 x 0.875 mm, 22 faces (baked)
FEATURE [Part::Feature] Part__Feature113  label="Leader065"
  Placement = pos=(5,3.75,0) rot=(0,0,1;0rad)
  shape: bbox 1.1 x 0.27 x 0.875 mm, 22 faces (baked)
FEATURE [Part::Feature] Part__Feature114  label="Leader066"
  Placement = pos=(3.75,-5,0) rot=(0,0,-1;1.5708rad)
  shape: bbox 0.27 x 1.1 x 0.875 mm, 22 faces (baked)
FEATURE [App::Part] _422462560  label="6422462560"
  Group = -> [Body011,Part__Feature051,Part__Feature052,Part__Feature053,Part__Feature054,Part__Feature055,Part__Feature056,Part__Feature057,Part__Feature058,Part__Feature059,Part__Feature060,Part__Feature061,Part__Feature062,Part__Feature063,Part__Feature064,Part__Feature065,Part__Feature066,Part__Feature067,Part__Feature068,Part__Feature069,Part__Feature070,Part__Feature071,Part__Feature072,Part__Feature073,+41 more]
  Origin = -> Origin056
  Placement = pos=(12,10,0) rot=(0,0,1;0rad)
FEATURE [Part::Feature] Part__Feature115  label="Extruded007"
  shape: bbox 0.7002 x 0.7002 x 1.42 mm, 23 faces (baked)
FEATURE [App::Part] _219473552  label="7219473552"
  Group = -> [Part__Feature115]
  Origin = -> Origin057
  Placement = pos=(8.20008,13.7999,0.249999) rot=(0,0,1;0rad)
FEATURE [App::Part] Designator1
  Group = -> [_422462560,_219473552]
  Origin = -> Origin058
FEATURE [App::Part] RA4M1_v4  label="RA4M1 v4"
  Group = -> [Designator1]
  Origin = -> Origin059
  Placement = pos=(38.95,18.875,0) rot=(0,0,1;3.14159rad)
FEATURE [Part::Feature] Part__Feature116  label="Extruded008"
  shape: bbox 0.7002 x 0.7002 x 1.42 mm, 24 faces (baked)
FEATURE [App::Part] _325699712  label="7325699712"
  Group = -> [Part__Feature116]
  Origin = -> Origin060
  Placement = pos=(30.7499,5.07508,0.249999) rot=(0,0,1;0rad)
FEATURE [App::Part] U1
  Group = -> [RA4M1_v4,_325699712]
  Origin = -> Origin061
FEATURE [Part::Feature] Part__Feature117  label="RES-0414"
  Placement = pos=(5.64595,14.728,0) rot=(0,0,0.991678;0rad)
  shape: bbox 1 x 0.5 x 0.3375 mm, 36 faces (baked)
FEATURE [App::Part] R7
  Group = -> [Part__Feature117]
  Origin = -> Origin062
FEATURE [Part::Feature] Part__Feature118  label="RES-0415"
  Placement = pos=(35.3234,5.12704,0) rot=(0,0,1;3.14159rad)
  shape: bbox 1 x 0.5 x 0.3375 mm, 36 faces (baked)
FEATURE [App::Part] R13
  Group = -> [Part__Feature118]
  Origin = -> Origin063
FEATURE [Part::Feature] Part__Feature119  label="RES-0416"
  Placement = pos=(3.629,3.042,0) rot=(0,0,1;0rad)
  shape: bbox 1 x 0.5 x 0.3375 mm, 36 faces (baked)
FEATURE [App::Part] R9
  Group = -> [Part__Feature119]
  Origin = -> Origin064
FEATURE [Part::Feature] Part__Feature120  label="RES-0417"
  Placement = pos=(7.22626,3.93207,0) rot=(0,0,1;3.14159rad)
  shape: bbox 1 x 0.5 x 0.3375 mm, 36 faces (baked)
FEATURE [App::Part] R6
  Group = -> [Part__Feature120]
  Origin = -> Origin065
FEATURE [Part::Feature] Part__Feature121  label="RES-0418"
  Placement = pos=(7.22626,4.86207,0) rot=(0,0,1;3.14159rad)
  shape: bbox 1 x 0.5 x 0.3375 mm, 36 faces (baked)
FEATURE [App::Part] R5
  Group = -> [Part__Feature121]
  Origin = -> Origin066
FEATURE [Part::Feature] Part__Feature122  label="RES-0419"
  Placement = pos=(32.6465,3.53208,0) rot=(0,0,1;1.5708rad)
  shape: bbox 0.5 x 1 x 0.3375 mm, 36 faces (baked)
FEATURE [App::Part] R4
  Group = -> [Part__Feature122]
  Origin = -> Origin067
FEATURE [Part::Feature] Part__Feature123  label="RES-0420"
  Placement = pos=(7.35461,12.1629,0) rot=(0,0,1;1.5708rad)
  shape: bbox 0.5 x 1 x 0.3375 mm, 36 faces (baked)
FEATURE [App::Part] R3
  Group = -> [Part__Feature123]
  Origin = -> Origin068
FEATURE [Part::Feature] Part__Feature124  label="RES-0421"
  Placement = pos=(3.629,14.728,0) rot=(0,0,1;0rad)
  shape: bbox 1 x 0.5 x 0.3375 mm, 36 faces (baked)
FEATURE [App::Part] R8
  Group = -> [Part__Feature124]
  Origin = -> Origin069
FEATURE [Part::Feature] Part__Feature125  label="HSMx-190"
  Placement = pos=(1.40004,3.05,0) rot=(0,0,0.991678;0rad)
  shape: bbox 1.601 x 0.8052 x 0.7957 mm, 72 faces (baked)
FEATURE [App::Part] DL2
  Group = -> [Part__Feature125]
  Origin = -> Origin070
FEATURE [Part::Feature] Part__Feature126  label="CAP-0615"
  Placement = pos=(8.61119,4.38861,0) rot=(0,0,1;1.5708rad)
  shape: bbox 0.5 x 1 x 0.5 mm, 58 faces (baked)
FEATURE [App::Part] C22
  Group = -> [Part__Feature126]
  Origin = -> Origin071
FEATURE [Part::Feature] Part__Feature127  label="CAP-0616"
  Placement = pos=(9.75,4.77,0) rot=(0,0,-1;1.5708rad)
  shape: bbox 0.8 x 1.6 x 0.8 mm, 58 faces (baked)
FEATURE [App::Part] C23
  Group = -> [Part__Feature127]
  Origin = -> Origin072
FEATURE [Part::Feature] Part__Feature128  label="Open CASCADE STEP translator 6.8 19.1"
  Placement = pos=(-0.8,-1.05,0) rot=(0,0,1;0rad)
  shape: bbox 0.2 x 0.2 x 2e-07 mm, 1 faces, 0 solids (baked)
FEATURE [Part::Feature] Part__Feature129  label="Open CASCADE STEP translator 6.8 19.2.1"
  shape: bbox 1.6 x 2.1 x 0.9 mm, 8 faces (baked)
FEATURE [App::Part] Body012
  Group = -> [Part__Feature129]
  Origin = -> Origin073
  Placement = pos=(-0.8,-1.05,0) rot=(0,0,1;0rad)
FEATURE [Part::Feature] Part__Feature130  label="Open CASCADE STEP translator 6.8 19.3.1"
  shape: bbox 0.351 x 0.25 x 0.2 mm, 14 faces (baked)
FEATURE [App::Part] Pin_Shape
  Group = -> [Part__Feature130]
  Origin = -> Origin074
  Placement = pos=(-0.8,-0.875,0) rot=(0,0,1;0rad)
FEATURE [Part::Feature] Part__Feature131  label="Open CASCADE STEP translator 6.8 19.3.002"
  shape: bbox 0.351 x 0.25 x 0.2 mm, 14 faces (baked)
FEATURE [App::Part] Pin_Shape001
  Group = -> [Part__Feature131]
  Origin = -> Origin075
  Placement = pos=(0.8,0.875,0) rot=(0,0,1;3.14159rad)
FEATURE [Part::Feature] Part__Feature132  label="Open CASCADE STEP translator 6.8 19.3.003"
  shape: bbox 0.351 x 0.25 x 0.2 mm, 14 faces (baked)
FEATURE [App::Part] Pin_Shape002
  Group = -> [Part__Feature132]
  Origin = -> Origin076
  Placement = pos=(-0.8,-0.375,0) rot=(0,0,1;0rad)
FEATURE [Part::Feature] Part__Feature133  label="Open CASCADE STEP translator 6.8 19.3.004"
  shape: bbox 0.351 x 0.25 x 0.2 mm, 14 faces (baked)
FEATURE [App::Part] Pin_Shape003
  Group = -> [Part__Feature133]
  Origin = -> Origin077
  Placement = pos=(0.8,0.375,0) rot=(0,0,1;3.14159rad)
FEATURE [Part::Feature] Part__Feature134  label="Open CASCADE STEP translator 6.8 19.3.005"
  shape: bbox 0.351 x 0.25 x 0.2 mm, 14 faces (baked)
FEATURE [App::Part] Pin_Shape004
  Group = -> [Part__Feature134]
  Origin = -> Origin078
  Placement = pos=(-0.8,0.125,0) rot=(0,0,1;0rad)
FEATURE [Part::Feature] Part__Feature135  label="Open CASCADE STEP translator 6.8 19.3.006"
  shape: bbox 0.351 x 0.25 x 0.2 mm, 14 faces (baked)
FEATURE [App::Part] Pin_Shape005
  Group = -> [Part__Feature135]
  Origin = -> Origin079
  Placement = pos=(0.8,-0.125,0) rot=(0,0,1;3.14159rad)
FEATURE [Part::Feature] Part__Feature136  label="Open CASCADE STEP translator 6.8 19.3.007"
  shape: bbox 0.351 x 0.25 x 0.2 mm, 14 faces (baked)
FEATURE [App::Part] Pin_Shape006
  Group = -> [Part__Feature136]
  Origin = -> Origin080
  Placement = pos=(-0.8,0.625,0) rot=(0,0,1;0rad)
FEATURE [Part::Feature] Part__Feature137  label="Open CASCADE STEP translator 6.8 19.3.008"
  shape: bbox 0.351 x 0.25 x 0.2 mm, 14 faces (baked)
FEATURE [App::Part] Pin_Shape007
  Group = -> [Part__Feature137]
  Origin = -> Origin081
  Placement = pos=(0.8,-0.625,0) rot=(0,0,1;3.14159rad)
FEATURE [App::Part] _710435664  label="6710435664"
  Group = -> [Part__Feature128,Body012,Pin_Shape,Pin_Shape001,Pin_Shape002,Pin_Shape003,Pin_Shape004,Pin_Shape005,Pin_Shape006,Pin_Shape007]
  Origin = -> Origin082
  Placement = pos=(13.1183,4.89331,0) rot=(0,0,1;0rad)
FEATURE [App::Part] U2
  Group = -> [_710435664]
  Origin = -> Origin083
FEATURE [Part::Feature] Part__Feature138  label="CAP-0617"
  Placement = pos=(12.875,3.1975,0) rot=(0,0,1;3.14159rad)
  shape: bbox 1 x 0.5 x 0.5 mm, 58 faces (baked)
FEATURE [App::Part] C28
  Group = -> [Part__Feature138]
  Origin = -> Origin084
FEATURE [Part::Feature] Part__Feature139  label="CAP-0618"
  Placement = pos=(17.1,3.1975,0) rot=(0,0,1;0rad)
  shape: bbox 1 x 0.5 x 0.5 mm, 58 faces (baked)
FEATURE [App::Part] C25
  Group = -> [Part__Feature139]
  Origin = -> Origin085
FEATURE [Part::Feature] Part__Feature140  label="CAP-0619"
  Placement = pos=(14.7996,5.53043,0) rot=(0,0,-1;1.5708rad)
  shape: bbox 0.5 x 1 x 0.5 mm, 58 faces (baked)
FEATURE [App::Part] C20
  Group = -> [Part__Feature140]
  Origin = -> Origin086
FEATURE [Part::Feature] Part__Feature141  label="CAP-0620"
  Placement = pos=(13.5642,8.42444,0) rot=(0,0,1;0rad)
  shape: bbox 1.6 x 0.8 x 0.8 mm, 58 faces (baked)
FEATURE [App::Part] C27
  Group = -> [Part__Feature141]
  Origin = -> Origin087
FEATURE [Part::Feature] Part__Feature142  label="CAP-0621"
  Placement = pos=(13.5642,7.09443,0) rot=(0,0,1;0rad)
  shape: bbox 1.6 x 0.8 x 0.8 mm, 58 faces (baked)
FEATURE [App::Part] C26
  Group = -> [Part__Feature142]
  Origin = -> Origin088
FEATURE [Part::Feature] Part__Feature143  label="RES-0422"
  Placement = pos=(15.25,3.1975,0) rot=(0,0,1;0rad)
  shape: bbox 1 x 0.5 x 0.3375 mm, 36 faces (baked)
FEATURE [App::Part] R21
  Group = -> [Part__Feature143]
  Origin = -> Origin089
FEATURE [Part::Feature] Part__Feature144  label="RES-0423"
  Placement = pos=(17.1,4.149,0) rot=(0,0,0.991678;0rad)
  shape: bbox 1 x 0.5 x 0.3375 mm, 36 faces (baked)
FEATURE [App::Part] R18
  Group = -> [Part__Feature144]
  Origin = -> Origin090
FEATURE [Part::Feature] Part__Feature145  label="HSMx-191"
  Placement = pos=(1.4,14.73,0) rot=(0,0,0.991678;0rad)
  shape: bbox 1.601 x 0.8052 x 0.7957 mm, 72 faces (baked)
FEATURE [App::Part] DL3
  Group = -> [Part__Feature145]
  Origin = -> Origin091
FEATURE [Part::Feature] Part__Feature146  label="PTS820J20KSMTRLFS"
  Placement = pos=(10.7943,8.88999,0) rot=(0,0,1;1.5708rad)
  shape: bbox 2.9 x 4.5 x 2.005 mm, 253 faces (baked)
FEATURE [App::Part] PB1
  Group = -> [Part__Feature146]
  Origin = -> Origin092
FEATURE [Part::Feature] Part__Feature147  label="CX90B-16P_3D"
  Placement = pos=(0.25,-4.65,1.28) rot=(1,0,0;1.5708rad)
  shape: bbox 9.54 x 6.8 x 3.629 mm, 1192 faces (baked)
FEATURE [App::Part] CX90B_16P_CL0480_0755_0_00_3DDrawing_STEP_CX90B_16P_3D_48007525000_3D__STP  label="CX90B-16P_CL0480-0755-0-00_3DDrawing_STEP_CX90B-16P_3D_48007525000_3D_
STP"
  Group = -> [Part__Feature147]
  Origin = -> Origin093
  Placement = pos=(3.63805,8.89,0.309999) rot=(0,0,-1;1.5708rad)
FEATURE [App::Part] J1
  Group = -> [CX90B_16P_CL0480_0755_0_00_3DDrawing_STEP_CX90B_16P_3D_48007525000_3D__STP]
  Origin = -> Origin094
FEATURE [Part::Feature] Part__Feature148  label="CAP-0805"
  Placement = pos=(8.18914,14.0075,0) rot=(0,0,1;3.14159rad)
  shape: bbox 2 x 1.25 x 1.25 mm, 58 faces (baked)
FEATURE [App::Part] C16
  Group = -> [Part__Feature148]
  Origin = -> Origin095
FEATURE [PartDesign::CoordinateSystem] Nano_USB_Left
  AttacherType = Attacher::AttachEngine3D
  AttachmentOffset = pos=(0,0,0) rot=(0,0,-1;1.5708rad)
  AttachmentSupport = -> [Part__Feature]
  MapMode = 45
  Placement = pos=(1.27,1.27,2e-16) rot=(0,0,-1;1.5708rad)
FEATURE [App::Part] PCB
  Group = -> [Board,C1,L1,C24,Z3,Q1,D1,R25,Q2,Z2,Z1,R23,R22,R20,DL1,C12,U3,C11,R19,R17,R16,R15,Q3,J2,L3,Y1,R14,R11,R2,R1,L2,C10,C9,C8,C7,C6,C5,C4,C3,C2,U1,R7,R13,R9,R6,R5,R4,R3,R8,DL2,C22,C23,U2,C28,C25,C20,C27,C26,R21,R18,DL3,PB1,J1,C16,Nano_USB_Left]
  Origin = -> Origin096
  Placement = pos=(0,0,3) rot=(0,0,1;0rad)
FEATURE [Part::FeaturePython] Screw021  label="M5x40-Screw"  # WARN: FeaturePython — macro-defined, semantics opaque (R4)
  BaseObject = -> Body_Support [Pocket.Edge61]
  Diameter = 4
  Invert = false
  LeftHanded = false
  Length = 10
  LengthCustom = 40
  MatchOuter = false
  Offset = 1
  OffsetAngle = 0
  Placement = pos=(-1.17e-14,-1,-1.43e-14) rot=(1,0,0;1.5708rad)
  Thread = false
  Type = 43
FEATURE [Part::FeaturePython] Nut022  label="M5-Nut4868"  # WARN: FeaturePython — macro-defined, semantics opaque (R4)
  BaseObject = -> Screw021 [Edge73]
  Diameter = 7
  Invert = false
  LeftHanded = false
  MatchOuter = false
  Offset = 10
  OffsetAngle = 0
  Placement = pos=(-8.4e-15,29,-7.7e-15) rot=(1,0,0;1.5708rad)
  Thread = false
  Type = 31
FEATURE [Mesh::Feature] Mesh009  label="Body_Box_Arduino (Meshed)"
FEATURE [Sketcher::SketchObject] Sketch048
  ArcFitTolerance = 1e-06
  AttachmentSupport = -> [XZ_Plane110]
  FullyConstrained = true
  MakeInternals = false
  MapMode = 5
  Placement = pos=(0,0,0) rot=(1,0,0;1.5708rad)
  sketch-geometry (6):
    g0: Circle CenterX=8.5 CenterY=-6.5 CenterZ=0 NormalX=0 NormalY=0 NormalZ=1 AngleXU=0 Radius=1.5
    g1: Circle CenterX=-8.5 CenterY=-6.5 CenterZ=0 NormalX=0 NormalY=0 NormalZ=1 AngleXU=0 Radius=1.5
    g2: Circle CenterX=-5.3 CenterY=-6.5 CenterZ=0 NormalX=0 NormalY=0 NormalZ=1 AngleXU=0 Radius=0.8
    g3: Circle CenterX=-2.8 CenterY=-6.5 CenterZ=0 NormalX=0 NormalY=0 NormalZ=1 AngleXU=0 Radius=0.8
    g4: Circle CenterX=2.8 CenterY=-6.5 CenterZ=0 NormalX=0 NormalY=0 NormalZ=1 AngleXU=0 Radius=0.8
    g5: Circle CenterX=5.3 CenterY=-6.5 CenterZ=0 NormalX=0 NormalY=0 NormalZ=1 AngleXU=0 Radius=0.8
  constraints (15):
    c: Equal(g0,g1)
    c: Equal(g5,g4)
    c: Equal(g4,g3)
    c: Equal(g3,g2)
    c: Symmetric(g0,g1,g-2)
    c: Diameter(g0) = 3
    c: DistanceX(g1,g0) = 17
    c: DistanceY(g0,g-1) = 6.5
    c: Diameter(g2) = 1.6
    c: Symmetric(g5,g2,g-2)
    c: Symmetric(g4,g3,g-2)
    c: DistanceX(g3,g4) = 5.6
    c: DistanceX(g2,g5) = 10.6
    c: DistanceY(g5,g-1) = 6.5
    c: DistanceY(g4,g-1) = 6.5
FEATURE [Sketcher::SketchObject] Sketch049
  ArcFitTolerance = 1e-06
  AttachmentSupport = -> [XZ_Plane110]
  FullyConstrained = true
  MakeInternals = false
  MapMode = 5
  Placement = pos=(0,0,0) rot=(1,0,0;1.5708rad)
  sketch-geometry (4):
    g0: LineSegment StartX=-10 StartY=8 StartZ=0 EndX=-10 EndY=-8 EndZ=0
    g1: LineSegment StartX=-10 StartY=-8 StartZ=0 EndX=10 EndY=-8 EndZ=0
    g2: LineSegment StartX=10 StartY=-8 StartZ=0 EndX=10 EndY=8 EndZ=0
    g3: LineSegment StartX=10 StartY=8 StartZ=0 EndX=-10 EndY=8 EndZ=0
  constraints (11):
    c: Coincident(g0,g1)
    c: Coincident(g1,g2)
    c: Coincident(g2,g3)
    c: Coincident(g3,g0)
    c: Vertical(g0)
    c: Vertical(g2)
    c: Horizontal(g1)
    c: Horizontal(g3)
    c: Symmetric(g1,g0,g-1)
    c: DistanceY(g0,g0) = 16
    c: DistanceX(g1,g1) = 20
FEATURE [PartDesign::Pad] Pad030
  Direction = (0,-1,2e-16)
  Length = 64.5
  Length2 = 10
  Placement = pos=(0,0,0) rot=(1,0,0;1.5708rad)
  Profile = -> Sketch049
  ReferenceAxis = -> Sketch049 [N_Axis]
  Refine = true
  Suppressed = false
  Type = 0
FEATURE [PartDesign::Fillet] Fillet007
  Base = -> Pad030 [Edge10,Edge4]
  BaseFeature = -> Pad030
  Placement = pos=(0,0,0) rot=(1,0,0;1.5708rad)
  Radius = 3
  Refine = true
  SupportTransform = false
  Suppressed = false
  UseAllEdges = false
FEATURE [PartDesign::Fillet] Fillet008
  Base = -> Fillet007 [Edge3,Edge13]
  BaseFeature = -> Fillet007
  Placement = pos=(0,0,0) rot=(1,0,0;1.5708rad)
  Radius = 9
  Refine = true
  SupportTransform = false
  Suppressed = false
  UseAllEdges = false
FEATURE [PartDesign::Pad] Pad031  label="Pad_Battery"
  BaseFeature = -> Fillet008
  Direction = (0,-1,2e-16)
  Length = 10
  Length2 = 10
  Midplane = true
  Placement = pos=(0,0,0) rot=(1,0,0;1.5708rad)
  Profile = -> Sketch048
  ReferenceAxis = -> Sketch048 [N_Axis]
  Refine = true
  Suppressed = false
  Type = 0
FEATURE [PartDesign::CoordinateSystem] Battery
  AttacherType = Attacher::AttachEngine3D
  AttachmentSupport = -> [Pad031]
  MapMode = 45
  Placement = pos=(-7,-64.5,2.89e-14) rot=(0,0,1;0rad)
FEATURE [PartDesign::Body] Body014  label="Body_Battery_Tattu"
  AllowCompound = false
  Group = -> [Sketch049,Pad030,Fillet007,Fillet008,Sketch048,Pad031,Battery]
  Origin = -> Origin110
  Tip = -> Pad031
FEATURE [Sketcher::SketchObject] Sketch050
  ArcFitTolerance = 1e-06
  AttachmentSupport = -> [XY_Plane001]
  FullyConstrained = true
  MakeInternals = false
  MapMode = 5
  sketch-geometry (2):
    g0: Circle CenterX=-27.5 CenterY=-5 CenterZ=0 NormalX=0 NormalY=0 NormalZ=1 AngleXU=0 Radius=2.3
    g1: Circle CenterX=27.5 CenterY=-5 CenterZ=0 NormalX=0 NormalY=0 NormalZ=1 AngleXU=0 Radius=2.3
  constraints (5):
    c: Equal(g1,g0)
    c: Diameter(g1) = 4.6
    c: DistanceX(g0,g1) = 55
    c: DistanceY(g1,g-1) = 5
    c: Symmetric(g1,g0,g-2)
FEATURE [PartDesign::Pocket] Pocket015
  BaseFeature = -> Pocket
  Direction = (0,0,-1)
  Length = 5
  Length2 = 5
  Placement = pos=(0,0,0) rot=(1,0,0;1.5708rad)
  Profile = -> Sketch050
  ReferenceAxis = -> Sketch050 [N_Axis]
  Refine = true
  Reversed = true
  Suppressed = false
  Type = 1
FEATURE [PartDesign::Chamfer] Chamfer003
  Angle = 45
  Base = -> Pocket015 [Edge47,Edge40]
  BaseFeature = -> Pocket015
  ChamferType = 0
  FlipDirection = false
  Placement = pos=(0,0,0) rot=(1,0,0;1.5708rad)
  Refine = true
  Size = 1.5
  Size2 = 1
  SupportTransform = false
  Suppressed = false
  UseAllEdges = false
FEATURE [Sketcher::SketchObject] Sketch051
  ArcFitTolerance = 1e-06
  AttachmentSupport = -> [XY_Plane111]
  FullyConstrained = true
  MakeInternals = false
  MapMode = 5
  sketch-geometry (1):
    g0: Circle CenterX=0 CenterY=55 CenterZ=0 NormalX=0 NormalY=0 NormalZ=1 AngleXU=0 Radius=2.3
  constraints (3):
    c: PointOnObject(g0,g-2)
    c: DistanceY(g-1,g0) = 55
    c: Diameter(g0) = 4.6
FEATURE [Sketcher::SketchObject] Sketch052
  ArcFitTolerance = 1e-06
  AttachmentSupport = -> [XY_Plane111]
  FullyConstrained = true
  MakeInternals = false
  MapMode = 5
  sketch-geometry (1):
    g0: Circle CenterX=0 CenterY=0 CenterZ=0 NormalX=0 NormalY=0 NormalZ=1 AngleXU=0 Radius=62.5
  constraints (2):
    c: Coincident(g0,g-1)
    c: Diameter(g0) = 125
FEATURE [PartDesign::Pad] Pad032
  Direction = (0,0,1)
  Length = 3
  Length2 = 10
  Profile = -> Sketch052
  ReferenceAxis = -> Sketch052 [N_Axis]
  Refine = true
  Suppressed = false
  Type = 0
FEATURE [PartDesign::Fillet] Fillet009
  Base = -> Pad032 [Edge3,Edge2]
  BaseFeature = -> Pad032
  Radius = 1.49
  Refine = true
  SupportTransform = false
  Suppressed = false
  UseAllEdges = false
FEATURE [PartDesign::Pocket] Pocket016
  BaseFeature = -> Fillet009
  Direction = (0,0,-1)
  Length = 5
  Length2 = 5
  Profile = -> Sketch051
  ReferenceAxis = -> Sketch051 [N_Axis]
  Refine = true
  Reversed = true
  Suppressed = false
  Type = 0
FEATURE [PartDesign::PolarPattern] PolarPattern006
  Angle = 360
  Axis = -> Sketch051 [N_Axis]
  BaseFeature = -> Pocket016
  Mode = 0
  Occurrences = 6
  Offset = 120
  Originals = -> [Pocket016]
  Refine = true
  Suppressed = false
  TransformMode = 0
FEATURE [PartDesign::CoordinateSystem] Trepied
  AttacherType = Attacher::AttachEngine3D
  AttachmentOffset = pos=(0,0,0) rot=(0.707107,0.707107,0;3.14159rad)
  AttachmentSupport = -> [PolarPattern006]
  MapMode = 11
  Placement = pos=(-6.7e-15,-55,3) rot=(0,0,1;0rad)
FEATURE [PartDesign::CoordinateSystem] Support_Foot
  AttacherType = Attacher::AttachEngine3D
  AttachmentOffset = pos=(0,0,0) rot=(0.866025,-0.5,0;3.14159rad)
  AttachmentSupport = -> [Pocket015]
  MapMode = 11
  Placement = pos=(-27.5,-5,6) rot=(0,0,1;5.75959rad)
FEATURE [PartDesign::Fillet] Fillet010
  Base = -> Pocket015 [Edge31,Edge16,Edge13,Edge28]
  BaseFeature = -> Pocket015
  Placement = pos=(0,0,0) rot=(1,0,0;1.5708rad)
  Radius = 4.99
  Refine = true
  SupportTransform = false
  Suppressed = false
  UseAllEdges = false
FEATURE [PartDesign::Body] Body  label="Body_Support"
  AllowCompound = false
  Description = Pendulum
  Group = -> [Sketch,Pad,Sketch001,Pad001,Sketch002,Pad002,Sketch003,Pocket,Support,Sketch050,Pocket015,Chamfer003,Support_Foot,Fillet010]
  Origin = -> Origin001
  Tip = -> Fillet010
FEATURE [Part::FeaturePython] Screw026  label="M4x25-Screw"  # WARN: FeaturePython — macro-defined, semantics opaque (R4)
  BaseObject = -> Body_Support [Fillet010.Edge59]
  Diameter = 6
  Invert = true
  LeftHanded = false
  Length = 7
  LengthCustom = 25
  MatchOuter = false
  Offset = 1
  OffsetAngle = 0
  Placement = pos=(27.5,21.6,-19) rot=(0,0,1;0rad)
  Thread = false
  Type = 62
FEATURE [Part::FeaturePython] Screw027  label="M4x25-Screw035"  # WARN: FeaturePython — macro-defined, semantics opaque (R4)
  BaseObject = -> Body_Support [Fillet010.Edge44]
  Diameter = 6
  Invert = true
  LeftHanded = false
  Length = 7
  LengthCustom = 25
  MatchOuter = false
  Offset = 1
  OffsetAngle = 0
  Placement = pos=(-27.5,21.6,-19) rot=(0,0,1;0rad)
  Thread = false
  Type = 62
FEATURE [Part::FeaturePython] Nut027  label="M4-Nut211"  # WARN: FeaturePython — macro-defined, semantics opaque (R4)
  BaseObject = -> Screw027 [Edge1]
  Diameter = 6
  Invert = false
  LeftHanded = false
  MatchOuter = false
  Offset = 10
  OffsetAngle = 0
  Placement = pos=(-27.5,21.6,-34) rot=(0,0,1;0rad)
  Thread = false
  Type = 31
FEATURE [Part::FeaturePython] Nut028  label="M4-Nut210"  # WARN: FeaturePython — macro-defined, semantics opaque (R4)
  BaseObject = -> Screw026 [Edge1]
  Diameter = 6
  Invert = false
  LeftHanded = false
  MatchOuter = false
  Offset = 10
  OffsetAngle = 0
  Placement = pos=(27.5,21.6,-34) rot=(0,0,1;0rad)
  Thread = false
  Type = 31
FEATURE [Mesh::Feature] Mesh010  label="Body_Support (Meshed)"
FEATURE [Sketcher::SketchObject] Sketch053
  ArcFitTolerance = 1e-06
  AttachmentSupport = -> [PolarPattern006]
  FullyConstrained = true
  MakeInternals = false
  MapMode = 5
  Placement = pos=(0,0,3) rot=(0,0,1;0rad)
  sketch-geometry (2):
    g0: Circle CenterX=0 CenterY=0 CenterZ=0 NormalX=0 NormalY=0 NormalZ=1 AngleXU=0 Radius=37
    g1: Circle CenterX=0 CenterY=0 CenterZ=0 NormalX=0 NormalY=0 NormalZ=1 AngleXU=0 Radius=35.3
  constraints (4):
    c: Coincident(g0,g-1)
    c: Diameter(g0) = 74
    c: Coincident(g1,g0)
    c: Diameter(g1) = 70.6
FEATURE [PartDesign::Pad] Pad033
  BaseFeature = -> PolarPattern006
  Direction = (0,0,1)
  Length = 60
  Length2 = 10
  Profile = -> Sketch053
  ReferenceAxis = -> Sketch053 [N_Axis]
  Refine = true
  Reversed = true
  Suppressed = false
  Type = 0
FEATURE [Sketcher::SketchObject] Sketch054
  ArcFitTolerance = 1e-06
  AttachmentSupport = -> [XY_Plane112]
  FullyConstrained = true
  MakeInternals = false
  MapMode = 5
  sketch-geometry (1):
    g0: Circle CenterX=0 CenterY=0 CenterZ=0 NormalX=0 NormalY=0 NormalZ=1 AngleXU=0 Radius=30
  constraints (2):
    c: Diameter(g0) = 60
    c: Coincident(g-1,g0)
FEATURE [PartDesign::Pad] Pad034
  Direction = (0,0,1)
  Length = 30
  Length2 = 10
  Profile = -> Sketch054
  ReferenceAxis = -> Sketch054 [N_Axis]
  Refine = true
  Suppressed = false
  Type = 0
FEATURE [Sketcher::SketchObject] Sketch055
  ArcFitTolerance = 1e-06
  AttachmentSupport = -> [XZ_Plane112]
  ExternalGeometry = -> [Pad034]
  FullyConstrained = true
  MakeInternals = false
  MapMode = 5
  Placement = pos=(0,0,0) rot=(1,0,0;1.5708rad)
  sketch-geometry (8):
    g0: LineSegment StartX=62.9979 StartY=30 StartZ=0 EndX=197.788 EndY=-162.501 EndZ=0
    g1: LineSegment StartX=197.788 StartY=-162.501 StartZ=0 EndX=157.788 EndY=-162.501 EndZ=0
    g2: LineSegment StartX=157.788 StartY=-162.501 StartZ=0 EndX=30 EndY=20 EndZ=0
    g3: LineSegment StartX=-157.788 StartY=-162.501 StartZ=0 EndX=-197.788 EndY=-162.501 EndZ=0
    g4: LineSegment StartX=-197.788 StartY=-162.501 StartZ=0 EndX=-62.9979 EndY=30 EndZ=0
    g5: LineSegment StartX=-62.9979 StartY=30 StartZ=0 EndX=62.9979 EndY=30 EndZ=0
    g6: LineSegment StartX=30 StartY=20 StartZ=0 EndX=-30 EndY=20 EndZ=0
    g7: LineSegment StartX=-30 StartY=20 StartZ=0 EndX=-157.788 EndY=-162.501 EndZ=0
  constraints (21):
    c: Coincident(g0,g1)
    c: Horizontal(g1)
    c: Coincident(g1,g2)
    c: Parallel(g0,g2)
    c: DistanceX(g1,g1) = 40
    c: Distance(g0) = 235
    c: Angle(g-1,g2) = 2.18166
    c: PointOnObject(g2,g-3)
    c: Horizontal(g3)
    c: Coincident(g3,g4)
    c: Coincident(g4,g5)
    c: Coincident(g6,g7)
    c: Coincident(g7,g3)
    c: Symmetric(g3,g1,g-2)
    c: DistanceX(g3,g3) = 40
    c: Symmetric(g4,g0,g-2)
    c: Symmetric(g6,g2,g-2)
    c: Coincident(g5,g0)
    c: Coincident(g6,g2)
    c: DistanceY(g6,g4) = 10
    c: PointOnObject(g-3,g5)
FEATURE [PartDesign::Pad] Pad035
  BaseFeature = -> Pad034
  Direction = (0,-1,2e-16)
  Length = 50
  Length2 = 10
  Midplane = true
  Profile = -> Sketch055
  ReferenceAxis = -> Sketch055 [N_Axis]
  Refine = true
  Suppressed = false
  Type = 0
FEATURE [Sketcher::SketchObject] Sketch056
  ArcFitTolerance = 1e-06
  AttachmentSupport = -> [Pad035]
  FullyConstrained = true
  MakeInternals = false
  MapMode = 5
  Placement = pos=(0,0,30) rot=(0,0,1;0rad)
  sketch-geometry (1):
    g0: Circle CenterX=0 CenterY=0 CenterZ=0 NormalX=0 NormalY=0 NormalZ=1 AngleXU=0 Radius=25.3
  constraints (2):
    c: Coincident(g0,g-1)
    c: Diameter(g0) = 50.6
FEATURE [Sketcher::SketchObject] Sketch057
  ArcFitTolerance = 1e-06
  AttachmentOffset = pos=(0,0,0) rot=(0,1,0;2.0944rad)
  AttachmentSupport = -> [XZ_Plane112]
  FullyConstrained = true
  MakeInternals = false
  MapMode = 5
  Placement = pos=(0,0,0) rot=(0.377964,0.654654,0.654654;2.41886rad)
  sketch-geometry (6):
    g0: LineSegment StartX=0 StartY=30 StartZ=0 EndX=62.9979 EndY=30 EndZ=0
    g1: LineSegment StartX=62.9979 StartY=30 StartZ=0 EndX=197.788 EndY=-162.501 EndZ=0
    g2: LineSegment StartX=197.788 StartY=-162.501 StartZ=0 EndX=157.788 EndY=-162.501 EndZ=0
    g3: LineSegment StartX=157.788 StartY=-162.501 StartZ=0 EndX=30 EndY=20 EndZ=0
    g4: LineSegment StartX=30 StartY=20 StartZ=0 EndX=0 EndY=20 EndZ=0
    g5: LineSegment StartX=0 StartY=20 StartZ=0 EndX=0 EndY=30 EndZ=0
  constraints (18):
    c: PointOnObject(g0,g-2)
    c: Horizontal(g0)
    c: Coincident(g0,g1)
    c: Coincident(g1,g2)
    c: Horizontal(g2)
    c: Coincident(g2,g3)
    c: Coincident(g3,g4)
    c: Coincident(g4,g5)
    c: Coincident(g5,g0)
    c: Vertical(g5)
    c: Horizontal(g4)
    c: DistanceY(g5,g5) = 10
    c: DistanceX(g2,g2) = 40
    c: Angle(g-1,g3) = 2.18166
    c: Distance(g1) = 235
    c: Parallel(g3,g1)
    c: DistanceY(g-1,g4) = 20
    c: DistanceX(g4,g4) = 30
FEATURE [Sketcher::SketchObject] Sketch058
  ArcFitTolerance = 1e-06
  AttachmentOffset = pos=(0,0,0) rot=(0,1,0;1.0472rad)
  AttachmentSupport = -> [XZ_Plane112]
  FullyConstrained = true
  MakeInternals = false
  MapMode = 5
  Placement = pos=(0,0,0) rot=(0.774597,0.447214,0.447214;1.82348rad)
  sketch-geometry (6):
    g0: LineSegment StartX=0 StartY=30 StartZ=0 EndX=62.9979 EndY=30 EndZ=0
    g1: LineSegment StartX=62.9979 StartY=30 StartZ=0 EndX=197.788 EndY=-162.501 EndZ=0
    g2: LineSegment StartX=197.788 StartY=-162.501 StartZ=0 EndX=157.788 EndY=-162.501 EndZ=0
    g3: LineSegment StartX=157.788 StartY=-162.501 StartZ=0 EndX=30 EndY=20 EndZ=0
    g4: LineSegment StartX=30 StartY=20 StartZ=0 EndX=0 EndY=20 EndZ=0
    g5: LineSegment StartX=0 StartY=20 StartZ=0 EndX=0 EndY=30 EndZ=0
  constraints (18):
    c: PointOnObject(g0,g-2)
    c: Horizontal(g0)
    c: Coincident(g0,g1)
    c: Coincident(g1,g2)
    c: Horizontal(g2)
    c: Coincident(g2,g3)
    c: Coincident(g3,g4)
    c: Coincident(g4,g5)
    c: Coincident(g5,g0)
    c: Vertical(g5)
    c: Horizontal(g4)
    c: DistanceY(g5,g5) = 10
    c: DistanceX(g2,g2) = 40
    c: Angle(g-1,g3) = 2.18166
    c: Distance(g1) = 235
    c: Parallel(g3,g1)
    c: DistanceY(g-1,g4) = 20
    c: DistanceX(g4,g4) = 30
FEATURE [Sketcher::SketchObject] Sketch059
  ArcFitTolerance = 1e-06
  AttachmentOffset = pos=(0,0,-163) rot=(0,0,1;0rad)
  AttachmentSupport = -> [XY_Plane112]
  FullyConstrained = true
  MakeInternals = false
  MapMode = 5
  Placement = pos=(0,0,-163) rot=(0,0,1;0rad)
  sketch-geometry (6):
    g0: ArcOfCircle CenterX=0 CenterY=0 CenterZ=0 NormalX=0 NormalY=0 NormalZ=1 AngleXU=0 Radius=145 StartAngle=1.8326 EndAngle=3.40339
    g1: ArcOfCircle CenterX=0 CenterY=0 CenterZ=0 NormalX=0 NormalY=0 NormalZ=1 AngleXU=0 Radius=205 StartAngle=1.8326 EndAngle=3.40339
    g2: LineSegment [constr] StartX=0 StartY=0 StartZ=0 EndX=-212.504 EndY=-56.9402 EndZ=0
    g3: LineSegment [constr] StartX=0 StartY=0 StartZ=0 EndX=-56.9402 EndY=212.504 EndZ=0
    g4: ArcOfCircle CenterX=-169.037 CenterY=-45.2933 CenterZ=0 NormalX=0 NormalY=0 NormalZ=1 AngleXU=0 Radius=30 StartAngle=3.40339 EndAngle=6.54498
    g5: ArcOfCircle CenterX=-45.2933 CenterY=169.037 CenterZ=0 NormalX=0 NormalY=0 NormalZ=1 AngleXU=0 Radius=30 StartAngle=4.97419 EndAngle=8.11578
  constraints (20):
    c: Coincident(g0,g-1)
    c: Coincident(g2,g0)
    c: Coincident(g3,g1)
    c: Coincident(g1,g0)
    c: PointOnObject(g0,g2)
    c: PointOnObject(g1,g2)
    c: PointOnObject(g1,g3)
    c: Angle(g2,g-1) = 2.87979
    c: Angle(g-2,g3) = 0.261799
    c: Radius(g0) = 145
    c: Diameter(g5) = 60
    c: Coincident(g5,g1)
    c: Coincident(g5,g0)
    c: Diameter(g4) = 60
    c: Coincident(g4,g1)
    c: Coincident(g4,g0)
    c: PointOnObject(g4,g2)
    c: PointOnObject(g0,g3)
    c: Equal(g3,g2)
    c: Distance(g3) = 220
FEATURE [PartDesign::Pad] Pad036
  BaseFeature = -> Pad035
  Direction = (0,0,1)
  Length = 5
  Length2 = 10
  Profile = -> Sketch059
  ReferenceAxis = -> Sketch059 [N_Axis]
  Refine = true
  Suppressed = false
  Type = 0
FEATURE [Sketcher::SketchObject] Sketch004
  ArcFitTolerance = 1e-06
  AttachmentSupport = -> [Pad036]
  ExternalGeometry = -> [Pad036]
  FullyConstrained = true
  MakeInternals = false
  MapMode = 5
  Placement = pos=(0,0,-158) rot=(0,0,1;0rad)
  sketch-geometry (4):
    g0: ArcOfCircle CenterX=0 CenterY=0 CenterZ=0 NormalX=0 NormalY=0 NormalZ=1 AngleXU=0 Radius=145 StartAngle=6.02139 EndAngle=7.59218
    g1: ArcOfCircle CenterX=0 CenterY=0 CenterZ=0 NormalX=0 NormalY=0 NormalZ=1 AngleXU=0 Radius=205 StartAngle=6.02139 EndAngle=7.59218
    g2: ArcOfCircle CenterX=45.2933 CenterY=169.037 CenterZ=0 NormalX=0 NormalY=0 NormalZ=1 AngleXU=0 Radius=30 StartAngle=1.309 EndAngle=4.45059
    g3: ArcOfCircle CenterX=169.037 CenterY=-45.2933 CenterZ=0 NormalX=0 NormalY=0 NormalZ=1 AngleXU=0 Radius=30 StartAngle=2.87979 EndAngle=6.02139
  constraints (11):
    c: Coincident(g0,g-1)
    c: Coincident(g1,g0)
    c: Symmetric(g-3,g0,g-2)
    c: Symmetric(g1,g-3,g-2)
    c: Coincident(g2,g1)
    c: Coincident(g2,g0)
    c: Coincident(g3,g1)
    c: Coincident(g3,g0)
    c: Radius(g2) = 30
    c: Radius(g3) = 30
    c: Symmetric(g-4,g3,g-2)
FEATURE [PartDesign::Pad] Pad003
  BaseFeature = -> Pad036
  Direction = (0,0,1)
  Length = 5
  Length2 = 10
  Profile = -> Sketch004
  ReferenceAxis = -> Sketch004 [N_Axis]
  Refine = true
  Reversed = true
  Suppressed = false
  Type = 0
FEATURE [PartDesign::Pad] Pad037
  BaseFeature = -> Pad003
  Direction = (0.866025,-0.5,1e-16)
  Length = 50
  Length2 = 10
  Midplane = true
  Profile = -> Sketch058
  ReferenceAxis = -> Sketch058 [N_Axis]
  Refine = true
  Suppressed = false
  Type = 0
FEATURE [PartDesign::Pad] Pad038
  BaseFeature = -> Pad037
  Direction = (0.866025,0.5,-1e-16)
  Length = 50
  Length2 = 10
  Midplane = true
  Profile = -> Sketch057
  ReferenceAxis = -> Sketch057 [N_Axis]
  Refine = true
  Suppressed = false
  Type = 0
FEATURE [PartDesign::Pocket] Pocket017
  BaseFeature = -> Pad038
  Direction = (0,0,-1)
  Length = 5
  Length2 = 5
  Profile = -> Sketch056
  ReferenceAxis = -> Sketch056 [N_Axis]
  Refine = true
  Suppressed = false
  Type = 1
FEATURE [Sketcher::SketchObject] Sketch060
  ArcFitTolerance = 1e-06
  AttachmentSupport = -> [Pad003]
  FullyConstrained = true
  MakeInternals = false
  MapMode = 5
  Placement = pos=(0,0,-158) rot=(0,0,1;0rad)
  sketch-geometry (5):
    g0: LineSegment StartX=-120.651 StartY=158.973 StartZ=0 EndX=-77.3494 EndY=183.973 EndZ=0
    g1: LineSegment StartX=-77.3494 StartY=183.973 StartZ=0 EndX=-57.3494 EndY=149.332 EndZ=0
    g2: LineSegment StartX=-57.3494 StartY=149.332 StartZ=0 EndX=-100.651 EndY=124.332 EndZ=0
    g3: LineSegment StartX=-100.651 StartY=124.332 StartZ=0 EndX=-120.651 EndY=158.973 EndZ=0
    g4: LineSegment [constr] StartX=0 StartY=0 StartZ=0 EndX=-115 EndY=199.186 EndZ=0
  constraints (13):
    c: Coincident(g0,g1)
    c: Coincident(g1,g2)
    c: Coincident(g2,g3)
    c: Coincident(g3,g0)
    c: Coincident(g4,g-1)
    c: Angle(g-1,g4) = 2.0944
    c: Symmetric(g0,g0,g4)
    c: Distance(g0) = 50
    c: Parallel(g1,g3)
    c: Distance(g3) = 40
    c: Distance(g4,g2) = 158
    c: Symmetric(g1,g2,g4)
    c: Distance(g4) = 230
FEATURE [PartDesign::CoordinateSystem] Pedestral_Top
  AttacherType = Attacher::AttachEngine3D
  AttachmentOffset = pos=(0,0,0) rot=(0,0,1;-0.523599rad)
  AttachmentSupport = -> [Pocket017]
  MapMode = 45
  Placement = pos=(1.208e-13,1.4e-15,30) rot=(0,0,1;5.75959rad)
FEATURE [PartDesign::Body] Body016  label="Body_Pedestral"
  AllowCompound = false
  Group = -> [Sketch054,Pad034,Sketch055,Pad035,Sketch056,Sketch059,Pad036,Sketch004,Pad003,Sketch060,Sketch058,Pad037,Sketch057,Pad038,Pocket017,Pedestral_Top]
  Origin = -> Origin112
  Tip = -> Pocket017
FEATURE [Sketcher::SketchObject] Sketch061
  ArcFitTolerance = 1e-06
  AttachmentSupport = -> [YZ_Plane113]
  FullyConstrained = true
  MakeInternals = false
  MapMode = 5
  Placement = pos=(0,0,0) rot=(0.57735,0.57735,0.57735;2.0944rad)
  sketch-geometry (1):
    g0: Circle CenterX=0 CenterY=41 CenterZ=0 NormalX=0 NormalY=0 NormalZ=1 AngleXU=0 Radius=2.3
  constraints (3):
    c: PointOnObject(g0,g-2)
    c: Diameter(g0) = 4.6
    c: DistanceY(g-1,g0) = 41
FEATURE [Sketcher::SketchObject] Sketch062
  ArcFitTolerance = 1e-06
  AttachmentSupport = -> [XY_Plane113]
  FullyConstrained = true
  MakeInternals = false
  MapMode = 5
  sketch-geometry (2):
    g0: Circle CenterX=0 CenterY=0 CenterZ=0 NormalX=0 NormalY=0 NormalZ=1 AngleXU=0 Radius=25
    g1: Circle CenterX=0 CenterY=0 CenterZ=0 NormalX=0 NormalY=0 NormalZ=1 AngleXU=0 Radius=23
  constraints (4):
    c: Coincident(g0,g-1)
    c: Coincident(g1,g0)
    c: Diameter(g1) = 46
    c: Diameter(g0) = 50
FEATURE [PartDesign::Pad] Pad039
  Direction = (0,0,1)
  Length = 70
  Length2 = 10
  Profile = -> Sketch062
  ReferenceAxis = -> Sketch062 [N_Axis]
  Refine = true
  Suppressed = false
  Type = 0
FEATURE [PartDesign::Pocket] Pocket018
  BaseFeature = -> Pad039
  Direction = (-1,0,0)
  Length = 5
  Length2 = 5
  Profile = -> Sketch061
  ReferenceAxis = -> Sketch061 [N_Axis]
  Refine = true
  Suppressed = false
  Type = 1
FEATURE [PartDesign::CoordinateSystem] Pedestral_Connector
  AttacherType = Attacher::AttachEngine3D
  AttachmentOffset = pos=(0,0,0) rot=(0,0,-1;1.5708rad)
  AttachmentSupport = -> [Pocket018]
  MapMode = 11
  Placement = pos=(0,0,70) rot=(0,0,1;0rad)
FEATURE [PartDesign::Body] Body017  label="Body_Pedestral_Connector"
  AllowCompound = false
  Group = -> [Sketch061,Sketch062,Pad039,Pocket018,Pedestral_Connector]
  Origin = -> Origin113
  Tip = -> Pocket018
FEATURE [Mesh::Feature] Mesh011  label="Body_BearingLock (Meshed)"
FEATURE [PartDesign::CoordinateSystem] Arm_Axis_Bottom
  AttacherType = Attacher::AttachEngine3D
  AttachmentSupport = -> [Pocket010]
  MapMode = 45
  Placement = pos=(4.26e-14,-84.8494,8) rot=(0,0,1;0rad)
FEATURE [PartDesign::Body] Body003  label="Body_Arm"
  AllowCompound = false
  Group = -> [Sketch007,Pad004,Sketch006,Pocket001,Arm_Axis_Top,Arm_MPU6050_Right,Chamfer002,Sketch027,Pad017,Sketch032,Pocket009,Sketch033,Pocket010,Arm_Axis_Bottom]
  Origin = -> Origin004
  Tip = -> Pocket010
FEATURE [Part::Feature] Part__Feature149  label="C_Disc_D5.0mm_W2.5mm_P5.00mm"
  Placement = pos=(-1,40.5,1.595) rot=(0,0,1;3.14159rad)
  shape: bbox 5.5 x 2.5 x 7.1 mm, 10 faces (baked)
FEATURE [Part::Feature] Part__Feature150  label="R_Axial_DIN0207_L6.3mm_D2.5mm_P7.62mm_Horizontal"
  Placement = pos=(2.69,31.5,1.595) rot=(0,0,1;0rad)
  shape: bbox 8.418 x 2.706 x 5.603 mm, 15 faces (baked)
FEATURE [Part::Feature] Part__Feature151  label="R_Axial_DIN0207_L6.3mm_D2.5mm_P7.62mm_Horizontal001"
  Placement = pos=(-8.62,24,1.595) rot=(0,0,1;0rad)
  shape: bbox 8.418 x 2.706 x 5.603 mm, 15 faces (baked)
FEATURE [Part::Feature] Part__Feature152  label="PinHeader_1x08_P2.54mm_Vertical"
  Placement = pos=(-14.5,14.42,1.595) rot=(0,0,1;3.14159rad)
  shape: bbox 2.54 x 20.32 x 11.54 mm, 196 faces (baked)
FEATURE [Part::Feature] Part__Feature153  label="TerminalBlock_Phoenix_MKDS-1,5-2_1x02_P5.00mm_Horizontal"
  Placement = pos=(26,38.1725,1.595) rot=(0,0,1;3.14159rad)
  shape: bbox 10.74 x 9.8 x 17.3 mm, 89 faces (baked)
FEATURE [Part::Feature] Part__Feature154  label="PinHeader_1x04_P2.54mm_Vertical"
  Placement = pos=(-7.5,6,1.595) rot=(0,0,-1;1.5708rad)
  shape: bbox 10.16 x 2.54 x 11.54 mm, 100 faces (baked)
FEATURE [Part::Feature] Part__Feature155  label="TO-92L_Inline"
  Placement = pos=(47,6.5,1.595) rot=(0,0,1;1.5708rad)
  shape: bbox 3.9 x 4.9 x 12.95 mm, 19 faces (baked)
FEATURE [Part::Feature] Part__Feature156  label="R_Axial_DIN0207_L6.3mm_D2.5mm_P7.62mm_Horizontal002"
  Placement = pos=(21.81,25,1.595) rot=(0,0,1;3.14159rad)
  shape: bbox 8.418 x 2.706 x 5.603 mm, 15 faces (baked)
FEATURE [Part::Feature] Part__Feature157  label="Buzzer_12x9.5RM7.6"
  Placement = pos=(40,31.1,1.595) rot=(0,0,-1;1.5708rad)
  shape: bbox 12.99 x 12.99 x 12.53 mm, 13 faces (baked)
FEATURE [Part::Feature] Part__Feature158  label="PinHeader_1x15_P2.54mm_Vertical"
  Placement = pos=(3.81,1.27,-0.085) rot=(0.707107,-0.707107,0;3.14159rad)
  shape: bbox 38.1 x 2.54 x 11.54 mm, 364 faces (baked)
FEATURE [Part::Feature] Part__Feature159  label="PinHeader_1x15_P2.54mm_Vertical001"
  Placement = pos=(3.81,16.51,-0.085) rot=(0.707107,-0.707107,0;3.14159rad)
  shape: bbox 38.1 x 2.54 x 11.54 mm, 364 faces (baked)
FEATURE [Part::Feature] Part__Feature160  label="kicadTest_PCB"
  shape: bbox 70 x 50 x 1.51 mm, 41 faces (baked)
FEATURE [PartDesign::CoordinateSystem] main_circuit
  AttacherType = Attacher::AttachEngine3D
  AttachmentOffset = pos=(0,0,0) rot=(0,0,-1;1.5708rad)
  AttachmentSupport = -> [Part__Feature160]
  MapMode = 45
  Placement = pos=(-17.96,-2.96,1.51) rot=(0,0,1.00001;4e-06rad)
FEATURE [PartDesign::CoordinateSystem] circuit_PCB
  AttacherType = Attacher::AttachEngine3D
  AttachmentSupport = -> [Part__Feature160]
  MapMode = 45
  Placement = pos=(0,0,0.755) rot=(0,0,1;0rad)
FEATURE [App::Part] main_Circuit_kicad_Circuit_1  label="main_Circuit-kicad"
  Group = -> [Part__Feature149,Part__Feature150,Part__Feature151,Part__Feature152,Part__Feature153,Part__Feature154,Part__Feature155,Part__Feature156,Part__Feature157,Part__Feature158,Part__Feature159,Part__Feature160,main_circuit,circuit_PCB]
  Origin = -> Origin114
FEATURE [Sketcher::SketchObject] Sketch064
  ArcFitTolerance = 1e-06
  AttachmentSupport = -> [XY_Plane115]
  FullyConstrained = false
  MakeInternals = false
  MapMode = 5
  sketch-geometry (4):
    g0: LineSegment StartX=-25.456 StartY=35.625 StartZ=0 EndX=-25.456 EndY=-34.975 EndZ=0
    g1: LineSegment StartX=-25.456 StartY=-34.975 StartZ=0 EndX=25.144 EndY=-34.975 EndZ=0
    g2: LineSegment StartX=25.144 StartY=-34.975 StartZ=0 EndX=25.144 EndY=35.625 EndZ=0
    g3: LineSegment StartX=25.144 StartY=35.625 StartZ=0 EndX=-25.456 EndY=35.625 EndZ=0
  constraints (10):
    c: Coincident(g0,g1)
    c: Coincident(g1,g2)
    c: Coincident(g2,g3)
    c: Coincident(g3,g0)
    c: Vertical(g0)
    c: Vertical(g2)
    c: Horizontal(g1)
    c: Horizontal(g3)
    c: DistanceX(g3,g3) = 50.6
    c: DistanceY(g0,g0) = 70.6
FEATURE [Sketcher::SketchObject] Sketch065
  ArcFitTolerance = 1e-06
  AttachmentSupport = -> [XY_Plane115]
  FullyConstrained = true
  MakeInternals = false
  MapMode = 5
  sketch-geometry (12):
    g0: LineSegment StartX=-22.96 StartY=27.96 StartZ=0 EndX=-22.96 EndY=-27.96 EndZ=0
    g1: LineSegment StartX=-17.96 StartY=-32.96 StartZ=0 EndX=17.96 EndY=-32.96 EndZ=0
    g2: LineSegment StartX=22.96 StartY=-27.96 StartZ=0 EndX=22.96 EndY=27.96 EndZ=0
    g3: LineSegment StartX=18.053 StartY=32 StartZ=0 EndX=-18.053 EndY=32 EndZ=0
    g4: LineSegment StartX=-27 StartY=37 StartZ=0 EndX=-27 EndY=-37 EndZ=0
    g5: LineSegment StartX=-27 StartY=-37 StartZ=0 EndX=27 EndY=-37 EndZ=0
    g6: LineSegment StartX=27 StartY=-37 StartZ=0 EndX=27 EndY=37 EndZ=0
    g7: LineSegment StartX=27 StartY=37 StartZ=0 EndX=-27 EndY=37 EndZ=0
    g8: ArcOfCircle CenterX=-22.96 CenterY=32.96 CenterZ=0 NormalX=0 NormalY=0 NormalZ=1 AngleXU=0 Radius=5 StartAngle=4.71239 EndAngle=6.08999
    g9: ArcOfCircle CenterX=22.96 CenterY=32.96 CenterZ=0 NormalX=0 NormalY=0 NormalZ=1 AngleXU=0 Radius=5 StartAngle=3.33479 EndAngle=4.71239
    g10: ArcOfCircle CenterX=22.96 CenterY=-32.96 CenterZ=0 NormalX=0 NormalY=0 NormalZ=1 AngleXU=0 Radius=5 StartAngle=1.5708 EndAngle=3.14159
    g11: ArcOfCircle CenterX=-22.96 CenterY=-32.96 CenterZ=0 NormalX=0 NormalY=0 NormalZ=1 AngleXU=0 Radius=5 StartAngle=3e-16 EndAngle=1.5708
  constraints (34):
    c: Coincident(g4,g5)
    c: Coincident(g5,g6)
    c: Coincident(g6,g7)
    c: Coincident(g7,g4)
    c: Vertical(g4)
    c: Vertical(g6)
    c: Horizontal(g5)
    c: Horizontal(g7)
    c: DistanceX(g7,g7) = 54
    c: DistanceY(g6,g6) = 74
    c: Symmetric(g4,g5,g-1)
    c: Equal(g8,g9)
    c: Equal(g9,g10)
    c: Equal(g10,g11)
    c: Diameter(g9) = 10
    c: Coincident(g3,g8)
    c: Coincident(g0,g8)
    c: Coincident(g3,g9)
    c: Coincident(g2,g9)
    c: Coincident(g0,g11)
    c: Coincident(g1,g11)
    c: Coincident(g1,g10)
    c: Coincident(g2,g10)
    c: Symmetric(g3,g3,g-2)
    c: Symmetric(g0,g0,g-1)
    c: Symmetric(g1,g1,g-2)
    c: Symmetric(g2,g2,g-1)
    c: Symmetric(g8,g10,g-1)
    c: DistanceY(g3,g4) = 5
    c: DistanceY(g10,g8) = 65.92
    c: DistanceX(g11,g10) = 45.92
    c: PointOnObject(g11,g1)
    c: PointOnObject(g8,g0)
    c: PointOnObject(g10,g2)
FEATURE [PartDesign::Pad] Pad040
  Direction = (0,0,1)
  Length = 26
  Length2 = 10
  Profile = -> Sketch065
  ReferenceAxis = -> Sketch065 [N_Axis]
  Refine = true
  Reversed = true
  Suppressed = false
  Type = 0
FEATURE [PartDesign::Pocket] Pocket019
  BaseFeature = -> Pad040
  Direction = (0,0,-1)
  Length = 2
  Length2 = 5
  Profile = -> Sketch064
  ReferenceAxis = -> Sketch064 [N_Axis]
  Refine = true
  Suppressed = false
  Type = 0
FEATURE [Sketcher::SketchObject] Sketch066
  ArcFitTolerance = 1e-06
  AttachmentSupport = -> [Pocket019]
  FullyConstrained = true
  MakeInternals = false
  MapMode = 5
  Placement = pos=(0,0,-2) rot=(0,0,1;0rad)
  sketch-geometry (4):
    g0: Circle CenterX=-22.96 CenterY=32.96 CenterZ=0 NormalX=0 NormalY=0 NormalZ=1 AngleXU=0 Radius=1.3
    g1: Circle CenterX=22.96 CenterY=32.96 CenterZ=0 NormalX=0 NormalY=0 NormalZ=1 AngleXU=0 Radius=1.3
    g2: Circle CenterX=22.96 CenterY=-32.96 CenterZ=0 NormalX=0 NormalY=0 NormalZ=1 AngleXU=0 Radius=1.3
    g3: Circle CenterX=-22.96 CenterY=-32.96 CenterZ=0 NormalX=0 NormalY=0 NormalZ=1 AngleXU=0 Radius=1.3
  constraints (9):
    c: Equal(g0,g1)
    c: Equal(g1,g2)
    c: Equal(g2,g3)
    c: Symmetric(g3,g0,g-1)
    c: Symmetric(g0,g1,g-2)
    c: Symmetric(g3,g2,g-2)
    c: DistanceX(g0,g1) = 45.92
    c: DistanceY(g2,g1) = 65.92
    c: Diameter(g0) = 2.6
FEATURE [PartDesign::Pocket] Pocket020
  BaseFeature = -> Pocket019
  Direction = (0,0,-1)
  Length = 5
  Length2 = 5
  Profile = -> Sketch066
  ReferenceAxis = -> Sketch066 [N_Axis]
  Refine = true
  Suppressed = false
  Type = 1
FEATURE [Sketcher::SketchObject] Sketch067
  ArcFitTolerance = 1e-06
  AttachmentSupport = -> [Pocket020]
  ExternalGeometry = -> [Pocket020]
  FullyConstrained = true
  MakeInternals = false
  MapMode = 5
  Placement = pos=(0,0,-26) rot=(1,0,0;3.14159rad)
  sketch-geometry (6):
    g0: ArcOfCircle CenterX=-27.5 CenterY=42 CenterZ=0 NormalX=0 NormalY=0 NormalZ=1 AngleXU=0 Radius=7 StartAngle=0 EndAngle=4.71239
    g1: ArcOfCircle CenterX=27.5 CenterY=42 CenterZ=0 NormalX=0 NormalY=0 NormalZ=1 AngleXU=0 Radius=7 StartAngle=4.71239 EndAngle=9.42478
    g2: LineSegment StartX=-20.5 StartY=42 StartZ=0 EndX=20.5 EndY=42 EndZ=0
    g3: LineSegment StartX=-27.5 StartY=35 StartZ=0 EndX=27.5 EndY=35 EndZ=0
    g4: Circle CenterX=-27.5 CenterY=42 CenterZ=0 NormalX=0 NormalY=0 NormalZ=1 AngleXU=0 Radius=2.3
    g5: Circle CenterX=27.5 CenterY=42 CenterZ=0 NormalX=0 NormalY=0 NormalZ=1 AngleXU=0 Radius=2.3
  constraints (16):
    c: Horizontal(g2)
    c: Symmetric(g0,g1,g-2)
    c: DistanceX(g0,g1) = 55
    c: Equal(g1,g0)
    c: Diameter(g1) = 14
    c: DistanceY(g-3,g0) = 5
    c: Horizontal(g3)
    c: PointOnObject(g0,g2)
    c: Coincident(g0,g3)
    c: Coincident(g0,g2)
    c: Coincident(g1,g2)
    c: Tangent(g1,g3) = -1.5708
    c: Coincident(g4,g0)
    c: Coincident(g5,g1)
    c: Equal(g5,g4)
    c: Diameter(g5) = 4.6
FEATURE [PartDesign::Pad] Pad041
  BaseFeature = -> Pocket020
  Direction = (0,0,-1)
  Length = 5
  Length2 = 10
  Profile = -> Sketch067
  ReferenceAxis = -> Sketch067 [N_Axis]
  Refine = true
  Reversed = true
  Suppressed = false
  Type = 0
FEATURE [PartDesign::CoordinateSystem] Circuit_House
  AttacherType = Attacher::AttachEngine3D
  AttachmentSupport = -> [Pad041]
  MapMode = 45
  Placement = pos=(27.5,-42,-21) rot=(0,0,0.999999;1.4e-05rad)
FEATURE [PartDesign::CoordinateSystem] Circuit_House_Top
  AttacherType = Attacher::AttachEngine3D
  AttachmentSupport = -> [Pad041]
  MapMode = 45
  Placement = pos=(-22.96,32.96,-2) rot=(0,0,1;0rad)
FEATURE [PartDesign::Body] Body018  label="Body_circuit_house"
  AllowCompound = false
  Group = -> [Sketch065,Pad040,Sketch064,Pocket019,Sketch066,Pocket020,Sketch067,Pad041,Circuit_House,Circuit_House_Top]
  Origin = -> Origin115
  Tip = -> Pad041
FEATURE [PartDesign::CoordinateSystem] Trepied_Bottom
  AttacherType = Attacher::AttachEngine3D
  AttachmentOffset = pos=(0,0,0) rot=(0,0,-1;0.523599rad)
  AttachmentSupport = -> [Pad033]
  MapMode = 45
  Placement = pos=(-47.6314,27.5,3) rot=(0,0,1;0.523595rad)
FEATURE [App::Link] Body_Trepied  label="Body_Trepied001"
  AttachedBy = #Trepied
  AttachedTo = Body_Support#Support_Foot
  AttachmentOffset = pos=(0,0,-6) rot=(0,0,1;0rad)
  LinkPlacement = pos=(1.42e-14,69.2314,-29) rot=(0,0,-1;0.523599rad)
  LinkedObject = -> Body015
  Placement = pos=(1.42e-14,69.2314,-29) rot=(0,0,-1;0.523599rad)
  SolverId = Asm4EE
  expr: Placement = Body_Support.Placement * Support_Foot.Placement * AttachmentOffset * Trepied.Placement ^ -1
FEATURE [PartDesign::CoordinateSystem] Trepied_Axial
  AttacherType = Attacher::AttachEngine3D
  AttachmentSupport = -> [Pad033]
  MapMode = 45
  Placement = pos=(1.683e-13,3.2e-15,-57) rot=(0,0,1;0rad)
FEATURE [PartDesign::Body] Body015  label="Body_Trepied"
  AllowCompound = false
  Group = -> [Sketch052,Pad032,Fillet009,Sketch051,Pocket016,PolarPattern006,Trepied,Sketch053,Pad033,Trepied_Bottom,Trepied_Axial]
  Origin = -> Origin111
  Tip = -> Pad033
FEATURE [App::DocumentObjectGroup] Parts
  Group = -> [Body,Body003,Body004,Body005,Body002,Body001,Body006,Body007,PCB,Body014,Body015,Body016,Body017,main_Circuit_kicad_Circuit_1,Body018]
FEATURE [App::Link] Body_Pedestral_Connector  label="Body_Pedestral_Connector001"
  AttachedBy = #Pedestral_Connector
  AttachedTo = Body_Trepied#Trepied_Axial
  AttachmentOffset = pos=(0,0,36) rot=(0,0,1;0rad)
  LinkPlacement = pos=(1.851e-13,69.2314,-120) rot=(0,0,-1;0.523599rad)
  LinkedObject = -> Body017
  Placement = pos=(1.851e-13,69.2314,-120) rot=(0,0,-1;0.523599rad)
  SolverId = Asm4EE
  expr: Placement = Body_Trepied.Placement * Trepied_Axial.Placement * AttachmentOffset * Pedestral_Connector.Placement ^ -1
FEATURE [App::Link] Body_Pedestral  label="Body_Pedestral001"
  AttachedBy = #Pedestral_Top
  AttachedTo = Body_Pedestral_Connector#Pedestral_Connector
  AttachmentOffset = pos=(0,0,-50) rot=(0,0,1;0rad)
  LinkPlacement = pos=(6.69e-14,69.2314,-130) rot=(0,0,1;0rad)
  LinkedObject = -> Body016
  Placement = pos=(6.69e-14,69.2314,-130) rot=(0,0,1;0rad)
  SolverId = Asm4EE
  expr: Placement = Body_Pedestral_Connector.Placement * Pedestral_Connector.Placement * AttachmentOffset * Pedestral_Top.Placement ^ -1
FEATURE [App::Link] Body_circuit_house  label="Body_circuit_house001"
  AttachedBy = #Circuit_House
  AttachedTo = Body_Trepied#Trepied_Bottom
  AttachmentOffset = pos=(0,0,5) rot=(0,0,1;3.14159rad)
  LinkPlacement = pos=(-0.000720319,74.8623,1.1973e-12) rot=(0,0,0.999992;3.14158rad)
  LinkedObject = -> Body018
  Placement = pos=(-0.000720319,74.8623,1.1973e-12) rot=(0,0,0.999992;3.14158rad)
  SolverId = Asm4EE
  expr: Placement = Body_Trepied.Placement * Trepied_Bottom.Placement * AttachmentOffset * Circuit_House.Placement ^ -1
FEATURE [App::Link] main_Circuit_kicad  label="main_Circuit-kicad001"
  AttachedBy = #main_circuit
  AttachedTo = Body_circuit_house#Circuit_House_Top
  AttachmentOffset = pos=(0,0,4) rot=(0,0,1;4.71239rad)
  LinkPlacement = pos=(19.9991,59.862,0.49) rot=(0,0,-0.999992;4.71241rad)
  LinkedObject = -> main_Circuit_kicad_Circuit_1
  Placement = pos=(19.9991,59.862,0.49) rot=(0,0,-0.999992;4.71241rad)
  SolverId = Asm4EE
  expr: Placement = Body_circuit_house.Placement * Circuit_House_Top.Placement * AttachmentOffset * main_circuit.Placement ^ -1
FEATURE [App::Link] PCB001
  AttachedBy = #Nano_USB_Left
  AttachedTo = main_Circuit_kicad#circuit_PCB
  AttachmentOffset = pos=(1.3,1.25,2) rot=(0,0,1;4.71239rad)
  LinkPlacement = pos=(20.0191,59.892,3.245) rot=(0,0,0.999992;1.57078rad)
  LinkedObject = -> PCB
  Placement = pos=(20.0191,59.892,3.245) rot=(0,0,0.999992;1.57078rad)
  SolverId = Asm4EE
  expr: Placement = main_Circuit_kicad.Placement * circuit_PCB.Placement * AttachmentOffset * Nano_USB_Left.Placement ^ -1
FEATURE [App::Part] Assembly
  AssemblyType = Part::Link
  Description = Pendulum - 3D printing models
  Group = -> [LCS_Origin,Constraints,Variables,Configurations,Body_Rondelle,Motor_Shaft,Body_circuit_house,main_Circuit_kicad,PCB001]
  Origin = -> Origin
  Type = Assembly
FEATURE [Part::FeaturePython] Screw028  label="M4x25-Screw084"  # WARN: FeaturePython — macro-defined, semantics opaque (R4)
  BaseObject = -> Assembly [Body_circuit_house.Pocket021.Edge23]
  Diameter = 6
  Invert = true
  LeftHanded = false
  Length = 7
  LengthCustom = 25
  MatchOuter = false
  Offset = 1
  OffsetAngle = 0
  Placement = pos=(-27.5,116.863,-20) rot=(0,0,1;0rad)
  Thread = false
  Type = 62
FEATURE [Part::FeaturePython] Screw029  label="M4x25-Screw085"  # WARN: FeaturePython — macro-defined, semantics opaque (R4)
  BaseObject = -> Assembly [Body_circuit_house.Pocket021.Edge22]
  Diameter = 6
  Invert = true
  LeftHanded = false
  Length = 7
  LengthCustom = 25
  MatchOuter = false
  Offset = 1
  OffsetAngle = 0
  Placement = pos=(27.5,116.862,-20) rot=(0,0,1;0rad)
  Thread = false
  Type = 62
FEATURE [Part::FeaturePython] Nut029  label="M4-Nut298"  # WARN: FeaturePython — macro-defined, semantics opaque (R4)
  BaseObject = -> Assembly [Body_Trepied.Pad033.Edge13]
  Diameter = 6
  Invert = false
  LeftHanded = false
  MatchOuter = false
  Offset = -5
  OffsetAngle = 0
  Placement = pos=(27.5,116.863,-34) rot=(0,0,1;0rad)
  Thread = false
  Type = 31
FEATURE [Part::FeaturePython] Nut030  label="M4-Nut299"  # WARN: FeaturePython — macro-defined, semantics opaque (R4)
  BaseObject = -> Assembly [Body_Trepied.Pad033.Edge11]
  Diameter = 6
  Invert = false
  LeftHanded = false
  MatchOuter = false
  Offset = -5
  OffsetAngle = 0
  Placement = pos=(-27.5,116.863,-34) rot=(0,0,1;0rad)
  Thread = false
  Type = 31
FEATURE [Mesh::Feature] Mesh013  label="Body_circuit_house (Meshed)"
FEATURE [App::DocumentObjectGroup] Group001  label="Group_Meshes"
  Group = -> [Mesh010,Mesh002,Mesh003,Mesh006,Mesh,Mesh008,Mesh009,Mesh011,Mesh013]
FEATURE [Part::MultiFuse] Fusion  label="Fusion_Arm"
  Refine = true
  Shapes = -> [Body_Arm,Body_Motor,Body_MPU6050,Body_BearingLock,Screw,Screw001,Screw002,Screw003,Screw004,Nut,Nut003,Screw018,Screw019,Screw020,Nut019,Nut020,Nut021]
FEATURE [Part::MultiFuse] Fusion001  label="Fusion_Reaction_Wheel"
  Placement = pos=(0,0,-169.7) rot=(0,0,1;0rad)
  Refine = true
  Shapes = -> [Body_ReactionWheel,Screw006,Screw007,Screw008,Screw009,Screw010,Screw011,Screw012,Screw013,Screw014,Screw015,Nut004,Nut005,Nut006,Nut007,Nut008,Nut009,Nut010,Nut011,Nut012,Nut013,Nut014,Nut015,Screw016,Screw017]
FEATURE [Part::MultiFuse] Fusion002  label="Fusion_Pedestal"
  Refine = true
  Shapes = -> [Body_Support,Body_Bearing,Body_Trepied,Body_Pedestral_Connector,Body_Pedestral,Screw021,Nut022,Nut028,Screw027,Screw026,Nut027]
FEATURE [App::DocumentObjectGroup] Group  label="Group_Screws"
  Group = -> [Screw028,Screw029,Nut029,Nut030,Fusion,Fusion001,Fusion002]
FEATURE [Mesh::Feature] Mesh014  label="Fusion_Arm (Meshed)"
FEATURE [Mesh::Feature] Mesh015  label="Fusion_Reaction_Wheel (Meshed)"
FEATURE [Mesh::Feature] Mesh016  label="Fusion_Pedestal (Meshed)"
FEATURE [Mesh::Feature] scale  label="scale_Fusion_Arm (Meshed)"
  Placement = pos=(0,0,0) rot=(-0.57735,0.57735,0.57735;2.0944rad)
FEATURE [Mesh::Feature] scale001  label="scale_Fusion_Reaction_Wheel (Meshed)"
FEATURE [Mesh::Feature] scale002  label="scale_Fusion_Pedestal (Meshed)"
  Placement = pos=(0,0,0) rot=(1,0,0;-1.5708rad)
